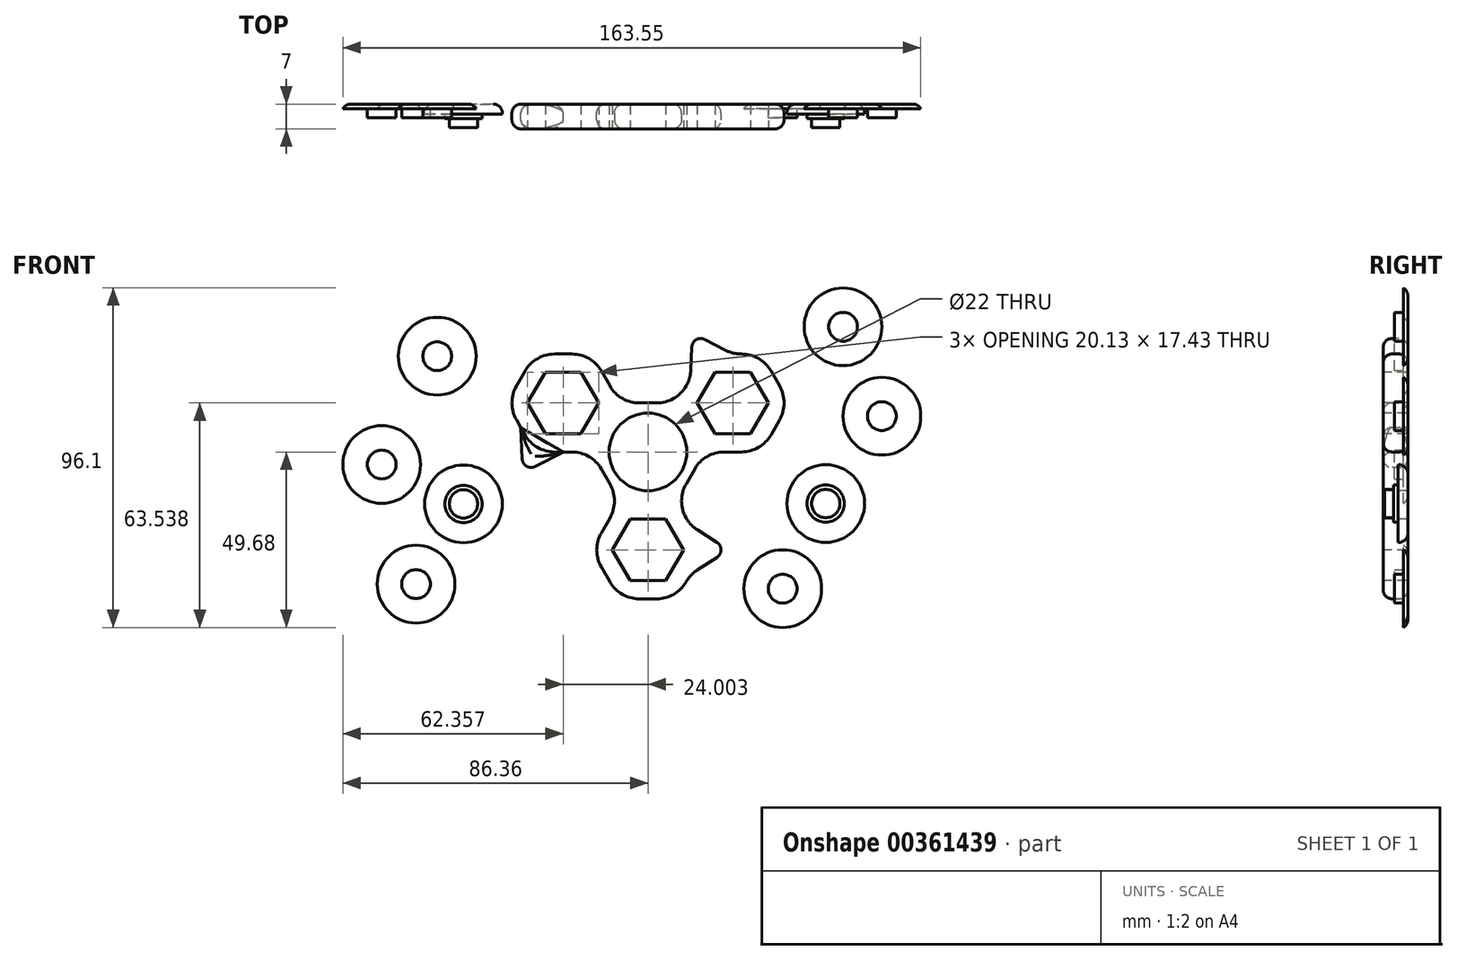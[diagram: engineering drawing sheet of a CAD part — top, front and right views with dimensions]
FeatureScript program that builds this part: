
annotation { "Feature Type Name" : "Feature", "Feature Type Description" : "" }
export const myFeature = defineFeature(function(context is Context, id is Id, definition is map)
    precondition{}
    {
        {
            var Q0;
            Q0=qCreatedBy(makeId("Front.planeOp"),FACE);
            var sketch = newSketch(context, id + "F0", { "sketchPlane" : qUnion([Q0])});
            skCircle(sketch, "E0.cCircle", {"center": v(0, 0) * mm, "radius": 13.86 * mm, "construction": true});
            skLineSegment(sketch, "E0.0", {"start": v(16, 0) * mm, "end": v(8, -13.86) * mm});
            skLineSegment(sketch, "E0.1", {"start": v(8, -13.86) * mm, "end": v(-8, -13.86) * mm});
            skLineSegment(sketch, "E0.2", {"start": v(-8, -13.86) * mm, "end": v(-16, 0) * mm});
            skLineSegment(sketch, "E0.3", {"start": v(-16, 0) * mm, "end": v(-8, 13.86) * mm});
            skLineSegment(sketch, "E0.4", {"start": v(-8, 13.86) * mm, "end": v(8, 13.86) * mm});
            skLineSegment(sketch, "E0.5", {"start": v(8, 13.86) * mm, "end": v(16, 0) * mm});
            skPoint(sketch, "E0.0.midPoint", {"position": v(12, -6.93) * mm});
            skCircle(sketch, "E1.cCircle", {"center": v(24, 13.86) * mm, "radius": 13.86 * mm, "construction": true});
            skLineSegment(sketch, "E1.0", {"start": v(32, 0) * mm, "end": v(16, 0) * mm});
            skLineSegment(sketch, "E1.1", {"start": v(16, 0) * mm, "end": v(8, 13.86) * mm});
            skLineSegment(sketch, "E1.2", {"start": v(8, 13.86) * mm, "end": v(16, 27.72) * mm});
            skLineSegment(sketch, "E1.3", {"start": v(16, 27.72) * mm, "end": v(32, 27.72) * mm});
            skLineSegment(sketch, "E1.4", {"start": v(32, 27.72) * mm, "end": v(40, 13.86) * mm});
            skLineSegment(sketch, "E1.5", {"start": v(40, 13.86) * mm, "end": v(32, 0) * mm});
            skPoint(sketch, "E1.0.midPoint", {"position": v(24, 0) * mm});
            skCircle(sketch, "E2.cCircle", {"center": v(-24, 13.86) * mm, "radius": 13.86 * mm, "construction": true});
            skLineSegment(sketch, "E2.0", {"start": v(-16, 0) * mm, "end": v(-32, 0) * mm});
            skLineSegment(sketch, "E2.1", {"start": v(-32, 0) * mm, "end": v(-40, 13.86) * mm});
            skLineSegment(sketch, "E2.2", {"start": v(-40, 13.86) * mm, "end": v(-32, 27.72) * mm});
            skLineSegment(sketch, "E2.3", {"start": v(-32, 27.72) * mm, "end": v(-16, 27.72) * mm});
            skLineSegment(sketch, "E2.4", {"start": v(-16, 27.72) * mm, "end": v(-8, 13.86) * mm});
            skLineSegment(sketch, "E2.5", {"start": v(-8, 13.86) * mm, "end": v(-16, 0) * mm});
            skCircle(sketch, "E3.cCircle", {"center": v(0, -27.72) * mm, "radius": 13.86 * mm, "construction": true});
            skLineSegment(sketch, "E3.0", {"start": v(8, -41.57) * mm, "end": v(-8, -41.57) * mm});
            skLineSegment(sketch, "E3.1", {"start": v(-8, -41.57) * mm, "end": v(-16, -27.72) * mm});
            skLineSegment(sketch, "E3.2", {"start": v(-16, -27.72) * mm, "end": v(-8, -13.86) * mm});
            skLineSegment(sketch, "E3.3", {"start": v(-8, -13.86) * mm, "end": v(8, -13.86) * mm});
            skLineSegment(sketch, "E3.4", {"start": v(8, -13.86) * mm, "end": v(16, -27.72) * mm});
            skLineSegment(sketch, "E3.5", {"start": v(16, -27.72) * mm, "end": v(8, -41.57) * mm});
            skLineSegment(sketch, "E4", {"start": v(-36, 6.93) * mm, "end": v(-24, 0) * mm});
            skLineSegment(sketch, "E5", {"start": v(-24, 0) * mm, "end": v(-36, 6.93) * mm});
            skLineSegment(sketch, "E6", {"start": v(24, 27.72) * mm, "end": v(12, 20.79) * mm});
            skLineSegment(sketch, "E7", {"start": v(12, -20.79) * mm, "end": v(12, -34.65) * mm});
            skLineSegment(sketch, "E8", {"start": v(-24, 13.86) * mm, "end": v(-35.43, -5.94) * mm});
            skLineSegment(sketch, "E9", {"start": v(24, 13.86) * mm, "end": v(12.57, 33.66) * mm});
            skLineSegment(sketch, "E10", {"start": v(0, -27.72) * mm, "end": v(22.86, -27.72) * mm});
            skPoint(sketch, "E10.endSnap0", {"position": v(12, -27.72) * mm});
            skLineSegment(sketch, "E11", {"start": v(-36, 6.93) * mm, "end": v(-35.43, -5.94) * mm});
            skLineSegment(sketch, "E12", {"start": v(-24, 0) * mm, "end": v(-35.43, -5.94) * mm});
            skLineSegment(sketch, "E13", {"start": v(12, -20.79) * mm, "end": v(22.86, -27.72) * mm});
            skLineSegment(sketch, "E14", {"start": v(12, -34.65) * mm, "end": v(22.86, -27.72) * mm});
            skLineSegment(sketch, "E15", {"start": v(12, 20.79) * mm, "end": v(12.57, 33.66) * mm});
            skLineSegment(sketch, "E16", {"start": v(24, 27.72) * mm, "end": v(12.57, 33.66) * mm});
            skLineSegment(sketch, "E17", {"start": v(12, -6.93) * mm, "end": v(0, -13.86) * mm});
            skLineSegment(sketch, "E18", {"start": v(6, -10.4) * mm, "end": v(8, -13.86) * mm});
            skLineSegment(sketch, "E19", {"start": v(-12, 6.93) * mm, "end": v(-12, -6.93) * mm});
            skLineSegment(sketch, "E20", {"start": v(-16, 0) * mm, "end": v(-12, 0) * mm});
            skLineSegment(sketch, "E21", {"start": v(-12, 0) * mm, "end": v(-14.39, 0) * mm});
            skLineSegment(sketch, "E22", {"start": v(0, 13.86) * mm, "end": v(12, 6.93) * mm});
            skLineSegment(sketch, "E23", {"start": v(8, 13.86) * mm, "end": v(6, 10.4) * mm});
            skPoint(sketch, "E23.endSnap0", {"position": v(6, 10.4) * mm});
            skLineSegment(sketch, "E24", {"start": v(6, 10.4) * mm, "end": v(7.2, 12.46) * mm});
            skLineSegment(sketch, "E25", {"start": v(9.55, 8.35) * mm, "end": v(6, 10.4) * mm});
            skLineSegment(sketch, "E26", {"start": v(6, -10.4) * mm, "end": v(7.2, -12.46) * mm});
            skCircle(sketch, "E27", {"center": v(0, 0) * mm, "radius": 42.34 * mm});
            skSolve(sketch);
        }
        {
            var Q0;
            {var subQ3=sQuery(id+"F0.wireOp",EDGE,"E15");Q0=makeQuery(id+"F0.imprint","IMPRINT",FACE,{"disambiguationData":[TD([[makeQuery(id+"F0.imprint","IMPRINT",EDGE,{"derivedFrom":subQ3}),-1.0]])]});}
            var Q1;
            {var subQ3=sQuery(id+"F0.wireOp",EDGE,"E16");Q1=makeQuery(id+"F0.imprint","IMPRINT",FACE,{"disambiguationData":[TD([[makeQuery(id+"F0.imprint","IMPRINT",EDGE,{"derivedFrom":subQ3}),1.0]])]});}
            var Q2;
            {var subQ3=sQuery(id+"F0.wireOp",EDGE,"E12");Q2=makeQuery(id+"F0.imprint","IMPRINT",FACE,{"disambiguationData":[TD([[makeQuery(id+"F0.imprint","IMPRINT",EDGE,{"derivedFrom":subQ3}),-1.0]])]});}
            var Q3;
            {var subQ3=sQuery(id+"F0.wireOp",EDGE,"E11");Q3=makeQuery(id+"F0.imprint","IMPRINT",FACE,{"disambiguationData":[TD([[makeQuery(id+"F0.imprint","IMPRINT",EDGE,{"derivedFrom":subQ3}),1.0]])]});}
            var Q4;
            {var subQ3=sQuery(id+"F0.wireOp",EDGE,"E13");Q4=makeQuery(id+"F0.imprint","IMPRINT",FACE,{"disambiguationData":[TD([[makeQuery(id+"F0.imprint","IMPRINT",EDGE,{"derivedFrom":subQ3}),-1.0]])]});}
            var Q5;
            {var subQ3=sQuery(id+"F0.wireOp",EDGE,"E14");Q5=makeQuery(id+"F0.imprint","IMPRINT",FACE,{"disambiguationData":[TD([[makeQuery(id+"F0.imprint","IMPRINT",EDGE,{"derivedFrom":subQ3}),1.0]])]});}
            var Q6;
            {var subQ3=sQuery(id+"F0.wireOp",EDGE,"E3.4");var subQ5=sQuery(id+"F0.wireOp",EDGE,"E3.3");var subQ6=makeQuery(id+"F0.imprint","INTERSECT",VERTEX,{"derivedFrom":[subQ5,subQ3]});Q6=makeQuery(id+"F0.imprint","IMPRINT",FACE,{"disambiguationData":[TD([[makeQuery(id+"F0.imprint","IMPRINT",EDGE,{"disambiguationData":[TD([[subQ6,1.0]])],"derivedFrom":subQ5}),-1.0]])]});}
            var Q7;
            {var subQ0=sQuery(id+"F0.wireOp",EDGE,"E20");Q7=makeQuery(id+"F0.imprint","IMPRINT",FACE,{"disambiguationData":[TD([[makeQuery(id+"F0.imprint","IMPRINT",EDGE,{"derivedFrom":subQ0}),-1.0]])]});}
            var Q8;
            {var subQ0=sQuery(id+"F0.wireOp",EDGE,"E23");Q8=makeQuery(id+"F0.imprint","IMPRINT",FACE,{"disambiguationData":[TD([[makeQuery(id+"F0.imprint","IMPRINT",EDGE,{"derivedFrom":subQ0}),-1.0]])]});}
            var Q9;
            {var subQ0=sQuery(id+"F0.wireOp",EDGE,"E9");var subQ3=sQuery(id+"F0.wireOp",EDGE,"E6");var subQ5=makeQuery(id+"F0.imprint","INTERSECT",VERTEX,{"derivedFrom":[subQ3,subQ0]});Q9=makeQuery(id+"F0.imprint","IMPRINT",FACE,{"disambiguationData":[TD([[makeQuery(id+"F0.imprint","IMPRINT",EDGE,{"disambiguationData":[TD([[subQ5,-1.0]])],"derivedFrom":subQ3}),-1.0]])]});}
            var Q10;
            {var subQ0=sQuery(id+"F0.wireOp",EDGE,"E9");var subQ3=sQuery(id+"F0.wireOp",EDGE,"E6");var subQ5=makeQuery(id+"F0.imprint","INTERSECT",VERTEX,{"derivedFrom":[subQ3,subQ0]});Q10=makeQuery(id+"F0.imprint","IMPRINT",FACE,{"disambiguationData":[TD([[makeQuery(id+"F0.imprint","IMPRINT",EDGE,{"disambiguationData":[TD([[subQ5,1.0]])],"derivedFrom":subQ3}),-1.0]])]});}
            var Q11;
            {var subQ0=sQuery(id+"F0.wireOp",EDGE,"E8");var subQ3=sQuery(id+"F0.wireOp",EDGE,"E5");var subQ5=makeQuery(id+"F0.imprint","INTERSECT",VERTEX,{"derivedFrom":[subQ3,subQ0]});Q11=makeQuery(id+"F0.imprint","IMPRINT",FACE,{"disambiguationData":[TD([[makeQuery(id+"F0.imprint","IMPRINT",EDGE,{"disambiguationData":[TD([[subQ5,1.0]])],"derivedFrom":subQ3}),1.0]])]});}
            var Q12;
            {var subQ0=sQuery(id+"F0.wireOp",EDGE,"E8");var subQ3=sQuery(id+"F0.wireOp",EDGE,"E5");var subQ5=makeQuery(id+"F0.imprint","INTERSECT",VERTEX,{"derivedFrom":[subQ3,subQ0]});Q12=makeQuery(id+"F0.imprint","IMPRINT",FACE,{"disambiguationData":[TD([[makeQuery(id+"F0.imprint","IMPRINT",EDGE,{"disambiguationData":[TD([[subQ5,-1.0]])],"derivedFrom":subQ3}),1.0]])]});}
            var Q13;
            {var subQ0=sQuery(id+"F0.wireOp",EDGE,"E10");var subQ3=sQuery(id+"F0.wireOp",EDGE,"E7");var subQ5=makeQuery(id+"F0.imprint","INTERSECT",VERTEX,{"derivedFrom":[subQ3,subQ0]});Q13=makeQuery(id+"F0.imprint","IMPRINT",FACE,{"disambiguationData":[TD([[makeQuery(id+"F0.imprint","IMPRINT",EDGE,{"disambiguationData":[TD([[subQ5,1.0]])],"derivedFrom":subQ3}),1.0]])]});}
            var Q14;
            {var subQ0=sQuery(id+"F0.wireOp",EDGE,"E10");var subQ3=sQuery(id+"F0.wireOp",EDGE,"E7");var subQ5=makeQuery(id+"F0.imprint","INTERSECT",VERTEX,{"derivedFrom":[subQ3,subQ0]});Q14=makeQuery(id+"F0.imprint","IMPRINT",FACE,{"disambiguationData":[TD([[makeQuery(id+"F0.imprint","IMPRINT",EDGE,{"disambiguationData":[TD([[subQ5,-1.0]])],"derivedFrom":subQ3}),1.0]])]});}
            var Q15;
            {var subQ3=sQuery(id+"F0.wireOp",EDGE,"fGXXUOoa-G3to-nFfg-Xp41-Spi5BgRDYh0n");Q15=makeQuery(id+"F0.imprint","IMPRINT",FACE,{"disambiguationData":[TD([[makeQuery(id+"F0.imprint","IMPRINT",EDGE,{"derivedFrom":subQ3}),-1.0]])]});}
            var Q16;
            {var subQ1=sQuery(id+"F0.wireOp",EDGE,"E0.1");Q16=makeQuery(id+"F0.imprint","IMPRINT",FACE,{"disambiguationData":[TD([[makeQuery(id+"F0.imprint","IMPRINT",EDGE,{"derivedFrom":subQ1}),1.0]])]});}
            var Q17;
            {var subQ0=sQuery(id+"F0.wireOp",EDGE,"E0.1");Q17=makeQuery(id+"F0.imprint","IMPRINT",FACE,{"disambiguationData":[TD([[makeQuery(id+"F0.imprint","IMPRINT",EDGE,{"derivedFrom":subQ0}),-1.0]])]});}
            var Q18;
            {var subQ6=sQuery(id+"F0.wireOp",EDGE,"E1.0");Q18=makeQuery(id+"F0.imprint","IMPRINT",FACE,{"disambiguationData":[TD([[makeQuery(id+"F0.imprint","IMPRINT",EDGE,{"derivedFrom":subQ6}),-1.0]])]});}
            var Q19;
            {var subQ0=sQuery(id+"F0.wireOp",EDGE,"E23");Q19=makeQuery(id+"F0.imprint","IMPRINT",FACE,{"disambiguationData":[TD([[makeQuery(id+"F0.imprint","IMPRINT",EDGE,{"derivedFrom":subQ0}),1.0]])]});}
            var Q20;
            {var subQ0=sQuery(id+"F0.wireOp",EDGE,"E2.2");Q20=makeQuery(id+"F0.imprint","IMPRINT",FACE,{"disambiguationData":[TD([[makeQuery(id+"F0.imprint","IMPRINT",EDGE,{"derivedFrom":subQ0}),-1.0]])]});}
            var Q21;
            {var subQ0=sQuery(id+"F0.wireOp",EDGE,"E17");var subQ18=sQuery(id+"F0.wireOp",EDGE,"E0.0");var subQ19=makeQuery(id+"F0.imprint","INTERSECT",VERTEX,{"derivedFrom":[subQ18,subQ0]});Q21=makeQuery(id+"F0.imprint","IMPRINT",FACE,{"disambiguationData":[TD([[makeQuery(id+"F0.imprint","IMPRINT",EDGE,{"disambiguationData":[TD([[subQ19,-1.0]])],"derivedFrom":subQ0}),-1.0]])]});}
            var Q22;
            {var subQ0=sQuery(id+"F0.wireOp",EDGE,"E20");Q22=makeQuery(id+"F0.imprint","IMPRINT",FACE,{"disambiguationData":[TD([[makeQuery(id+"F0.imprint","IMPRINT",EDGE,{"derivedFrom":subQ0}),1.0]])]});}
            var Q23;
            {var subQ5=sQuery(id+"F0.wireOp",EDGE,"maiLpuxs-2Sfq-8eKx-MEtN-jPa1VSy1aRe3");Q23=makeQuery(id+"F0.imprint","IMPRINT",FACE,{"disambiguationData":[TD([[makeQuery(id+"F0.imprint","IMPRINT",EDGE,{"derivedFrom":subQ5}),1.0]])]});}
            var Q24;
            {var subQ0=sQuery(id+"F0.wireOp",EDGE,"E18");Q24=makeQuery(id+"F0.imprint","IMPRINT",FACE,{"disambiguationData":[TD([[makeQuery(id+"F0.imprint","IMPRINT",EDGE,{"derivedFrom":subQ0}),1.0]])]});}
            var Q25;
            {var subQ0=sQuery(id+"F0.wireOp",EDGE,"E18");Q25=makeQuery(id+"F0.imprint","IMPRINT",FACE,{"disambiguationData":[TD([[makeQuery(id+"F0.imprint","IMPRINT",EDGE,{"derivedFrom":subQ0}),-1.0]])]});}
            extrude(context, id + "F1", {"entities" : qUnion([Q0, Q1, Q2, Q3, Q4, Q5, Q6, Q7, Q8, Q9, Q10, Q11, Q12, Q13, Q14, Q15, Q16, Q17, Q18, Q19, Q20, Q21, Q22, Q23, Q24, Q25]), "depth" : 7 * mm, "offsetDistance" : 25.4 * mm});
        }
        {
            var Q0;
            Q0=makeQuery(id+"F1.opExtrude","CAP_FACE",FACE,{"disambiguationData":[OSD([sQuery(id+"F0.wireOp",EDGE,"E0.0"),sQuery(id+"F0.wireOp",EDGE,"E0.2"),sQuery(id+"F0.wireOp",EDGE,"E0.4"),sQuery(id+"F0.wireOp",EDGE,"E1.0"),sQuery(id+"F0.wireOp",EDGE,"E1.2"),sQuery(id+"F0.wireOp",EDGE,"E1.3"),sQuery(id+"F0.wireOp",EDGE,"E1.4"),sQuery(id+"F0.wireOp",EDGE,"E1.5"),sQuery(id+"F0.wireOp",EDGE,"E2.0"),sQuery(id+"F0.wireOp",EDGE,"E2.1"),sQuery(id+"F0.wireOp",EDGE,"E2.2"),sQuery(id+"F0.wireOp",EDGE,"E2.3"),sQuery(id+"F0.wireOp",EDGE,"E2.4"),sQuery(id+"F0.wireOp",EDGE,"E3.0"),sQuery(id+"F0.wireOp",EDGE,"E3.1"),sQuery(id+"F0.wireOp",EDGE,"E3.2"),sQuery(id+"F0.wireOp",EDGE,"E3.4"),sQuery(id+"F0.wireOp",EDGE,"E3.5")])],"isStart":false});
            var sketch = newSketch(context, id + "F2", { "sketchPlane" : qUnion([Q0])});
            skCircle(sketch, "E28", {"center": v(0, 0) * mm, "radius": 11 * mm});
            skCircle(sketch, "E29.cCircle", {"center": v(-24, 13.86) * mm, "radius": 8.72 * mm, "construction": true});
            skLineSegment(sketch, "E29.0", {"start": v(-13.94, 13.86) * mm, "end": v(-18.97, 5.14) * mm});
            skLineSegment(sketch, "E29.1", {"start": v(-18.97, 5.14) * mm, "end": v(-29.03, 5.14) * mm});
            skLineSegment(sketch, "E29.2", {"start": v(-29.03, 5.14) * mm, "end": v(-34.07, 13.86) * mm});
            skLineSegment(sketch, "E29.3", {"start": v(-34.07, 13.86) * mm, "end": v(-29.03, 22.57) * mm});
            skLineSegment(sketch, "E29.4", {"start": v(-29.03, 22.57) * mm, "end": v(-18.97, 22.57) * mm});
            skLineSegment(sketch, "E29.5", {"start": v(-18.97, 22.57) * mm, "end": v(-13.94, 13.86) * mm});
            skPoint(sketch, "E29.0.midPoint", {"position": v(-16.46, 9.5) * mm});
            skCircle(sketch, "E30.cCircle", {"center": v(24, 13.86) * mm, "radius": 8.72 * mm, "construction": true});
            skLineSegment(sketch, "E30.0", {"start": v(13.94, 13.86) * mm, "end": v(18.97, 22.57) * mm});
            skLineSegment(sketch, "E30.1", {"start": v(18.97, 22.57) * mm, "end": v(29.03, 22.57) * mm});
            skLineSegment(sketch, "E30.2", {"start": v(29.03, 22.57) * mm, "end": v(34.07, 13.86) * mm});
            skLineSegment(sketch, "E30.3", {"start": v(34.07, 13.86) * mm, "end": v(29.03, 5.14) * mm});
            skLineSegment(sketch, "E30.4", {"start": v(29.03, 5.14) * mm, "end": v(18.97, 5.14) * mm});
            skLineSegment(sketch, "E30.5", {"start": v(18.97, 5.14) * mm, "end": v(13.94, 13.86) * mm});
            skPoint(sketch, "E30.0.midPoint", {"position": v(16.46, 18.22) * mm});
            skCircle(sketch, "E31.cCircle", {"center": v(0, -27.72) * mm, "radius": 8.72 * mm, "construction": true});
            skLineSegment(sketch, "E31.0", {"start": v(10.06, -27.72) * mm, "end": v(5.03, -36.43) * mm});
            skLineSegment(sketch, "E31.1", {"start": v(5.03, -36.43) * mm, "end": v(-5.03, -36.43) * mm});
            skLineSegment(sketch, "E31.2", {"start": v(-5.03, -36.43) * mm, "end": v(-10.06, -27.72) * mm});
            skLineSegment(sketch, "E31.3", {"start": v(-10.06, -27.72) * mm, "end": v(-5.03, -19) * mm});
            skLineSegment(sketch, "E31.4", {"start": v(-5.03, -19) * mm, "end": v(5.03, -19) * mm});
            skLineSegment(sketch, "E31.5", {"start": v(5.03, -19) * mm, "end": v(10.06, -27.72) * mm});
            skPoint(sketch, "E31.0.midPoint", {"position": v(7.55, -32.07) * mm});
            skSolve(sketch);
        }
        {
            var Q0;
            Q0 = qSketchRegion(id + "F2", true);
            extrude(context, id + "F3", {"entities" : qUnion([Q0]), "operationType" : NewBodyOperationType.REMOVE, "oppositeDirection" : true, "depth" : 25.4 * mm});
        }
        {
            var Q0;
            Q0=qCreatedBy(makeId("Front.planeOp"),FACE);
            var sketch = newSketch(context, id + "F4", { "sketchPlane" : qUnion([Q0])});
            skCircle(sketch, "E32", {"center": v(-52.22, -14.7) * mm, "radius": 11 * mm});
            skCircle(sketch, "E33", {"center": v(-75.36, -3.55) * mm, "radius": 11 * mm});
            skCircle(sketch, "E34", {"center": v(-59.65, 27.1) * mm, "radius": 11 * mm});
            skCircle(sketch, "E35", {"center": v(-65.64, -37.4) * mm, "radius": 11 * mm});
            skCircle(sketch, "E36", {"center": v(50.3, -14.6) * mm, "radius": 11 * mm});
            skCircle(sketch, "E37", {"center": v(55.2, 35.42) * mm, "radius": 11 * mm});
            skCircle(sketch, "E38", {"center": v(66.2, 10.12) * mm, "radius": 11 * mm});
            skCircle(sketch, "E39", {"center": v(38.13, -38.68) * mm, "radius": 11 * mm});
            skSolve(sketch);
        }
        {
            var Q0;
            Q0=makeQuery(id+"F4.imprint","IMPRINT",FACE,{"disambiguationData":[TD([[makeQuery(id+"F4.imprint","IMPRINT",EDGE,{"derivedFrom":sQuery(id+"F4.wireOp",EDGE,"E33")}),1.0]])]});
            var Q1;
            Q1=makeQuery(id+"F4.imprint","IMPRINT",FACE,{"disambiguationData":[TD([[makeQuery(id+"F4.imprint","IMPRINT",EDGE,{"derivedFrom":sQuery(id+"F4.wireOp",EDGE,"E34")}),1.0]])]});
            var Q2;
            Q2=makeQuery(id+"F4.imprint","IMPRINT",FACE,{"disambiguationData":[TD([[makeQuery(id+"F4.imprint","IMPRINT",EDGE,{"derivedFrom":sQuery(id+"F4.wireOp",EDGE,"E35")}),1.0]])]});
            var Q3;
            Q3=makeQuery(id+"F4.imprint","IMPRINT",FACE,{"disambiguationData":[TD([[makeQuery(id+"F4.imprint","IMPRINT",EDGE,{"derivedFrom":sQuery(id+"F4.wireOp",EDGE,"E37")}),1.0]])]});
            var Q4;
            Q4=makeQuery(id+"F4.imprint","IMPRINT",FACE,{"disambiguationData":[TD([[makeQuery(id+"F4.imprint","IMPRINT",EDGE,{"derivedFrom":sQuery(id+"F4.wireOp",EDGE,"E38")}),1.0]])]});
            var Q5;
            Q5=makeQuery(id+"F4.imprint","IMPRINT",FACE,{"disambiguationData":[TD([[makeQuery(id+"F4.imprint","IMPRINT",EDGE,{"derivedFrom":sQuery(id+"F4.wireOp",EDGE,"E39")}),1.0]])]});
            extrude(context, id + "F5", {"entities" : qUnion([Q0, Q1, Q2, Q3, Q4, Q5]), "depth" : 1.27 * mm});
        }
        {
            var Q0;
            Q0=makeQuery(id+"F4.imprint","IMPRINT",FACE,{"disambiguationData":[TD([[makeQuery(id+"F4.imprint","IMPRINT",EDGE,{"derivedFrom":sQuery(id+"F4.wireOp",EDGE,"E32")}),1.0]])]});
            var Q1;
            Q1=makeQuery(id+"F4.imprint","IMPRINT",FACE,{"disambiguationData":[TD([[makeQuery(id+"F4.imprint","IMPRINT",EDGE,{"derivedFrom":sQuery(id+"F4.wireOp",EDGE,"E36")}),1.0]])]});
            extrude(context, id + "F6", {"entities" : qUnion([Q0, Q1]), "operationType" : NewBodyOperationType.ADD, "depth" : 2.8 * mm});
        }
        {
            var Q0;
            Q0=makeQuery(id+"F5.opExtrude","CAP_FACE",FACE,{"disambiguationData":[OSD([sQuery(id+"F4.wireOp",EDGE,"E34")])],"isStart":false});
            var sketch = newSketch(context, id + "F7", { "sketchPlane" : qUnion([Q0])});
            skCircle(sketch, "E40", {"center": v(-59.65, 27.1) * mm, "radius": 4.08 * mm});
            skCircle(sketch, "E41", {"center": v(-75.36, -3.55) * mm, "radius": 4.08 * mm});
            skCircle(sketch, "E42", {"center": v(-65.64, -37.4) * mm, "radius": 4.08 * mm});
            skCircle(sketch, "E43", {"center": v(55.2, 35.42) * mm, "radius": 4.08 * mm});
            skCircle(sketch, "E44", {"center": v(66.2, 10.12) * mm, "radius": 4.08 * mm});
            skCircle(sketch, "E45", {"center": v(38.13, -38.68) * mm, "radius": 4.08 * mm});
            skSolve(sketch);
        }
        {
            var Q0;
            Q0=makeQuery(id+"F7.imprint","IMPRINT",FACE,{"disambiguationData":[TD([[makeQuery(id+"F7.imprint","IMPRINT",EDGE,{"derivedFrom":sQuery(id+"F7.wireOp",EDGE,"E40")}),1.0]])]});
            var Q1;
            Q1=makeQuery(id+"F7.imprint","IMPRINT",FACE,{"disambiguationData":[TD([[makeQuery(id+"F7.imprint","IMPRINT",EDGE,{"derivedFrom":sQuery(id+"F7.wireOp",EDGE,"E41")}),1.0]])]});
            var Q2;
            Q2=makeQuery(id+"F7.imprint","IMPRINT",FACE,{"disambiguationData":[TD([[makeQuery(id+"F7.imprint","IMPRINT",EDGE,{"derivedFrom":sQuery(id+"F7.wireOp",EDGE,"Lme4bchI-afO6-idkw-AQsl-qdStulvY53Mh")}),1.0]])]});
            var Q3;
            Q3=makeQuery(id+"F7.imprint","IMPRINT",FACE,{"disambiguationData":[TD([[makeQuery(id+"F7.imprint","IMPRINT",EDGE,{"derivedFrom":sQuery(id+"F7.wireOp",EDGE,"E42")}),1.0]])]});
            var Q4;
            Q4=makeQuery(id+"F7.imprint","IMPRINT",FACE,{"disambiguationData":[TD([[makeQuery(id+"F7.imprint","IMPRINT",EDGE,{"derivedFrom":sQuery(id+"F7.wireOp",EDGE,"E43")}),1.0]])]});
            var Q5;
            Q5=makeQuery(id+"F7.imprint","IMPRINT",FACE,{"disambiguationData":[TD([[makeQuery(id+"F7.imprint","IMPRINT",EDGE,{"derivedFrom":sQuery(id+"F7.wireOp",EDGE,"E44")}),1.0]])]});
            var Q6;
            Q6=makeQuery(id+"F7.imprint","IMPRINT",FACE,{"disambiguationData":[TD([[makeQuery(id+"F7.imprint","IMPRINT",EDGE,{"derivedFrom":sQuery(id+"F7.wireOp",EDGE,"E45")}),1.0]])]});
            extrude(context, id + "F8", {"entities" : qUnion([Q0, Q1, Q2, Q3, Q4, Q5, Q6]), "operationType" : NewBodyOperationType.ADD, "depth" : 2.54 * mm});
        }
        {
            var Q0;
            Q0=makeQuery(id+"F6.opExtrude","CAP_FACE",FACE,{"disambiguationData":[OSD([sQuery(id+"F4.wireOp",EDGE,"E32")])],"isStart":false});
            var sketch = newSketch(context, id + "F9", { "sketchPlane" : qUnion([Q0])});
            skCircle(sketch, "E46", {"center": v(-52.22, -14.7) * mm, "radius": 4 * mm});
            skCircle(sketch, "E47", {"center": v(50.3, -14.6) * mm, "radius": 4 * mm});
            skCircle(sketch, "E48.0", {"center": v(-52.22, -14.7) * mm, "radius": 5.27 * mm});
            skCircle(sketch, "E49.0", {"center": v(50.3, -14.6) * mm, "radius": 5.27 * mm});
            skSolve(sketch);
        }
        {
            var Q0;
            Q0=makeQuery(id+"F9.imprint","IMPRINT",FACE,{"disambiguationData":[TD([[makeQuery(id+"F9.imprint","IMPRINT",EDGE,{"derivedFrom":sQuery(id+"F9.wireOp",EDGE,"E46")}),1.0]])]});
            var Q1;
            Q1=makeQuery(id+"F9.imprint","IMPRINT",FACE,{"disambiguationData":[TD([[makeQuery(id+"F9.imprint","IMPRINT",EDGE,{"derivedFrom":sQuery(id+"F9.wireOp",EDGE,"E47")}),1.0]])]});
            extrude(context, id + "F10", {"entities" : qUnion([Q0, Q1]), "operationType" : NewBodyOperationType.ADD, "depth" : 3.8 * mm});
        }
        {
            var Q0;
            Q0=makeQuery(id+"F1.opExtrude","SWEPT_EDGE",EDGE,{"disambiguationData":[OSD([sQuery(id+"F0.wireOp",EDGE,"E1.3"),sQuery(id+"F0.wireOp",EDGE,"E1.4")])]});
            var Q1;
            Q1=makeQuery(id+"F1.opExtrude","SWEPT_EDGE",EDGE,{"disambiguationData":[OSD([sQuery(id+"F0.wireOp",EDGE,"E1.4"),sQuery(id+"F0.wireOp",EDGE,"E1.5")])]});
            var Q2;
            Q2=makeQuery(id+"F1.opExtrude","SWEPT_EDGE",EDGE,{"disambiguationData":[OSD([sQuery(id+"F0.wireOp",EDGE,"E1.0"),sQuery(id+"F0.wireOp",EDGE,"E1.5")])]});
            var Q3;
            Q3=makeQuery(id+"F1.opExtrude","SWEPT_EDGE",EDGE,{"disambiguationData":[OSD([sQuery(id+"F0.wireOp",EDGE,"E1.2"),sQuery(id+"F0.wireOp",EDGE,"E1.3")])]});
            var Q4;
            Q4=makeQuery(id+"F1.opExtrude","SWEPT_EDGE",EDGE,{"disambiguationData":[OSD([sQuery(id+"F0.wireOp",EDGE,"E0.0"),sQuery(id+"F0.wireOp",EDGE,"E1.0"),sQuery(id+"F0.wireOp",EDGE,"E1.1")])]});
            var Q5;
            Q5=makeQuery(id+"F1.opExtrude","SWEPT_EDGE",EDGE,{"disambiguationData":[OSD([sQuery(id+"F0.wireOp",EDGE,"E0.4"),sQuery(id+"F0.wireOp",EDGE,"E1.1"),sQuery(id+"F0.wireOp",EDGE,"E1.2")])]});
            var Q6;
            Q6=makeQuery(id+"F1.opExtrude","SWEPT_EDGE",EDGE,{"disambiguationData":[OSD([sQuery(id+"F0.wireOp",EDGE,"E0.4"),sQuery(id+"F0.wireOp",EDGE,"E2.4"),sQuery(id+"F0.wireOp",EDGE,"E2.5")])]});
            var Q7;
            Q7=makeQuery(id+"F1.opExtrude","SWEPT_EDGE",EDGE,{"disambiguationData":[OSD([sQuery(id+"F0.wireOp",EDGE,"E2.3"),sQuery(id+"F0.wireOp",EDGE,"E2.4")])]});
            var Q8;
            Q8=makeQuery(id+"F1.opExtrude","SWEPT_EDGE",EDGE,{"disambiguationData":[OSD([sQuery(id+"F0.wireOp",EDGE,"E2.2"),sQuery(id+"F0.wireOp",EDGE,"E2.3")])]});
            var Q9;
            Q9=makeQuery(id+"F1.opExtrude","SWEPT_EDGE",EDGE,{"disambiguationData":[OSD([sQuery(id+"F0.wireOp",EDGE,"E2.1"),sQuery(id+"F0.wireOp",EDGE,"E2.2")])]});
            var Q10;
            Q10=makeQuery(id+"F1.opExtrude","SWEPT_EDGE",EDGE,{"disambiguationData":[OSD([sQuery(id+"F0.wireOp",EDGE,"E2.0"),sQuery(id+"F0.wireOp",EDGE,"E2.1")])]});
            var Q11;
            Q11=makeQuery(id+"F1.opExtrude","SWEPT_EDGE",EDGE,{"disambiguationData":[OSD([sQuery(id+"F0.wireOp",EDGE,"E0.2"),sQuery(id+"F0.wireOp",EDGE,"E2.0"),sQuery(id+"F0.wireOp",EDGE,"E2.5")])]});
            var Q12;
            Q12=makeQuery(id+"F1.opExtrude","SWEPT_EDGE",EDGE,{"disambiguationData":[OSD([sQuery(id+"F0.wireOp",EDGE,"E0.2"),sQuery(id+"F0.wireOp",EDGE,"E3.2"),sQuery(id+"F0.wireOp",EDGE,"E3.3")])]});
            var Q13;
            Q13=makeQuery(id+"F1.opExtrude","SWEPT_EDGE",EDGE,{"disambiguationData":[OSD([sQuery(id+"F0.wireOp",EDGE,"E3.1"),sQuery(id+"F0.wireOp",EDGE,"E3.2")])]});
            var Q14;
            Q14=makeQuery(id+"F1.opExtrude","SWEPT_EDGE",EDGE,{"disambiguationData":[OSD([sQuery(id+"F0.wireOp",EDGE,"E3.0"),sQuery(id+"F0.wireOp",EDGE,"E3.1")])]});
            var Q15;
            Q15=makeQuery(id+"F1.opExtrude","SWEPT_EDGE",EDGE,{"disambiguationData":[OSD([sQuery(id+"F0.wireOp",EDGE,"E3.0"),sQuery(id+"F0.wireOp",EDGE,"E3.5")])]});
            var Q16;
            Q16=makeQuery(id+"F1.opExtrude","SWEPT_EDGE",EDGE,{"disambiguationData":[OSD([sQuery(id+"F0.wireOp",EDGE,"E3.4"),sQuery(id+"F0.wireOp",EDGE,"E3.5")])]});
            var Q17;
            Q17=makeQuery(id+"F1.opExtrude","SWEPT_EDGE",EDGE,{"disambiguationData":[OSD([sQuery(id+"F0.wireOp",EDGE,"E0.0"),sQuery(id+"F0.wireOp",EDGE,"E3.3"),sQuery(id+"F0.wireOp",EDGE,"E3.4")])]});
            fillet(context, id + "F11", {"entities" : qUnion([Q0, Q1, Q2, Q3, Q4, Q5, Q6, Q7, Q8, Q9, Q10, Q11, Q12, Q13, Q14, Q15, Q16, Q17]), "radius" : 9.65 * mm, "tangentPropagation" : true, "allowEdgeOverflow" : false});
        }
        {
            var Q0;
            Q0=makeQuery(id+"F1.opExtrude","SWEPT_EDGE",EDGE,{"disambiguationData":[OSD([sQuery(id+"F0.wireOp",EDGE,"E8"),sQuery(id+"F0.wireOp",EDGE,"E11"),sQuery(id+"F0.wireOp",EDGE,"E12")])]});
            var Q1;
            Q1=makeQuery(id+"F1.opExtrude","SWEPT_EDGE",EDGE,{"disambiguationData":[OSD([sQuery(id+"F0.wireOp",EDGE,"E10"),sQuery(id+"F0.wireOp",EDGE,"E13"),sQuery(id+"F0.wireOp",EDGE,"E14")])]});
            var Q2;
            Q2=makeQuery(id+"F1.opExtrude","SWEPT_EDGE",EDGE,{"disambiguationData":[OSD([sQuery(id+"F0.wireOp",EDGE,"E9"),sQuery(id+"F0.wireOp",EDGE,"E15"),sQuery(id+"F0.wireOp",EDGE,"E16")])]});
            fillet(context, id + "F12", {"entities" : qUnion([Q0, Q1, Q2]), "radius" : 2.54 * mm, "tangentPropagation" : true, "allowEdgeOverflow" : false});
        }
        {
            var Q0;
            {var subQ0=sQuery(id+"F0.wireOp",EDGE,"E2.2");var subQ1=sQuery(id+"F0.wireOp",EDGE,"E2.1");Q0=makeQuery(id+"F11.opFillet","BLEND_EDGE",EDGE,{"blendedFrom":[makeQuery(id+"F1.opExtrude","SWEPT_EDGE",EDGE,{"disambiguationData":[OSD([subQ1,subQ0])]}),makeQuery(id+"F1.opExtrude","CAP_FACE",FACE,{"disambiguationData":[OSD([sQuery(id+"F0.wireOp",EDGE,"E0.0"),sQuery(id+"F0.wireOp",EDGE,"E0.2"),sQuery(id+"F0.wireOp",EDGE,"E0.4"),sQuery(id+"F0.wireOp",EDGE,"E1.0"),sQuery(id+"F0.wireOp",EDGE,"E1.2"),sQuery(id+"F0.wireOp",EDGE,"E1.3"),sQuery(id+"F0.wireOp",EDGE,"E1.4"),sQuery(id+"F0.wireOp",EDGE,"E1.5"),sQuery(id+"F0.wireOp",EDGE,"E2.0"),subQ1,subQ0,sQuery(id+"F0.wireOp",EDGE,"E2.3"),sQuery(id+"F0.wireOp",EDGE,"E2.4"),sQuery(id+"F0.wireOp",EDGE,"E3.0"),sQuery(id+"F0.wireOp",EDGE,"E3.1"),sQuery(id+"F0.wireOp",EDGE,"E3.2"),sQuery(id+"F0.wireOp",EDGE,"E3.4"),sQuery(id+"F0.wireOp",EDGE,"E3.5"),sQuery(id+"F0.wireOp",EDGE,"E11"),sQuery(id+"F0.wireOp",EDGE,"E12"),sQuery(id+"F0.wireOp",EDGE,"E13"),sQuery(id+"F0.wireOp",EDGE,"E14"),sQuery(id+"F0.wireOp",EDGE,"E15"),sQuery(id+"F0.wireOp",EDGE,"E16"),sQuery(id+"F0.wireOp",EDGE,"E17"),sQuery(id+"F0.wireOp",EDGE,"fGXXUOoa-G3to-nFfg-Xp41-Spi5BgRDYh0n"),sQuery(id+"F0.wireOp",EDGE,"maiLpuxs-2Sfq-8eKx-MEtN-jPa1VSy1aRe3"),sQuery(id+"F0.wireOp",EDGE,"E19"),sQuery(id+"F0.wireOp",EDGE,"TkPDQIJV-pblC-kMUo-zlvk-0mYhqbRm7784"),sQuery(id+"F0.wireOp",EDGE,"A3QQ103k-oBam-uK2f-Ywbn-FOsahd6y3kCF"),sQuery(id+"F0.wireOp",EDGE,"E22"),sQuery(id+"F0.wireOp",EDGE,"O4fUSGsA-sgfy-2hAb-lYRv-adjy5g4jnHMn"),sQuery(id+"F0.wireOp",EDGE,"he4H8z8F-eg87-8e6K-5810-5zuvFcfIEFNb")])],"isStart":false})],"blendedInto":[makeQuery(id+"F1.opExtrude","CAP_FACE",FACE,{"disambiguationData":[OSD([sQuery(id+"F0.wireOp",EDGE,"E0.0"),sQuery(id+"F0.wireOp",EDGE,"E0.2"),sQuery(id+"F0.wireOp",EDGE,"E0.4"),sQuery(id+"F0.wireOp",EDGE,"E1.0"),sQuery(id+"F0.wireOp",EDGE,"E1.2"),sQuery(id+"F0.wireOp",EDGE,"E1.3"),sQuery(id+"F0.wireOp",EDGE,"E1.4"),sQuery(id+"F0.wireOp",EDGE,"E1.5"),sQuery(id+"F0.wireOp",EDGE,"E2.0"),subQ1,subQ0,sQuery(id+"F0.wireOp",EDGE,"E2.3"),sQuery(id+"F0.wireOp",EDGE,"E2.4"),sQuery(id+"F0.wireOp",EDGE,"E3.0"),sQuery(id+"F0.wireOp",EDGE,"E3.1"),sQuery(id+"F0.wireOp",EDGE,"E3.2"),sQuery(id+"F0.wireOp",EDGE,"E3.4"),sQuery(id+"F0.wireOp",EDGE,"E3.5"),sQuery(id+"F0.wireOp",EDGE,"E11"),sQuery(id+"F0.wireOp",EDGE,"E12"),sQuery(id+"F0.wireOp",EDGE,"E13"),sQuery(id+"F0.wireOp",EDGE,"E14"),sQuery(id+"F0.wireOp",EDGE,"E15"),sQuery(id+"F0.wireOp",EDGE,"E16"),sQuery(id+"F0.wireOp",EDGE,"E17"),sQuery(id+"F0.wireOp",EDGE,"fGXXUOoa-G3to-nFfg-Xp41-Spi5BgRDYh0n"),sQuery(id+"F0.wireOp",EDGE,"maiLpuxs-2Sfq-8eKx-MEtN-jPa1VSy1aRe3"),sQuery(id+"F0.wireOp",EDGE,"E19"),sQuery(id+"F0.wireOp",EDGE,"TkPDQIJV-pblC-kMUo-zlvk-0mYhqbRm7784"),sQuery(id+"F0.wireOp",EDGE,"A3QQ103k-oBam-uK2f-Ywbn-FOsahd6y3kCF"),sQuery(id+"F0.wireOp",EDGE,"E22"),sQuery(id+"F0.wireOp",EDGE,"O4fUSGsA-sgfy-2hAb-lYRv-adjy5g4jnHMn"),sQuery(id+"F0.wireOp",EDGE,"he4H8z8F-eg87-8e6K-5810-5zuvFcfIEFNb")])],"isStart":false})]});}
            var Q1;
            Q1=makeQuery(id+"F1.opExtrude","CAP_EDGE",EDGE,{"disambiguationData":[OSD([sQuery(id+"F0.wireOp",EDGE,"E2.2")])],"isStart":false});
            var Q2;
            {var subQ0=sQuery(id+"F0.wireOp",EDGE,"E2.3");var subQ1=sQuery(id+"F0.wireOp",EDGE,"E2.2");Q2=makeQuery(id+"F11.opFillet","BLEND_EDGE",EDGE,{"blendedFrom":[makeQuery(id+"F1.opExtrude","SWEPT_EDGE",EDGE,{"disambiguationData":[OSD([subQ1,subQ0])]}),makeQuery(id+"F1.opExtrude","CAP_FACE",FACE,{"disambiguationData":[OSD([sQuery(id+"F0.wireOp",EDGE,"E0.0"),sQuery(id+"F0.wireOp",EDGE,"E0.2"),sQuery(id+"F0.wireOp",EDGE,"E0.4"),sQuery(id+"F0.wireOp",EDGE,"E1.0"),sQuery(id+"F0.wireOp",EDGE,"E1.2"),sQuery(id+"F0.wireOp",EDGE,"E1.3"),sQuery(id+"F0.wireOp",EDGE,"E1.4"),sQuery(id+"F0.wireOp",EDGE,"E1.5"),sQuery(id+"F0.wireOp",EDGE,"E2.0"),sQuery(id+"F0.wireOp",EDGE,"E2.1"),subQ1,subQ0,sQuery(id+"F0.wireOp",EDGE,"E2.4"),sQuery(id+"F0.wireOp",EDGE,"E3.0"),sQuery(id+"F0.wireOp",EDGE,"E3.1"),sQuery(id+"F0.wireOp",EDGE,"E3.2"),sQuery(id+"F0.wireOp",EDGE,"E3.4"),sQuery(id+"F0.wireOp",EDGE,"E3.5"),sQuery(id+"F0.wireOp",EDGE,"E11"),sQuery(id+"F0.wireOp",EDGE,"E12"),sQuery(id+"F0.wireOp",EDGE,"E13"),sQuery(id+"F0.wireOp",EDGE,"E14"),sQuery(id+"F0.wireOp",EDGE,"E15"),sQuery(id+"F0.wireOp",EDGE,"E16"),sQuery(id+"F0.wireOp",EDGE,"E17"),sQuery(id+"F0.wireOp",EDGE,"fGXXUOoa-G3to-nFfg-Xp41-Spi5BgRDYh0n"),sQuery(id+"F0.wireOp",EDGE,"maiLpuxs-2Sfq-8eKx-MEtN-jPa1VSy1aRe3"),sQuery(id+"F0.wireOp",EDGE,"E19"),sQuery(id+"F0.wireOp",EDGE,"TkPDQIJV-pblC-kMUo-zlvk-0mYhqbRm7784"),sQuery(id+"F0.wireOp",EDGE,"A3QQ103k-oBam-uK2f-Ywbn-FOsahd6y3kCF"),sQuery(id+"F0.wireOp",EDGE,"E22"),sQuery(id+"F0.wireOp",EDGE,"O4fUSGsA-sgfy-2hAb-lYRv-adjy5g4jnHMn"),sQuery(id+"F0.wireOp",EDGE,"he4H8z8F-eg87-8e6K-5810-5zuvFcfIEFNb")])],"isStart":false})],"blendedInto":[makeQuery(id+"F1.opExtrude","CAP_FACE",FACE,{"disambiguationData":[OSD([sQuery(id+"F0.wireOp",EDGE,"E0.0"),sQuery(id+"F0.wireOp",EDGE,"E0.2"),sQuery(id+"F0.wireOp",EDGE,"E0.4"),sQuery(id+"F0.wireOp",EDGE,"E1.0"),sQuery(id+"F0.wireOp",EDGE,"E1.2"),sQuery(id+"F0.wireOp",EDGE,"E1.3"),sQuery(id+"F0.wireOp",EDGE,"E1.4"),sQuery(id+"F0.wireOp",EDGE,"E1.5"),sQuery(id+"F0.wireOp",EDGE,"E2.0"),sQuery(id+"F0.wireOp",EDGE,"E2.1"),subQ1,subQ0,sQuery(id+"F0.wireOp",EDGE,"E2.4"),sQuery(id+"F0.wireOp",EDGE,"E3.0"),sQuery(id+"F0.wireOp",EDGE,"E3.1"),sQuery(id+"F0.wireOp",EDGE,"E3.2"),sQuery(id+"F0.wireOp",EDGE,"E3.4"),sQuery(id+"F0.wireOp",EDGE,"E3.5"),sQuery(id+"F0.wireOp",EDGE,"E11"),sQuery(id+"F0.wireOp",EDGE,"E12"),sQuery(id+"F0.wireOp",EDGE,"E13"),sQuery(id+"F0.wireOp",EDGE,"E14"),sQuery(id+"F0.wireOp",EDGE,"E15"),sQuery(id+"F0.wireOp",EDGE,"E16"),sQuery(id+"F0.wireOp",EDGE,"E17"),sQuery(id+"F0.wireOp",EDGE,"fGXXUOoa-G3to-nFfg-Xp41-Spi5BgRDYh0n"),sQuery(id+"F0.wireOp",EDGE,"maiLpuxs-2Sfq-8eKx-MEtN-jPa1VSy1aRe3"),sQuery(id+"F0.wireOp",EDGE,"E19"),sQuery(id+"F0.wireOp",EDGE,"TkPDQIJV-pblC-kMUo-zlvk-0mYhqbRm7784"),sQuery(id+"F0.wireOp",EDGE,"A3QQ103k-oBam-uK2f-Ywbn-FOsahd6y3kCF"),sQuery(id+"F0.wireOp",EDGE,"E22"),sQuery(id+"F0.wireOp",EDGE,"O4fUSGsA-sgfy-2hAb-lYRv-adjy5g4jnHMn"),sQuery(id+"F0.wireOp",EDGE,"he4H8z8F-eg87-8e6K-5810-5zuvFcfIEFNb")])],"isStart":false})]});}
            var Q3;
            Q3=makeQuery(id+"F1.opExtrude","CAP_EDGE",EDGE,{"disambiguationData":[OSD([sQuery(id+"F0.wireOp",EDGE,"E2.3")])],"isStart":false});
            var Q4;
            {var subQ0=sQuery(id+"F0.wireOp",EDGE,"E2.4");var subQ1=sQuery(id+"F0.wireOp",EDGE,"E2.3");Q4=makeQuery(id+"F11.opFillet","BLEND_EDGE",EDGE,{"blendedFrom":[makeQuery(id+"F1.opExtrude","SWEPT_EDGE",EDGE,{"disambiguationData":[OSD([subQ1,subQ0])]}),makeQuery(id+"F1.opExtrude","CAP_FACE",FACE,{"disambiguationData":[OSD([sQuery(id+"F0.wireOp",EDGE,"E0.0"),sQuery(id+"F0.wireOp",EDGE,"E0.2"),sQuery(id+"F0.wireOp",EDGE,"E0.4"),sQuery(id+"F0.wireOp",EDGE,"E1.0"),sQuery(id+"F0.wireOp",EDGE,"E1.2"),sQuery(id+"F0.wireOp",EDGE,"E1.3"),sQuery(id+"F0.wireOp",EDGE,"E1.4"),sQuery(id+"F0.wireOp",EDGE,"E1.5"),sQuery(id+"F0.wireOp",EDGE,"E2.0"),sQuery(id+"F0.wireOp",EDGE,"E2.1"),sQuery(id+"F0.wireOp",EDGE,"E2.2"),subQ1,subQ0,sQuery(id+"F0.wireOp",EDGE,"E3.0"),sQuery(id+"F0.wireOp",EDGE,"E3.1"),sQuery(id+"F0.wireOp",EDGE,"E3.2"),sQuery(id+"F0.wireOp",EDGE,"E3.4"),sQuery(id+"F0.wireOp",EDGE,"E3.5"),sQuery(id+"F0.wireOp",EDGE,"E11"),sQuery(id+"F0.wireOp",EDGE,"E12"),sQuery(id+"F0.wireOp",EDGE,"E13"),sQuery(id+"F0.wireOp",EDGE,"E14"),sQuery(id+"F0.wireOp",EDGE,"E15"),sQuery(id+"F0.wireOp",EDGE,"E16"),sQuery(id+"F0.wireOp",EDGE,"E17"),sQuery(id+"F0.wireOp",EDGE,"fGXXUOoa-G3to-nFfg-Xp41-Spi5BgRDYh0n"),sQuery(id+"F0.wireOp",EDGE,"maiLpuxs-2Sfq-8eKx-MEtN-jPa1VSy1aRe3"),sQuery(id+"F0.wireOp",EDGE,"E19"),sQuery(id+"F0.wireOp",EDGE,"TkPDQIJV-pblC-kMUo-zlvk-0mYhqbRm7784"),sQuery(id+"F0.wireOp",EDGE,"A3QQ103k-oBam-uK2f-Ywbn-FOsahd6y3kCF"),sQuery(id+"F0.wireOp",EDGE,"E22"),sQuery(id+"F0.wireOp",EDGE,"O4fUSGsA-sgfy-2hAb-lYRv-adjy5g4jnHMn"),sQuery(id+"F0.wireOp",EDGE,"he4H8z8F-eg87-8e6K-5810-5zuvFcfIEFNb")])],"isStart":false})],"blendedInto":[makeQuery(id+"F1.opExtrude","CAP_FACE",FACE,{"disambiguationData":[OSD([sQuery(id+"F0.wireOp",EDGE,"E0.0"),sQuery(id+"F0.wireOp",EDGE,"E0.2"),sQuery(id+"F0.wireOp",EDGE,"E0.4"),sQuery(id+"F0.wireOp",EDGE,"E1.0"),sQuery(id+"F0.wireOp",EDGE,"E1.2"),sQuery(id+"F0.wireOp",EDGE,"E1.3"),sQuery(id+"F0.wireOp",EDGE,"E1.4"),sQuery(id+"F0.wireOp",EDGE,"E1.5"),sQuery(id+"F0.wireOp",EDGE,"E2.0"),sQuery(id+"F0.wireOp",EDGE,"E2.1"),sQuery(id+"F0.wireOp",EDGE,"E2.2"),subQ1,subQ0,sQuery(id+"F0.wireOp",EDGE,"E3.0"),sQuery(id+"F0.wireOp",EDGE,"E3.1"),sQuery(id+"F0.wireOp",EDGE,"E3.2"),sQuery(id+"F0.wireOp",EDGE,"E3.4"),sQuery(id+"F0.wireOp",EDGE,"E3.5"),sQuery(id+"F0.wireOp",EDGE,"E11"),sQuery(id+"F0.wireOp",EDGE,"E12"),sQuery(id+"F0.wireOp",EDGE,"E13"),sQuery(id+"F0.wireOp",EDGE,"E14"),sQuery(id+"F0.wireOp",EDGE,"E15"),sQuery(id+"F0.wireOp",EDGE,"E16"),sQuery(id+"F0.wireOp",EDGE,"E17"),sQuery(id+"F0.wireOp",EDGE,"fGXXUOoa-G3to-nFfg-Xp41-Spi5BgRDYh0n"),sQuery(id+"F0.wireOp",EDGE,"maiLpuxs-2Sfq-8eKx-MEtN-jPa1VSy1aRe3"),sQuery(id+"F0.wireOp",EDGE,"E19"),sQuery(id+"F0.wireOp",EDGE,"TkPDQIJV-pblC-kMUo-zlvk-0mYhqbRm7784"),sQuery(id+"F0.wireOp",EDGE,"A3QQ103k-oBam-uK2f-Ywbn-FOsahd6y3kCF"),sQuery(id+"F0.wireOp",EDGE,"E22"),sQuery(id+"F0.wireOp",EDGE,"O4fUSGsA-sgfy-2hAb-lYRv-adjy5g4jnHMn"),sQuery(id+"F0.wireOp",EDGE,"he4H8z8F-eg87-8e6K-5810-5zuvFcfIEFNb")])],"isStart":false})]});}
            var Q5;
            Q5=makeQuery(id+"F1.opExtrude","CAP_EDGE",EDGE,{"disambiguationData":[OSD([sQuery(id+"F0.wireOp",EDGE,"E2.4")])],"isStart":false});
            var Q6;
            {var subQ0=sQuery(id+"F0.wireOp",EDGE,"E2.4");var subQ1=sQuery(id+"F0.wireOp",EDGE,"E0.4");Q6=makeQuery(id+"F11.opFillet","BLEND_EDGE",EDGE,{"blendedFrom":[makeQuery(id+"F1.opExtrude","SWEPT_EDGE",EDGE,{"disambiguationData":[OSD([subQ1,subQ0,sQuery(id+"F0.wireOp",EDGE,"E2.5")])]}),makeQuery(id+"F1.opExtrude","CAP_FACE",FACE,{"disambiguationData":[OSD([sQuery(id+"F0.wireOp",EDGE,"E0.0"),sQuery(id+"F0.wireOp",EDGE,"E0.2"),subQ1,sQuery(id+"F0.wireOp",EDGE,"E1.0"),sQuery(id+"F0.wireOp",EDGE,"E1.2"),sQuery(id+"F0.wireOp",EDGE,"E1.3"),sQuery(id+"F0.wireOp",EDGE,"E1.4"),sQuery(id+"F0.wireOp",EDGE,"E1.5"),sQuery(id+"F0.wireOp",EDGE,"E2.0"),sQuery(id+"F0.wireOp",EDGE,"E2.1"),sQuery(id+"F0.wireOp",EDGE,"E2.2"),sQuery(id+"F0.wireOp",EDGE,"E2.3"),subQ0,sQuery(id+"F0.wireOp",EDGE,"E3.0"),sQuery(id+"F0.wireOp",EDGE,"E3.1"),sQuery(id+"F0.wireOp",EDGE,"E3.2"),sQuery(id+"F0.wireOp",EDGE,"E3.4"),sQuery(id+"F0.wireOp",EDGE,"E3.5"),sQuery(id+"F0.wireOp",EDGE,"E11"),sQuery(id+"F0.wireOp",EDGE,"E12"),sQuery(id+"F0.wireOp",EDGE,"E13"),sQuery(id+"F0.wireOp",EDGE,"E14"),sQuery(id+"F0.wireOp",EDGE,"E15"),sQuery(id+"F0.wireOp",EDGE,"E16"),sQuery(id+"F0.wireOp",EDGE,"E17"),sQuery(id+"F0.wireOp",EDGE,"fGXXUOoa-G3to-nFfg-Xp41-Spi5BgRDYh0n"),sQuery(id+"F0.wireOp",EDGE,"maiLpuxs-2Sfq-8eKx-MEtN-jPa1VSy1aRe3"),sQuery(id+"F0.wireOp",EDGE,"E19"),sQuery(id+"F0.wireOp",EDGE,"TkPDQIJV-pblC-kMUo-zlvk-0mYhqbRm7784"),sQuery(id+"F0.wireOp",EDGE,"A3QQ103k-oBam-uK2f-Ywbn-FOsahd6y3kCF"),sQuery(id+"F0.wireOp",EDGE,"E22"),sQuery(id+"F0.wireOp",EDGE,"O4fUSGsA-sgfy-2hAb-lYRv-adjy5g4jnHMn"),sQuery(id+"F0.wireOp",EDGE,"he4H8z8F-eg87-8e6K-5810-5zuvFcfIEFNb")])],"isStart":false})],"blendedInto":[makeQuery(id+"F1.opExtrude","CAP_FACE",FACE,{"disambiguationData":[OSD([sQuery(id+"F0.wireOp",EDGE,"E0.0"),sQuery(id+"F0.wireOp",EDGE,"E0.2"),subQ1,sQuery(id+"F0.wireOp",EDGE,"E1.0"),sQuery(id+"F0.wireOp",EDGE,"E1.2"),sQuery(id+"F0.wireOp",EDGE,"E1.3"),sQuery(id+"F0.wireOp",EDGE,"E1.4"),sQuery(id+"F0.wireOp",EDGE,"E1.5"),sQuery(id+"F0.wireOp",EDGE,"E2.0"),sQuery(id+"F0.wireOp",EDGE,"E2.1"),sQuery(id+"F0.wireOp",EDGE,"E2.2"),sQuery(id+"F0.wireOp",EDGE,"E2.3"),subQ0,sQuery(id+"F0.wireOp",EDGE,"E3.0"),sQuery(id+"F0.wireOp",EDGE,"E3.1"),sQuery(id+"F0.wireOp",EDGE,"E3.2"),sQuery(id+"F0.wireOp",EDGE,"E3.4"),sQuery(id+"F0.wireOp",EDGE,"E3.5"),sQuery(id+"F0.wireOp",EDGE,"E11"),sQuery(id+"F0.wireOp",EDGE,"E12"),sQuery(id+"F0.wireOp",EDGE,"E13"),sQuery(id+"F0.wireOp",EDGE,"E14"),sQuery(id+"F0.wireOp",EDGE,"E15"),sQuery(id+"F0.wireOp",EDGE,"E16"),sQuery(id+"F0.wireOp",EDGE,"E17"),sQuery(id+"F0.wireOp",EDGE,"fGXXUOoa-G3to-nFfg-Xp41-Spi5BgRDYh0n"),sQuery(id+"F0.wireOp",EDGE,"maiLpuxs-2Sfq-8eKx-MEtN-jPa1VSy1aRe3"),sQuery(id+"F0.wireOp",EDGE,"E19"),sQuery(id+"F0.wireOp",EDGE,"TkPDQIJV-pblC-kMUo-zlvk-0mYhqbRm7784"),sQuery(id+"F0.wireOp",EDGE,"A3QQ103k-oBam-uK2f-Ywbn-FOsahd6y3kCF"),sQuery(id+"F0.wireOp",EDGE,"E22"),sQuery(id+"F0.wireOp",EDGE,"O4fUSGsA-sgfy-2hAb-lYRv-adjy5g4jnHMn"),sQuery(id+"F0.wireOp",EDGE,"he4H8z8F-eg87-8e6K-5810-5zuvFcfIEFNb")])],"isStart":false})]});}
            var Q7;
            Q7=makeQuery(id+"F1.opExtrude","CAP_EDGE",EDGE,{"disambiguationData":[OSD([sQuery(id+"F0.wireOp",EDGE,"E0.4")])],"isStart":false});
            var Q8;
            {var subQ0=sQuery(id+"F0.wireOp",EDGE,"E1.2");var subQ1=sQuery(id+"F0.wireOp",EDGE,"E0.4");Q8=makeQuery(id+"F11.opFillet","BLEND_EDGE",EDGE,{"blendedFrom":[makeQuery(id+"F1.opExtrude","SWEPT_EDGE",EDGE,{"disambiguationData":[OSD([subQ1,sQuery(id+"F0.wireOp",EDGE,"E1.1"),subQ0,sQuery(id+"F0.wireOp",EDGE,"E23")])]}),makeQuery(id+"F1.opExtrude","CAP_FACE",FACE,{"disambiguationData":[OSD([sQuery(id+"F0.wireOp",EDGE,"E0.0"),sQuery(id+"F0.wireOp",EDGE,"E0.2"),subQ1,sQuery(id+"F0.wireOp",EDGE,"E1.0"),subQ0,sQuery(id+"F0.wireOp",EDGE,"E1.3"),sQuery(id+"F0.wireOp",EDGE,"E1.4"),sQuery(id+"F0.wireOp",EDGE,"E1.5"),sQuery(id+"F0.wireOp",EDGE,"E2.0"),sQuery(id+"F0.wireOp",EDGE,"E2.1"),sQuery(id+"F0.wireOp",EDGE,"E2.2"),sQuery(id+"F0.wireOp",EDGE,"E2.3"),sQuery(id+"F0.wireOp",EDGE,"E2.4"),sQuery(id+"F0.wireOp",EDGE,"E3.0"),sQuery(id+"F0.wireOp",EDGE,"E3.1"),sQuery(id+"F0.wireOp",EDGE,"E3.2"),sQuery(id+"F0.wireOp",EDGE,"E3.4"),sQuery(id+"F0.wireOp",EDGE,"E3.5"),sQuery(id+"F0.wireOp",EDGE,"E11"),sQuery(id+"F0.wireOp",EDGE,"E12"),sQuery(id+"F0.wireOp",EDGE,"E13"),sQuery(id+"F0.wireOp",EDGE,"E14"),sQuery(id+"F0.wireOp",EDGE,"E15"),sQuery(id+"F0.wireOp",EDGE,"E16"),sQuery(id+"F0.wireOp",EDGE,"E17"),sQuery(id+"F0.wireOp",EDGE,"fGXXUOoa-G3to-nFfg-Xp41-Spi5BgRDYh0n"),sQuery(id+"F0.wireOp",EDGE,"maiLpuxs-2Sfq-8eKx-MEtN-jPa1VSy1aRe3"),sQuery(id+"F0.wireOp",EDGE,"E19"),sQuery(id+"F0.wireOp",EDGE,"TkPDQIJV-pblC-kMUo-zlvk-0mYhqbRm7784"),sQuery(id+"F0.wireOp",EDGE,"A3QQ103k-oBam-uK2f-Ywbn-FOsahd6y3kCF"),sQuery(id+"F0.wireOp",EDGE,"E22"),sQuery(id+"F0.wireOp",EDGE,"O4fUSGsA-sgfy-2hAb-lYRv-adjy5g4jnHMn"),sQuery(id+"F0.wireOp",EDGE,"he4H8z8F-eg87-8e6K-5810-5zuvFcfIEFNb")])],"isStart":false})],"blendedInto":[makeQuery(id+"F1.opExtrude","CAP_FACE",FACE,{"disambiguationData":[OSD([sQuery(id+"F0.wireOp",EDGE,"E0.0"),sQuery(id+"F0.wireOp",EDGE,"E0.2"),subQ1,sQuery(id+"F0.wireOp",EDGE,"E1.0"),subQ0,sQuery(id+"F0.wireOp",EDGE,"E1.3"),sQuery(id+"F0.wireOp",EDGE,"E1.4"),sQuery(id+"F0.wireOp",EDGE,"E1.5"),sQuery(id+"F0.wireOp",EDGE,"E2.0"),sQuery(id+"F0.wireOp",EDGE,"E2.1"),sQuery(id+"F0.wireOp",EDGE,"E2.2"),sQuery(id+"F0.wireOp",EDGE,"E2.3"),sQuery(id+"F0.wireOp",EDGE,"E2.4"),sQuery(id+"F0.wireOp",EDGE,"E3.0"),sQuery(id+"F0.wireOp",EDGE,"E3.1"),sQuery(id+"F0.wireOp",EDGE,"E3.2"),sQuery(id+"F0.wireOp",EDGE,"E3.4"),sQuery(id+"F0.wireOp",EDGE,"E3.5"),sQuery(id+"F0.wireOp",EDGE,"E11"),sQuery(id+"F0.wireOp",EDGE,"E12"),sQuery(id+"F0.wireOp",EDGE,"E13"),sQuery(id+"F0.wireOp",EDGE,"E14"),sQuery(id+"F0.wireOp",EDGE,"E15"),sQuery(id+"F0.wireOp",EDGE,"E16"),sQuery(id+"F0.wireOp",EDGE,"E17"),sQuery(id+"F0.wireOp",EDGE,"fGXXUOoa-G3to-nFfg-Xp41-Spi5BgRDYh0n"),sQuery(id+"F0.wireOp",EDGE,"maiLpuxs-2Sfq-8eKx-MEtN-jPa1VSy1aRe3"),sQuery(id+"F0.wireOp",EDGE,"E19"),sQuery(id+"F0.wireOp",EDGE,"TkPDQIJV-pblC-kMUo-zlvk-0mYhqbRm7784"),sQuery(id+"F0.wireOp",EDGE,"A3QQ103k-oBam-uK2f-Ywbn-FOsahd6y3kCF"),sQuery(id+"F0.wireOp",EDGE,"E22"),sQuery(id+"F0.wireOp",EDGE,"O4fUSGsA-sgfy-2hAb-lYRv-adjy5g4jnHMn"),sQuery(id+"F0.wireOp",EDGE,"he4H8z8F-eg87-8e6K-5810-5zuvFcfIEFNb")])],"isStart":false})]});}
            var Q9;
            Q9=makeQuery(id+"F1.opExtrude","CAP_EDGE",EDGE,{"disambiguationData":[OSD([sQuery(id+"F0.wireOp",EDGE,"E1.2")])],"isStart":false});
            var Q10;
            Q10=makeQuery(id+"F1.opExtrude","CAP_EDGE",EDGE,{"disambiguationData":[OSD([sQuery(id+"F0.wireOp",EDGE,"E15")])],"isStart":false});
            var Q11;
            {var subQ0=sQuery(id+"F0.wireOp",EDGE,"E16");var subQ1=sQuery(id+"F0.wireOp",EDGE,"E15");Q11=makeQuery(id+"F12.opFillet","BLEND_EDGE",EDGE,{"blendedFrom":[makeQuery(id+"F1.opExtrude","SWEPT_EDGE",EDGE,{"disambiguationData":[OSD([sQuery(id+"F0.wireOp",EDGE,"E9"),subQ1,subQ0])]}),makeQuery(id+"F1.opExtrude","CAP_FACE",FACE,{"disambiguationData":[OSD([sQuery(id+"F0.wireOp",EDGE,"E0.0"),sQuery(id+"F0.wireOp",EDGE,"E0.2"),sQuery(id+"F0.wireOp",EDGE,"E0.4"),sQuery(id+"F0.wireOp",EDGE,"E1.0"),sQuery(id+"F0.wireOp",EDGE,"E1.2"),sQuery(id+"F0.wireOp",EDGE,"E1.3"),sQuery(id+"F0.wireOp",EDGE,"E1.4"),sQuery(id+"F0.wireOp",EDGE,"E1.5"),sQuery(id+"F0.wireOp",EDGE,"E2.0"),sQuery(id+"F0.wireOp",EDGE,"E2.1"),sQuery(id+"F0.wireOp",EDGE,"E2.2"),sQuery(id+"F0.wireOp",EDGE,"E2.3"),sQuery(id+"F0.wireOp",EDGE,"E2.4"),sQuery(id+"F0.wireOp",EDGE,"E3.0"),sQuery(id+"F0.wireOp",EDGE,"E3.1"),sQuery(id+"F0.wireOp",EDGE,"E3.2"),sQuery(id+"F0.wireOp",EDGE,"E3.4"),sQuery(id+"F0.wireOp",EDGE,"E3.5"),sQuery(id+"F0.wireOp",EDGE,"E11"),sQuery(id+"F0.wireOp",EDGE,"E12"),sQuery(id+"F0.wireOp",EDGE,"E13"),sQuery(id+"F0.wireOp",EDGE,"E14"),subQ1,subQ0,sQuery(id+"F0.wireOp",EDGE,"E17"),sQuery(id+"F0.wireOp",EDGE,"fGXXUOoa-G3to-nFfg-Xp41-Spi5BgRDYh0n"),sQuery(id+"F0.wireOp",EDGE,"maiLpuxs-2Sfq-8eKx-MEtN-jPa1VSy1aRe3"),sQuery(id+"F0.wireOp",EDGE,"E19"),sQuery(id+"F0.wireOp",EDGE,"TkPDQIJV-pblC-kMUo-zlvk-0mYhqbRm7784"),sQuery(id+"F0.wireOp",EDGE,"A3QQ103k-oBam-uK2f-Ywbn-FOsahd6y3kCF"),sQuery(id+"F0.wireOp",EDGE,"E22"),sQuery(id+"F0.wireOp",EDGE,"O4fUSGsA-sgfy-2hAb-lYRv-adjy5g4jnHMn"),sQuery(id+"F0.wireOp",EDGE,"he4H8z8F-eg87-8e6K-5810-5zuvFcfIEFNb")])],"isStart":false})],"blendedInto":[makeQuery(id+"F1.opExtrude","CAP_FACE",FACE,{"disambiguationData":[OSD([sQuery(id+"F0.wireOp",EDGE,"E0.0"),sQuery(id+"F0.wireOp",EDGE,"E0.2"),sQuery(id+"F0.wireOp",EDGE,"E0.4"),sQuery(id+"F0.wireOp",EDGE,"E1.0"),sQuery(id+"F0.wireOp",EDGE,"E1.2"),sQuery(id+"F0.wireOp",EDGE,"E1.3"),sQuery(id+"F0.wireOp",EDGE,"E1.4"),sQuery(id+"F0.wireOp",EDGE,"E1.5"),sQuery(id+"F0.wireOp",EDGE,"E2.0"),sQuery(id+"F0.wireOp",EDGE,"E2.1"),sQuery(id+"F0.wireOp",EDGE,"E2.2"),sQuery(id+"F0.wireOp",EDGE,"E2.3"),sQuery(id+"F0.wireOp",EDGE,"E2.4"),sQuery(id+"F0.wireOp",EDGE,"E3.0"),sQuery(id+"F0.wireOp",EDGE,"E3.1"),sQuery(id+"F0.wireOp",EDGE,"E3.2"),sQuery(id+"F0.wireOp",EDGE,"E3.4"),sQuery(id+"F0.wireOp",EDGE,"E3.5"),sQuery(id+"F0.wireOp",EDGE,"E11"),sQuery(id+"F0.wireOp",EDGE,"E12"),sQuery(id+"F0.wireOp",EDGE,"E13"),sQuery(id+"F0.wireOp",EDGE,"E14"),subQ1,subQ0,sQuery(id+"F0.wireOp",EDGE,"E17"),sQuery(id+"F0.wireOp",EDGE,"fGXXUOoa-G3to-nFfg-Xp41-Spi5BgRDYh0n"),sQuery(id+"F0.wireOp",EDGE,"maiLpuxs-2Sfq-8eKx-MEtN-jPa1VSy1aRe3"),sQuery(id+"F0.wireOp",EDGE,"E19"),sQuery(id+"F0.wireOp",EDGE,"TkPDQIJV-pblC-kMUo-zlvk-0mYhqbRm7784"),sQuery(id+"F0.wireOp",EDGE,"A3QQ103k-oBam-uK2f-Ywbn-FOsahd6y3kCF"),sQuery(id+"F0.wireOp",EDGE,"E22"),sQuery(id+"F0.wireOp",EDGE,"O4fUSGsA-sgfy-2hAb-lYRv-adjy5g4jnHMn"),sQuery(id+"F0.wireOp",EDGE,"he4H8z8F-eg87-8e6K-5810-5zuvFcfIEFNb")])],"isStart":false})]});}
            var Q12;
            Q12=makeQuery(id+"F1.opExtrude","CAP_EDGE",EDGE,{"disambiguationData":[OSD([sQuery(id+"F0.wireOp",EDGE,"E16")])],"isStart":false});
            var Q13;
            {var subQ0=sQuery(id+"F0.wireOp",EDGE,"E1.4");var subQ1=sQuery(id+"F0.wireOp",EDGE,"E1.3");Q13=makeQuery(id+"F11.opFillet","BLEND_EDGE",EDGE,{"blendedFrom":[makeQuery(id+"F1.opExtrude","SWEPT_EDGE",EDGE,{"disambiguationData":[OSD([subQ1,subQ0])]}),makeQuery(id+"F1.opExtrude","CAP_FACE",FACE,{"disambiguationData":[OSD([sQuery(id+"F0.wireOp",EDGE,"E0.0"),sQuery(id+"F0.wireOp",EDGE,"E0.2"),sQuery(id+"F0.wireOp",EDGE,"E0.4"),sQuery(id+"F0.wireOp",EDGE,"E1.0"),sQuery(id+"F0.wireOp",EDGE,"E1.2"),subQ1,subQ0,sQuery(id+"F0.wireOp",EDGE,"E1.5"),sQuery(id+"F0.wireOp",EDGE,"E2.0"),sQuery(id+"F0.wireOp",EDGE,"E2.1"),sQuery(id+"F0.wireOp",EDGE,"E2.2"),sQuery(id+"F0.wireOp",EDGE,"E2.3"),sQuery(id+"F0.wireOp",EDGE,"E2.4"),sQuery(id+"F0.wireOp",EDGE,"E3.0"),sQuery(id+"F0.wireOp",EDGE,"E3.1"),sQuery(id+"F0.wireOp",EDGE,"E3.2"),sQuery(id+"F0.wireOp",EDGE,"E3.4"),sQuery(id+"F0.wireOp",EDGE,"E3.5"),sQuery(id+"F0.wireOp",EDGE,"E11"),sQuery(id+"F0.wireOp",EDGE,"E12"),sQuery(id+"F0.wireOp",EDGE,"E13"),sQuery(id+"F0.wireOp",EDGE,"E14"),sQuery(id+"F0.wireOp",EDGE,"E15"),sQuery(id+"F0.wireOp",EDGE,"E16"),sQuery(id+"F0.wireOp",EDGE,"E17"),sQuery(id+"F0.wireOp",EDGE,"fGXXUOoa-G3to-nFfg-Xp41-Spi5BgRDYh0n"),sQuery(id+"F0.wireOp",EDGE,"maiLpuxs-2Sfq-8eKx-MEtN-jPa1VSy1aRe3"),sQuery(id+"F0.wireOp",EDGE,"E19"),sQuery(id+"F0.wireOp",EDGE,"TkPDQIJV-pblC-kMUo-zlvk-0mYhqbRm7784"),sQuery(id+"F0.wireOp",EDGE,"A3QQ103k-oBam-uK2f-Ywbn-FOsahd6y3kCF"),sQuery(id+"F0.wireOp",EDGE,"E22"),sQuery(id+"F0.wireOp",EDGE,"O4fUSGsA-sgfy-2hAb-lYRv-adjy5g4jnHMn"),sQuery(id+"F0.wireOp",EDGE,"he4H8z8F-eg87-8e6K-5810-5zuvFcfIEFNb")])],"isStart":false})],"blendedInto":[makeQuery(id+"F1.opExtrude","CAP_FACE",FACE,{"disambiguationData":[OSD([sQuery(id+"F0.wireOp",EDGE,"E0.0"),sQuery(id+"F0.wireOp",EDGE,"E0.2"),sQuery(id+"F0.wireOp",EDGE,"E0.4"),sQuery(id+"F0.wireOp",EDGE,"E1.0"),sQuery(id+"F0.wireOp",EDGE,"E1.2"),subQ1,subQ0,sQuery(id+"F0.wireOp",EDGE,"E1.5"),sQuery(id+"F0.wireOp",EDGE,"E2.0"),sQuery(id+"F0.wireOp",EDGE,"E2.1"),sQuery(id+"F0.wireOp",EDGE,"E2.2"),sQuery(id+"F0.wireOp",EDGE,"E2.3"),sQuery(id+"F0.wireOp",EDGE,"E2.4"),sQuery(id+"F0.wireOp",EDGE,"E3.0"),sQuery(id+"F0.wireOp",EDGE,"E3.1"),sQuery(id+"F0.wireOp",EDGE,"E3.2"),sQuery(id+"F0.wireOp",EDGE,"E3.4"),sQuery(id+"F0.wireOp",EDGE,"E3.5"),sQuery(id+"F0.wireOp",EDGE,"E11"),sQuery(id+"F0.wireOp",EDGE,"E12"),sQuery(id+"F0.wireOp",EDGE,"E13"),sQuery(id+"F0.wireOp",EDGE,"E14"),sQuery(id+"F0.wireOp",EDGE,"E15"),sQuery(id+"F0.wireOp",EDGE,"E16"),sQuery(id+"F0.wireOp",EDGE,"E17"),sQuery(id+"F0.wireOp",EDGE,"fGXXUOoa-G3to-nFfg-Xp41-Spi5BgRDYh0n"),sQuery(id+"F0.wireOp",EDGE,"maiLpuxs-2Sfq-8eKx-MEtN-jPa1VSy1aRe3"),sQuery(id+"F0.wireOp",EDGE,"E19"),sQuery(id+"F0.wireOp",EDGE,"TkPDQIJV-pblC-kMUo-zlvk-0mYhqbRm7784"),sQuery(id+"F0.wireOp",EDGE,"A3QQ103k-oBam-uK2f-Ywbn-FOsahd6y3kCF"),sQuery(id+"F0.wireOp",EDGE,"E22"),sQuery(id+"F0.wireOp",EDGE,"O4fUSGsA-sgfy-2hAb-lYRv-adjy5g4jnHMn"),sQuery(id+"F0.wireOp",EDGE,"he4H8z8F-eg87-8e6K-5810-5zuvFcfIEFNb")])],"isStart":false})]});}
            var Q14;
            Q14=makeQuery(id+"F1.opExtrude","CAP_EDGE",EDGE,{"disambiguationData":[OSD([sQuery(id+"F0.wireOp",EDGE,"E1.3")])],"isStart":false});
            var Q15;
            Q15=makeQuery(id+"F1.opExtrude","CAP_EDGE",EDGE,{"disambiguationData":[OSD([sQuery(id+"F0.wireOp",EDGE,"E1.4")])],"isStart":false});
            var Q16;
            {var subQ0=sQuery(id+"F0.wireOp",EDGE,"E1.5");var subQ1=sQuery(id+"F0.wireOp",EDGE,"E1.4");Q16=makeQuery(id+"F11.opFillet","BLEND_EDGE",EDGE,{"blendedFrom":[makeQuery(id+"F1.opExtrude","SWEPT_EDGE",EDGE,{"disambiguationData":[OSD([subQ1,subQ0])]}),makeQuery(id+"F1.opExtrude","CAP_FACE",FACE,{"disambiguationData":[OSD([sQuery(id+"F0.wireOp",EDGE,"E0.0"),sQuery(id+"F0.wireOp",EDGE,"E0.2"),sQuery(id+"F0.wireOp",EDGE,"E0.4"),sQuery(id+"F0.wireOp",EDGE,"E1.0"),sQuery(id+"F0.wireOp",EDGE,"E1.2"),sQuery(id+"F0.wireOp",EDGE,"E1.3"),subQ1,subQ0,sQuery(id+"F0.wireOp",EDGE,"E2.0"),sQuery(id+"F0.wireOp",EDGE,"E2.1"),sQuery(id+"F0.wireOp",EDGE,"E2.2"),sQuery(id+"F0.wireOp",EDGE,"E2.3"),sQuery(id+"F0.wireOp",EDGE,"E2.4"),sQuery(id+"F0.wireOp",EDGE,"E3.0"),sQuery(id+"F0.wireOp",EDGE,"E3.1"),sQuery(id+"F0.wireOp",EDGE,"E3.2"),sQuery(id+"F0.wireOp",EDGE,"E3.4"),sQuery(id+"F0.wireOp",EDGE,"E3.5"),sQuery(id+"F0.wireOp",EDGE,"E11"),sQuery(id+"F0.wireOp",EDGE,"E12"),sQuery(id+"F0.wireOp",EDGE,"E13"),sQuery(id+"F0.wireOp",EDGE,"E14"),sQuery(id+"F0.wireOp",EDGE,"E15"),sQuery(id+"F0.wireOp",EDGE,"E16"),sQuery(id+"F0.wireOp",EDGE,"E17"),sQuery(id+"F0.wireOp",EDGE,"fGXXUOoa-G3to-nFfg-Xp41-Spi5BgRDYh0n"),sQuery(id+"F0.wireOp",EDGE,"maiLpuxs-2Sfq-8eKx-MEtN-jPa1VSy1aRe3"),sQuery(id+"F0.wireOp",EDGE,"E19"),sQuery(id+"F0.wireOp",EDGE,"TkPDQIJV-pblC-kMUo-zlvk-0mYhqbRm7784"),sQuery(id+"F0.wireOp",EDGE,"A3QQ103k-oBam-uK2f-Ywbn-FOsahd6y3kCF"),sQuery(id+"F0.wireOp",EDGE,"E22"),sQuery(id+"F0.wireOp",EDGE,"O4fUSGsA-sgfy-2hAb-lYRv-adjy5g4jnHMn"),sQuery(id+"F0.wireOp",EDGE,"he4H8z8F-eg87-8e6K-5810-5zuvFcfIEFNb")])],"isStart":false})],"blendedInto":[makeQuery(id+"F1.opExtrude","CAP_FACE",FACE,{"disambiguationData":[OSD([sQuery(id+"F0.wireOp",EDGE,"E0.0"),sQuery(id+"F0.wireOp",EDGE,"E0.2"),sQuery(id+"F0.wireOp",EDGE,"E0.4"),sQuery(id+"F0.wireOp",EDGE,"E1.0"),sQuery(id+"F0.wireOp",EDGE,"E1.2"),sQuery(id+"F0.wireOp",EDGE,"E1.3"),subQ1,subQ0,sQuery(id+"F0.wireOp",EDGE,"E2.0"),sQuery(id+"F0.wireOp",EDGE,"E2.1"),sQuery(id+"F0.wireOp",EDGE,"E2.2"),sQuery(id+"F0.wireOp",EDGE,"E2.3"),sQuery(id+"F0.wireOp",EDGE,"E2.4"),sQuery(id+"F0.wireOp",EDGE,"E3.0"),sQuery(id+"F0.wireOp",EDGE,"E3.1"),sQuery(id+"F0.wireOp",EDGE,"E3.2"),sQuery(id+"F0.wireOp",EDGE,"E3.4"),sQuery(id+"F0.wireOp",EDGE,"E3.5"),sQuery(id+"F0.wireOp",EDGE,"E11"),sQuery(id+"F0.wireOp",EDGE,"E12"),sQuery(id+"F0.wireOp",EDGE,"E13"),sQuery(id+"F0.wireOp",EDGE,"E14"),sQuery(id+"F0.wireOp",EDGE,"E15"),sQuery(id+"F0.wireOp",EDGE,"E16"),sQuery(id+"F0.wireOp",EDGE,"E17"),sQuery(id+"F0.wireOp",EDGE,"fGXXUOoa-G3to-nFfg-Xp41-Spi5BgRDYh0n"),sQuery(id+"F0.wireOp",EDGE,"maiLpuxs-2Sfq-8eKx-MEtN-jPa1VSy1aRe3"),sQuery(id+"F0.wireOp",EDGE,"E19"),sQuery(id+"F0.wireOp",EDGE,"TkPDQIJV-pblC-kMUo-zlvk-0mYhqbRm7784"),sQuery(id+"F0.wireOp",EDGE,"A3QQ103k-oBam-uK2f-Ywbn-FOsahd6y3kCF"),sQuery(id+"F0.wireOp",EDGE,"E22"),sQuery(id+"F0.wireOp",EDGE,"O4fUSGsA-sgfy-2hAb-lYRv-adjy5g4jnHMn"),sQuery(id+"F0.wireOp",EDGE,"he4H8z8F-eg87-8e6K-5810-5zuvFcfIEFNb")])],"isStart":false})]});}
            var Q17;
            {var subQ0=sQuery(id+"F0.wireOp",EDGE,"E1.5");var subQ1=sQuery(id+"F0.wireOp",EDGE,"E1.0");Q17=makeQuery(id+"F11.opFillet","BLEND_EDGE",EDGE,{"blendedFrom":[makeQuery(id+"F1.opExtrude","SWEPT_EDGE",EDGE,{"disambiguationData":[OSD([subQ1,subQ0])]}),makeQuery(id+"F1.opExtrude","CAP_FACE",FACE,{"disambiguationData":[OSD([sQuery(id+"F0.wireOp",EDGE,"E0.0"),sQuery(id+"F0.wireOp",EDGE,"E0.2"),sQuery(id+"F0.wireOp",EDGE,"E0.4"),subQ1,sQuery(id+"F0.wireOp",EDGE,"E1.2"),sQuery(id+"F0.wireOp",EDGE,"E1.3"),sQuery(id+"F0.wireOp",EDGE,"E1.4"),subQ0,sQuery(id+"F0.wireOp",EDGE,"E2.0"),sQuery(id+"F0.wireOp",EDGE,"E2.1"),sQuery(id+"F0.wireOp",EDGE,"E2.2"),sQuery(id+"F0.wireOp",EDGE,"E2.3"),sQuery(id+"F0.wireOp",EDGE,"E2.4"),sQuery(id+"F0.wireOp",EDGE,"E3.0"),sQuery(id+"F0.wireOp",EDGE,"E3.1"),sQuery(id+"F0.wireOp",EDGE,"E3.2"),sQuery(id+"F0.wireOp",EDGE,"E3.4"),sQuery(id+"F0.wireOp",EDGE,"E3.5"),sQuery(id+"F0.wireOp",EDGE,"E11"),sQuery(id+"F0.wireOp",EDGE,"E12"),sQuery(id+"F0.wireOp",EDGE,"E13"),sQuery(id+"F0.wireOp",EDGE,"E14"),sQuery(id+"F0.wireOp",EDGE,"E15"),sQuery(id+"F0.wireOp",EDGE,"E16"),sQuery(id+"F0.wireOp",EDGE,"E17"),sQuery(id+"F0.wireOp",EDGE,"fGXXUOoa-G3to-nFfg-Xp41-Spi5BgRDYh0n"),sQuery(id+"F0.wireOp",EDGE,"maiLpuxs-2Sfq-8eKx-MEtN-jPa1VSy1aRe3"),sQuery(id+"F0.wireOp",EDGE,"E19"),sQuery(id+"F0.wireOp",EDGE,"TkPDQIJV-pblC-kMUo-zlvk-0mYhqbRm7784"),sQuery(id+"F0.wireOp",EDGE,"A3QQ103k-oBam-uK2f-Ywbn-FOsahd6y3kCF"),sQuery(id+"F0.wireOp",EDGE,"E22"),sQuery(id+"F0.wireOp",EDGE,"O4fUSGsA-sgfy-2hAb-lYRv-adjy5g4jnHMn"),sQuery(id+"F0.wireOp",EDGE,"he4H8z8F-eg87-8e6K-5810-5zuvFcfIEFNb")])],"isStart":false})],"blendedInto":[makeQuery(id+"F1.opExtrude","CAP_FACE",FACE,{"disambiguationData":[OSD([sQuery(id+"F0.wireOp",EDGE,"E0.0"),sQuery(id+"F0.wireOp",EDGE,"E0.2"),sQuery(id+"F0.wireOp",EDGE,"E0.4"),subQ1,sQuery(id+"F0.wireOp",EDGE,"E1.2"),sQuery(id+"F0.wireOp",EDGE,"E1.3"),sQuery(id+"F0.wireOp",EDGE,"E1.4"),subQ0,sQuery(id+"F0.wireOp",EDGE,"E2.0"),sQuery(id+"F0.wireOp",EDGE,"E2.1"),sQuery(id+"F0.wireOp",EDGE,"E2.2"),sQuery(id+"F0.wireOp",EDGE,"E2.3"),sQuery(id+"F0.wireOp",EDGE,"E2.4"),sQuery(id+"F0.wireOp",EDGE,"E3.0"),sQuery(id+"F0.wireOp",EDGE,"E3.1"),sQuery(id+"F0.wireOp",EDGE,"E3.2"),sQuery(id+"F0.wireOp",EDGE,"E3.4"),sQuery(id+"F0.wireOp",EDGE,"E3.5"),sQuery(id+"F0.wireOp",EDGE,"E11"),sQuery(id+"F0.wireOp",EDGE,"E12"),sQuery(id+"F0.wireOp",EDGE,"E13"),sQuery(id+"F0.wireOp",EDGE,"E14"),sQuery(id+"F0.wireOp",EDGE,"E15"),sQuery(id+"F0.wireOp",EDGE,"E16"),sQuery(id+"F0.wireOp",EDGE,"E17"),sQuery(id+"F0.wireOp",EDGE,"fGXXUOoa-G3to-nFfg-Xp41-Spi5BgRDYh0n"),sQuery(id+"F0.wireOp",EDGE,"maiLpuxs-2Sfq-8eKx-MEtN-jPa1VSy1aRe3"),sQuery(id+"F0.wireOp",EDGE,"E19"),sQuery(id+"F0.wireOp",EDGE,"TkPDQIJV-pblC-kMUo-zlvk-0mYhqbRm7784"),sQuery(id+"F0.wireOp",EDGE,"A3QQ103k-oBam-uK2f-Ywbn-FOsahd6y3kCF"),sQuery(id+"F0.wireOp",EDGE,"E22"),sQuery(id+"F0.wireOp",EDGE,"O4fUSGsA-sgfy-2hAb-lYRv-adjy5g4jnHMn"),sQuery(id+"F0.wireOp",EDGE,"he4H8z8F-eg87-8e6K-5810-5zuvFcfIEFNb")])],"isStart":false})]});}
            var Q18;
            Q18=makeQuery(id+"F1.opExtrude","CAP_EDGE",EDGE,{"disambiguationData":[OSD([sQuery(id+"F0.wireOp",EDGE,"E1.5")])],"isStart":false});
            var Q19;
            Q19=makeQuery(id+"F1.opExtrude","CAP_EDGE",EDGE,{"disambiguationData":[OSD([sQuery(id+"F0.wireOp",EDGE,"E1.0")])],"isStart":false});
            var Q20;
            {var subQ0=sQuery(id+"F0.wireOp",EDGE,"E1.0");var subQ1=sQuery(id+"F0.wireOp",EDGE,"E0.0");Q20=makeQuery(id+"F11.opFillet","BLEND_EDGE",EDGE,{"blendedFrom":[makeQuery(id+"F1.opExtrude","SWEPT_EDGE",EDGE,{"disambiguationData":[OSD([subQ1,subQ0,sQuery(id+"F0.wireOp",EDGE,"E1.1")])]}),makeQuery(id+"F1.opExtrude","CAP_FACE",FACE,{"disambiguationData":[OSD([subQ1,sQuery(id+"F0.wireOp",EDGE,"E0.2"),sQuery(id+"F0.wireOp",EDGE,"E0.4"),subQ0,sQuery(id+"F0.wireOp",EDGE,"E1.2"),sQuery(id+"F0.wireOp",EDGE,"E1.3"),sQuery(id+"F0.wireOp",EDGE,"E1.4"),sQuery(id+"F0.wireOp",EDGE,"E1.5"),sQuery(id+"F0.wireOp",EDGE,"E2.0"),sQuery(id+"F0.wireOp",EDGE,"E2.1"),sQuery(id+"F0.wireOp",EDGE,"E2.2"),sQuery(id+"F0.wireOp",EDGE,"E2.3"),sQuery(id+"F0.wireOp",EDGE,"E2.4"),sQuery(id+"F0.wireOp",EDGE,"E3.0"),sQuery(id+"F0.wireOp",EDGE,"E3.1"),sQuery(id+"F0.wireOp",EDGE,"E3.2"),sQuery(id+"F0.wireOp",EDGE,"E3.4"),sQuery(id+"F0.wireOp",EDGE,"E3.5"),sQuery(id+"F0.wireOp",EDGE,"E11"),sQuery(id+"F0.wireOp",EDGE,"E12"),sQuery(id+"F0.wireOp",EDGE,"E13"),sQuery(id+"F0.wireOp",EDGE,"E14"),sQuery(id+"F0.wireOp",EDGE,"E15"),sQuery(id+"F0.wireOp",EDGE,"E16"),sQuery(id+"F0.wireOp",EDGE,"E17"),sQuery(id+"F0.wireOp",EDGE,"fGXXUOoa-G3to-nFfg-Xp41-Spi5BgRDYh0n"),sQuery(id+"F0.wireOp",EDGE,"maiLpuxs-2Sfq-8eKx-MEtN-jPa1VSy1aRe3"),sQuery(id+"F0.wireOp",EDGE,"E19"),sQuery(id+"F0.wireOp",EDGE,"TkPDQIJV-pblC-kMUo-zlvk-0mYhqbRm7784"),sQuery(id+"F0.wireOp",EDGE,"A3QQ103k-oBam-uK2f-Ywbn-FOsahd6y3kCF"),sQuery(id+"F0.wireOp",EDGE,"E22"),sQuery(id+"F0.wireOp",EDGE,"O4fUSGsA-sgfy-2hAb-lYRv-adjy5g4jnHMn"),sQuery(id+"F0.wireOp",EDGE,"he4H8z8F-eg87-8e6K-5810-5zuvFcfIEFNb")])],"isStart":false})],"blendedInto":[makeQuery(id+"F1.opExtrude","CAP_FACE",FACE,{"disambiguationData":[OSD([subQ1,sQuery(id+"F0.wireOp",EDGE,"E0.2"),sQuery(id+"F0.wireOp",EDGE,"E0.4"),subQ0,sQuery(id+"F0.wireOp",EDGE,"E1.2"),sQuery(id+"F0.wireOp",EDGE,"E1.3"),sQuery(id+"F0.wireOp",EDGE,"E1.4"),sQuery(id+"F0.wireOp",EDGE,"E1.5"),sQuery(id+"F0.wireOp",EDGE,"E2.0"),sQuery(id+"F0.wireOp",EDGE,"E2.1"),sQuery(id+"F0.wireOp",EDGE,"E2.2"),sQuery(id+"F0.wireOp",EDGE,"E2.3"),sQuery(id+"F0.wireOp",EDGE,"E2.4"),sQuery(id+"F0.wireOp",EDGE,"E3.0"),sQuery(id+"F0.wireOp",EDGE,"E3.1"),sQuery(id+"F0.wireOp",EDGE,"E3.2"),sQuery(id+"F0.wireOp",EDGE,"E3.4"),sQuery(id+"F0.wireOp",EDGE,"E3.5"),sQuery(id+"F0.wireOp",EDGE,"E11"),sQuery(id+"F0.wireOp",EDGE,"E12"),sQuery(id+"F0.wireOp",EDGE,"E13"),sQuery(id+"F0.wireOp",EDGE,"E14"),sQuery(id+"F0.wireOp",EDGE,"E15"),sQuery(id+"F0.wireOp",EDGE,"E16"),sQuery(id+"F0.wireOp",EDGE,"E17"),sQuery(id+"F0.wireOp",EDGE,"fGXXUOoa-G3to-nFfg-Xp41-Spi5BgRDYh0n"),sQuery(id+"F0.wireOp",EDGE,"maiLpuxs-2Sfq-8eKx-MEtN-jPa1VSy1aRe3"),sQuery(id+"F0.wireOp",EDGE,"E19"),sQuery(id+"F0.wireOp",EDGE,"TkPDQIJV-pblC-kMUo-zlvk-0mYhqbRm7784"),sQuery(id+"F0.wireOp",EDGE,"A3QQ103k-oBam-uK2f-Ywbn-FOsahd6y3kCF"),sQuery(id+"F0.wireOp",EDGE,"E22"),sQuery(id+"F0.wireOp",EDGE,"O4fUSGsA-sgfy-2hAb-lYRv-adjy5g4jnHMn"),sQuery(id+"F0.wireOp",EDGE,"he4H8z8F-eg87-8e6K-5810-5zuvFcfIEFNb")])],"isStart":false})]});}
            var Q21;
            Q21=makeQuery(id+"F1.opExtrude","CAP_EDGE",EDGE,{"disambiguationData":[OSD([sQuery(id+"F0.wireOp",EDGE,"E0.0")])],"isStart":false});
            var Q22;
            {var subQ0=sQuery(id+"F0.wireOp",EDGE,"E3.4");var subQ1=sQuery(id+"F0.wireOp",EDGE,"E0.0");Q22=makeQuery(id+"F11.opFillet","BLEND_EDGE",EDGE,{"blendedFrom":[makeQuery(id+"F1.opExtrude","SWEPT_EDGE",EDGE,{"disambiguationData":[OSD([subQ1,subQ0])]}),makeQuery(id+"F1.opExtrude","CAP_FACE",FACE,{"disambiguationData":[OSD([subQ1,sQuery(id+"F0.wireOp",EDGE,"E0.2"),sQuery(id+"F0.wireOp",EDGE,"E0.4"),sQuery(id+"F0.wireOp",EDGE,"E1.0"),sQuery(id+"F0.wireOp",EDGE,"E1.2"),sQuery(id+"F0.wireOp",EDGE,"E1.3"),sQuery(id+"F0.wireOp",EDGE,"E1.4"),sQuery(id+"F0.wireOp",EDGE,"E1.5"),sQuery(id+"F0.wireOp",EDGE,"E2.0"),sQuery(id+"F0.wireOp",EDGE,"E2.1"),sQuery(id+"F0.wireOp",EDGE,"E2.2"),sQuery(id+"F0.wireOp",EDGE,"E2.3"),sQuery(id+"F0.wireOp",EDGE,"E2.4"),sQuery(id+"F0.wireOp",EDGE,"E3.0"),sQuery(id+"F0.wireOp",EDGE,"E3.1"),sQuery(id+"F0.wireOp",EDGE,"E3.2"),subQ0,sQuery(id+"F0.wireOp",EDGE,"E3.5"),sQuery(id+"F0.wireOp",EDGE,"E11"),sQuery(id+"F0.wireOp",EDGE,"E12"),sQuery(id+"F0.wireOp",EDGE,"E13"),sQuery(id+"F0.wireOp",EDGE,"E14"),sQuery(id+"F0.wireOp",EDGE,"E15"),sQuery(id+"F0.wireOp",EDGE,"E16"),sQuery(id+"F0.wireOp",EDGE,"E17"),sQuery(id+"F0.wireOp",EDGE,"fGXXUOoa-G3to-nFfg-Xp41-Spi5BgRDYh0n"),sQuery(id+"F0.wireOp",EDGE,"maiLpuxs-2Sfq-8eKx-MEtN-jPa1VSy1aRe3"),sQuery(id+"F0.wireOp",EDGE,"E19"),sQuery(id+"F0.wireOp",EDGE,"TkPDQIJV-pblC-kMUo-zlvk-0mYhqbRm7784"),sQuery(id+"F0.wireOp",EDGE,"A3QQ103k-oBam-uK2f-Ywbn-FOsahd6y3kCF"),sQuery(id+"F0.wireOp",EDGE,"E22"),sQuery(id+"F0.wireOp",EDGE,"O4fUSGsA-sgfy-2hAb-lYRv-adjy5g4jnHMn"),sQuery(id+"F0.wireOp",EDGE,"he4H8z8F-eg87-8e6K-5810-5zuvFcfIEFNb")])],"isStart":false})],"blendedInto":[makeQuery(id+"F1.opExtrude","CAP_FACE",FACE,{"disambiguationData":[OSD([subQ1,sQuery(id+"F0.wireOp",EDGE,"E0.2"),sQuery(id+"F0.wireOp",EDGE,"E0.4"),sQuery(id+"F0.wireOp",EDGE,"E1.0"),sQuery(id+"F0.wireOp",EDGE,"E1.2"),sQuery(id+"F0.wireOp",EDGE,"E1.3"),sQuery(id+"F0.wireOp",EDGE,"E1.4"),sQuery(id+"F0.wireOp",EDGE,"E1.5"),sQuery(id+"F0.wireOp",EDGE,"E2.0"),sQuery(id+"F0.wireOp",EDGE,"E2.1"),sQuery(id+"F0.wireOp",EDGE,"E2.2"),sQuery(id+"F0.wireOp",EDGE,"E2.3"),sQuery(id+"F0.wireOp",EDGE,"E2.4"),sQuery(id+"F0.wireOp",EDGE,"E3.0"),sQuery(id+"F0.wireOp",EDGE,"E3.1"),sQuery(id+"F0.wireOp",EDGE,"E3.2"),subQ0,sQuery(id+"F0.wireOp",EDGE,"E3.5"),sQuery(id+"F0.wireOp",EDGE,"E11"),sQuery(id+"F0.wireOp",EDGE,"E12"),sQuery(id+"F0.wireOp",EDGE,"E13"),sQuery(id+"F0.wireOp",EDGE,"E14"),sQuery(id+"F0.wireOp",EDGE,"E15"),sQuery(id+"F0.wireOp",EDGE,"E16"),sQuery(id+"F0.wireOp",EDGE,"E17"),sQuery(id+"F0.wireOp",EDGE,"fGXXUOoa-G3to-nFfg-Xp41-Spi5BgRDYh0n"),sQuery(id+"F0.wireOp",EDGE,"maiLpuxs-2Sfq-8eKx-MEtN-jPa1VSy1aRe3"),sQuery(id+"F0.wireOp",EDGE,"E19"),sQuery(id+"F0.wireOp",EDGE,"TkPDQIJV-pblC-kMUo-zlvk-0mYhqbRm7784"),sQuery(id+"F0.wireOp",EDGE,"A3QQ103k-oBam-uK2f-Ywbn-FOsahd6y3kCF"),sQuery(id+"F0.wireOp",EDGE,"E22"),sQuery(id+"F0.wireOp",EDGE,"O4fUSGsA-sgfy-2hAb-lYRv-adjy5g4jnHMn"),sQuery(id+"F0.wireOp",EDGE,"he4H8z8F-eg87-8e6K-5810-5zuvFcfIEFNb")])],"isStart":false})]});}
            var Q23;
            Q23=makeQuery(id+"F1.opExtrude","CAP_EDGE",EDGE,{"disambiguationData":[OSD([sQuery(id+"F0.wireOp",EDGE,"E3.4")])],"isStart":false});
            var Q24;
            Q24=makeQuery(id+"F1.opExtrude","CAP_EDGE",EDGE,{"disambiguationData":[OSD([sQuery(id+"F0.wireOp",EDGE,"E13")])],"isStart":false});
            var Q25;
            {var subQ0=sQuery(id+"F0.wireOp",EDGE,"E14");var subQ1=sQuery(id+"F0.wireOp",EDGE,"E13");Q25=makeQuery(id+"F12.opFillet","BLEND_EDGE",EDGE,{"blendedFrom":[makeQuery(id+"F1.opExtrude","SWEPT_EDGE",EDGE,{"disambiguationData":[OSD([sQuery(id+"F0.wireOp",EDGE,"E10"),subQ1,subQ0])]}),makeQuery(id+"F1.opExtrude","CAP_FACE",FACE,{"disambiguationData":[OSD([sQuery(id+"F0.wireOp",EDGE,"E0.0"),sQuery(id+"F0.wireOp",EDGE,"E0.2"),sQuery(id+"F0.wireOp",EDGE,"E0.4"),sQuery(id+"F0.wireOp",EDGE,"E1.0"),sQuery(id+"F0.wireOp",EDGE,"E1.2"),sQuery(id+"F0.wireOp",EDGE,"E1.3"),sQuery(id+"F0.wireOp",EDGE,"E1.4"),sQuery(id+"F0.wireOp",EDGE,"E1.5"),sQuery(id+"F0.wireOp",EDGE,"E2.0"),sQuery(id+"F0.wireOp",EDGE,"E2.1"),sQuery(id+"F0.wireOp",EDGE,"E2.2"),sQuery(id+"F0.wireOp",EDGE,"E2.3"),sQuery(id+"F0.wireOp",EDGE,"E2.4"),sQuery(id+"F0.wireOp",EDGE,"E3.0"),sQuery(id+"F0.wireOp",EDGE,"E3.1"),sQuery(id+"F0.wireOp",EDGE,"E3.2"),sQuery(id+"F0.wireOp",EDGE,"E3.4"),sQuery(id+"F0.wireOp",EDGE,"E3.5"),sQuery(id+"F0.wireOp",EDGE,"E11"),sQuery(id+"F0.wireOp",EDGE,"E12"),subQ1,subQ0,sQuery(id+"F0.wireOp",EDGE,"E15"),sQuery(id+"F0.wireOp",EDGE,"E16"),sQuery(id+"F0.wireOp",EDGE,"E17"),sQuery(id+"F0.wireOp",EDGE,"fGXXUOoa-G3to-nFfg-Xp41-Spi5BgRDYh0n"),sQuery(id+"F0.wireOp",EDGE,"maiLpuxs-2Sfq-8eKx-MEtN-jPa1VSy1aRe3"),sQuery(id+"F0.wireOp",EDGE,"E19"),sQuery(id+"F0.wireOp",EDGE,"TkPDQIJV-pblC-kMUo-zlvk-0mYhqbRm7784"),sQuery(id+"F0.wireOp",EDGE,"A3QQ103k-oBam-uK2f-Ywbn-FOsahd6y3kCF"),sQuery(id+"F0.wireOp",EDGE,"E22"),sQuery(id+"F0.wireOp",EDGE,"O4fUSGsA-sgfy-2hAb-lYRv-adjy5g4jnHMn"),sQuery(id+"F0.wireOp",EDGE,"he4H8z8F-eg87-8e6K-5810-5zuvFcfIEFNb")])],"isStart":false})],"blendedInto":[makeQuery(id+"F1.opExtrude","CAP_FACE",FACE,{"disambiguationData":[OSD([sQuery(id+"F0.wireOp",EDGE,"E0.0"),sQuery(id+"F0.wireOp",EDGE,"E0.2"),sQuery(id+"F0.wireOp",EDGE,"E0.4"),sQuery(id+"F0.wireOp",EDGE,"E1.0"),sQuery(id+"F0.wireOp",EDGE,"E1.2"),sQuery(id+"F0.wireOp",EDGE,"E1.3"),sQuery(id+"F0.wireOp",EDGE,"E1.4"),sQuery(id+"F0.wireOp",EDGE,"E1.5"),sQuery(id+"F0.wireOp",EDGE,"E2.0"),sQuery(id+"F0.wireOp",EDGE,"E2.1"),sQuery(id+"F0.wireOp",EDGE,"E2.2"),sQuery(id+"F0.wireOp",EDGE,"E2.3"),sQuery(id+"F0.wireOp",EDGE,"E2.4"),sQuery(id+"F0.wireOp",EDGE,"E3.0"),sQuery(id+"F0.wireOp",EDGE,"E3.1"),sQuery(id+"F0.wireOp",EDGE,"E3.2"),sQuery(id+"F0.wireOp",EDGE,"E3.4"),sQuery(id+"F0.wireOp",EDGE,"E3.5"),sQuery(id+"F0.wireOp",EDGE,"E11"),sQuery(id+"F0.wireOp",EDGE,"E12"),subQ1,subQ0,sQuery(id+"F0.wireOp",EDGE,"E15"),sQuery(id+"F0.wireOp",EDGE,"E16"),sQuery(id+"F0.wireOp",EDGE,"E17"),sQuery(id+"F0.wireOp",EDGE,"fGXXUOoa-G3to-nFfg-Xp41-Spi5BgRDYh0n"),sQuery(id+"F0.wireOp",EDGE,"maiLpuxs-2Sfq-8eKx-MEtN-jPa1VSy1aRe3"),sQuery(id+"F0.wireOp",EDGE,"E19"),sQuery(id+"F0.wireOp",EDGE,"TkPDQIJV-pblC-kMUo-zlvk-0mYhqbRm7784"),sQuery(id+"F0.wireOp",EDGE,"A3QQ103k-oBam-uK2f-Ywbn-FOsahd6y3kCF"),sQuery(id+"F0.wireOp",EDGE,"E22"),sQuery(id+"F0.wireOp",EDGE,"O4fUSGsA-sgfy-2hAb-lYRv-adjy5g4jnHMn"),sQuery(id+"F0.wireOp",EDGE,"he4H8z8F-eg87-8e6K-5810-5zuvFcfIEFNb")])],"isStart":false})]});}
            var Q26;
            Q26=makeQuery(id+"F1.opExtrude","CAP_EDGE",EDGE,{"disambiguationData":[OSD([sQuery(id+"F0.wireOp",EDGE,"E14")])],"isStart":false});
            var Q27;
            {var subQ0=sQuery(id+"F0.wireOp",EDGE,"E3.5");var subQ1=sQuery(id+"F0.wireOp",EDGE,"E3.0");Q27=makeQuery(id+"F11.opFillet","BLEND_EDGE",EDGE,{"blendedFrom":[makeQuery(id+"F1.opExtrude","SWEPT_EDGE",EDGE,{"disambiguationData":[OSD([subQ1,subQ0])]}),makeQuery(id+"F1.opExtrude","CAP_FACE",FACE,{"disambiguationData":[OSD([sQuery(id+"F0.wireOp",EDGE,"E0.0"),sQuery(id+"F0.wireOp",EDGE,"E0.2"),sQuery(id+"F0.wireOp",EDGE,"E0.4"),sQuery(id+"F0.wireOp",EDGE,"E1.0"),sQuery(id+"F0.wireOp",EDGE,"E1.2"),sQuery(id+"F0.wireOp",EDGE,"E1.3"),sQuery(id+"F0.wireOp",EDGE,"E1.4"),sQuery(id+"F0.wireOp",EDGE,"E1.5"),sQuery(id+"F0.wireOp",EDGE,"E2.0"),sQuery(id+"F0.wireOp",EDGE,"E2.1"),sQuery(id+"F0.wireOp",EDGE,"E2.2"),sQuery(id+"F0.wireOp",EDGE,"E2.3"),sQuery(id+"F0.wireOp",EDGE,"E2.4"),subQ1,sQuery(id+"F0.wireOp",EDGE,"E3.1"),sQuery(id+"F0.wireOp",EDGE,"E3.2"),sQuery(id+"F0.wireOp",EDGE,"E3.4"),subQ0,sQuery(id+"F0.wireOp",EDGE,"E11"),sQuery(id+"F0.wireOp",EDGE,"E12"),sQuery(id+"F0.wireOp",EDGE,"E13"),sQuery(id+"F0.wireOp",EDGE,"E14"),sQuery(id+"F0.wireOp",EDGE,"E15"),sQuery(id+"F0.wireOp",EDGE,"E16"),sQuery(id+"F0.wireOp",EDGE,"E17"),sQuery(id+"F0.wireOp",EDGE,"fGXXUOoa-G3to-nFfg-Xp41-Spi5BgRDYh0n"),sQuery(id+"F0.wireOp",EDGE,"maiLpuxs-2Sfq-8eKx-MEtN-jPa1VSy1aRe3"),sQuery(id+"F0.wireOp",EDGE,"E19"),sQuery(id+"F0.wireOp",EDGE,"TkPDQIJV-pblC-kMUo-zlvk-0mYhqbRm7784"),sQuery(id+"F0.wireOp",EDGE,"A3QQ103k-oBam-uK2f-Ywbn-FOsahd6y3kCF"),sQuery(id+"F0.wireOp",EDGE,"E22"),sQuery(id+"F0.wireOp",EDGE,"O4fUSGsA-sgfy-2hAb-lYRv-adjy5g4jnHMn"),sQuery(id+"F0.wireOp",EDGE,"he4H8z8F-eg87-8e6K-5810-5zuvFcfIEFNb")])],"isStart":false})],"blendedInto":[makeQuery(id+"F1.opExtrude","CAP_FACE",FACE,{"disambiguationData":[OSD([sQuery(id+"F0.wireOp",EDGE,"E0.0"),sQuery(id+"F0.wireOp",EDGE,"E0.2"),sQuery(id+"F0.wireOp",EDGE,"E0.4"),sQuery(id+"F0.wireOp",EDGE,"E1.0"),sQuery(id+"F0.wireOp",EDGE,"E1.2"),sQuery(id+"F0.wireOp",EDGE,"E1.3"),sQuery(id+"F0.wireOp",EDGE,"E1.4"),sQuery(id+"F0.wireOp",EDGE,"E1.5"),sQuery(id+"F0.wireOp",EDGE,"E2.0"),sQuery(id+"F0.wireOp",EDGE,"E2.1"),sQuery(id+"F0.wireOp",EDGE,"E2.2"),sQuery(id+"F0.wireOp",EDGE,"E2.3"),sQuery(id+"F0.wireOp",EDGE,"E2.4"),subQ1,sQuery(id+"F0.wireOp",EDGE,"E3.1"),sQuery(id+"F0.wireOp",EDGE,"E3.2"),sQuery(id+"F0.wireOp",EDGE,"E3.4"),subQ0,sQuery(id+"F0.wireOp",EDGE,"E11"),sQuery(id+"F0.wireOp",EDGE,"E12"),sQuery(id+"F0.wireOp",EDGE,"E13"),sQuery(id+"F0.wireOp",EDGE,"E14"),sQuery(id+"F0.wireOp",EDGE,"E15"),sQuery(id+"F0.wireOp",EDGE,"E16"),sQuery(id+"F0.wireOp",EDGE,"E17"),sQuery(id+"F0.wireOp",EDGE,"fGXXUOoa-G3to-nFfg-Xp41-Spi5BgRDYh0n"),sQuery(id+"F0.wireOp",EDGE,"maiLpuxs-2Sfq-8eKx-MEtN-jPa1VSy1aRe3"),sQuery(id+"F0.wireOp",EDGE,"E19"),sQuery(id+"F0.wireOp",EDGE,"TkPDQIJV-pblC-kMUo-zlvk-0mYhqbRm7784"),sQuery(id+"F0.wireOp",EDGE,"A3QQ103k-oBam-uK2f-Ywbn-FOsahd6y3kCF"),sQuery(id+"F0.wireOp",EDGE,"E22"),sQuery(id+"F0.wireOp",EDGE,"O4fUSGsA-sgfy-2hAb-lYRv-adjy5g4jnHMn"),sQuery(id+"F0.wireOp",EDGE,"he4H8z8F-eg87-8e6K-5810-5zuvFcfIEFNb")])],"isStart":false})]});}
            var Q28;
            Q28=makeQuery(id+"F1.opExtrude","CAP_EDGE",EDGE,{"disambiguationData":[OSD([sQuery(id+"F0.wireOp",EDGE,"E3.5")])],"isStart":false});
            var Q29;
            {var subQ0=sQuery(id+"F0.wireOp",EDGE,"E3.1");var subQ1=sQuery(id+"F0.wireOp",EDGE,"E3.0");Q29=makeQuery(id+"F11.opFillet","BLEND_EDGE",EDGE,{"blendedFrom":[makeQuery(id+"F1.opExtrude","SWEPT_EDGE",EDGE,{"disambiguationData":[OSD([subQ1,subQ0])]}),makeQuery(id+"F1.opExtrude","CAP_FACE",FACE,{"disambiguationData":[OSD([sQuery(id+"F0.wireOp",EDGE,"E0.0"),sQuery(id+"F0.wireOp",EDGE,"E0.2"),sQuery(id+"F0.wireOp",EDGE,"E0.4"),sQuery(id+"F0.wireOp",EDGE,"E1.0"),sQuery(id+"F0.wireOp",EDGE,"E1.2"),sQuery(id+"F0.wireOp",EDGE,"E1.3"),sQuery(id+"F0.wireOp",EDGE,"E1.4"),sQuery(id+"F0.wireOp",EDGE,"E1.5"),sQuery(id+"F0.wireOp",EDGE,"E2.0"),sQuery(id+"F0.wireOp",EDGE,"E2.1"),sQuery(id+"F0.wireOp",EDGE,"E2.2"),sQuery(id+"F0.wireOp",EDGE,"E2.3"),sQuery(id+"F0.wireOp",EDGE,"E2.4"),subQ1,subQ0,sQuery(id+"F0.wireOp",EDGE,"E3.2"),sQuery(id+"F0.wireOp",EDGE,"E3.4"),sQuery(id+"F0.wireOp",EDGE,"E3.5"),sQuery(id+"F0.wireOp",EDGE,"E11"),sQuery(id+"F0.wireOp",EDGE,"E12"),sQuery(id+"F0.wireOp",EDGE,"E13"),sQuery(id+"F0.wireOp",EDGE,"E14"),sQuery(id+"F0.wireOp",EDGE,"E15"),sQuery(id+"F0.wireOp",EDGE,"E16"),sQuery(id+"F0.wireOp",EDGE,"E17"),sQuery(id+"F0.wireOp",EDGE,"fGXXUOoa-G3to-nFfg-Xp41-Spi5BgRDYh0n"),sQuery(id+"F0.wireOp",EDGE,"maiLpuxs-2Sfq-8eKx-MEtN-jPa1VSy1aRe3"),sQuery(id+"F0.wireOp",EDGE,"E19"),sQuery(id+"F0.wireOp",EDGE,"TkPDQIJV-pblC-kMUo-zlvk-0mYhqbRm7784"),sQuery(id+"F0.wireOp",EDGE,"A3QQ103k-oBam-uK2f-Ywbn-FOsahd6y3kCF"),sQuery(id+"F0.wireOp",EDGE,"E22"),sQuery(id+"F0.wireOp",EDGE,"O4fUSGsA-sgfy-2hAb-lYRv-adjy5g4jnHMn"),sQuery(id+"F0.wireOp",EDGE,"he4H8z8F-eg87-8e6K-5810-5zuvFcfIEFNb")])],"isStart":false})],"blendedInto":[makeQuery(id+"F1.opExtrude","CAP_FACE",FACE,{"disambiguationData":[OSD([sQuery(id+"F0.wireOp",EDGE,"E0.0"),sQuery(id+"F0.wireOp",EDGE,"E0.2"),sQuery(id+"F0.wireOp",EDGE,"E0.4"),sQuery(id+"F0.wireOp",EDGE,"E1.0"),sQuery(id+"F0.wireOp",EDGE,"E1.2"),sQuery(id+"F0.wireOp",EDGE,"E1.3"),sQuery(id+"F0.wireOp",EDGE,"E1.4"),sQuery(id+"F0.wireOp",EDGE,"E1.5"),sQuery(id+"F0.wireOp",EDGE,"E2.0"),sQuery(id+"F0.wireOp",EDGE,"E2.1"),sQuery(id+"F0.wireOp",EDGE,"E2.2"),sQuery(id+"F0.wireOp",EDGE,"E2.3"),sQuery(id+"F0.wireOp",EDGE,"E2.4"),subQ1,subQ0,sQuery(id+"F0.wireOp",EDGE,"E3.2"),sQuery(id+"F0.wireOp",EDGE,"E3.4"),sQuery(id+"F0.wireOp",EDGE,"E3.5"),sQuery(id+"F0.wireOp",EDGE,"E11"),sQuery(id+"F0.wireOp",EDGE,"E12"),sQuery(id+"F0.wireOp",EDGE,"E13"),sQuery(id+"F0.wireOp",EDGE,"E14"),sQuery(id+"F0.wireOp",EDGE,"E15"),sQuery(id+"F0.wireOp",EDGE,"E16"),sQuery(id+"F0.wireOp",EDGE,"E17"),sQuery(id+"F0.wireOp",EDGE,"fGXXUOoa-G3to-nFfg-Xp41-Spi5BgRDYh0n"),sQuery(id+"F0.wireOp",EDGE,"maiLpuxs-2Sfq-8eKx-MEtN-jPa1VSy1aRe3"),sQuery(id+"F0.wireOp",EDGE,"E19"),sQuery(id+"F0.wireOp",EDGE,"TkPDQIJV-pblC-kMUo-zlvk-0mYhqbRm7784"),sQuery(id+"F0.wireOp",EDGE,"A3QQ103k-oBam-uK2f-Ywbn-FOsahd6y3kCF"),sQuery(id+"F0.wireOp",EDGE,"E22"),sQuery(id+"F0.wireOp",EDGE,"O4fUSGsA-sgfy-2hAb-lYRv-adjy5g4jnHMn"),sQuery(id+"F0.wireOp",EDGE,"he4H8z8F-eg87-8e6K-5810-5zuvFcfIEFNb")])],"isStart":false})]});}
            var Q30;
            Q30=makeQuery(id+"F1.opExtrude","CAP_EDGE",EDGE,{"disambiguationData":[OSD([sQuery(id+"F0.wireOp",EDGE,"E3.0")])],"isStart":false});
            var Q31;
            Q31=makeQuery(id+"F1.opExtrude","CAP_EDGE",EDGE,{"disambiguationData":[OSD([sQuery(id+"F0.wireOp",EDGE,"E3.1")])],"isStart":false});
            var Q32;
            {var subQ0=sQuery(id+"F0.wireOp",EDGE,"E3.2");var subQ1=sQuery(id+"F0.wireOp",EDGE,"E3.1");Q32=makeQuery(id+"F11.opFillet","BLEND_EDGE",EDGE,{"blendedFrom":[makeQuery(id+"F1.opExtrude","SWEPT_EDGE",EDGE,{"disambiguationData":[OSD([subQ1,subQ0])]}),makeQuery(id+"F1.opExtrude","CAP_FACE",FACE,{"disambiguationData":[OSD([sQuery(id+"F0.wireOp",EDGE,"E0.0"),sQuery(id+"F0.wireOp",EDGE,"E0.2"),sQuery(id+"F0.wireOp",EDGE,"E0.4"),sQuery(id+"F0.wireOp",EDGE,"E1.0"),sQuery(id+"F0.wireOp",EDGE,"E1.2"),sQuery(id+"F0.wireOp",EDGE,"E1.3"),sQuery(id+"F0.wireOp",EDGE,"E1.4"),sQuery(id+"F0.wireOp",EDGE,"E1.5"),sQuery(id+"F0.wireOp",EDGE,"E2.0"),sQuery(id+"F0.wireOp",EDGE,"E2.1"),sQuery(id+"F0.wireOp",EDGE,"E2.2"),sQuery(id+"F0.wireOp",EDGE,"E2.3"),sQuery(id+"F0.wireOp",EDGE,"E2.4"),sQuery(id+"F0.wireOp",EDGE,"E3.0"),subQ1,subQ0,sQuery(id+"F0.wireOp",EDGE,"E3.4"),sQuery(id+"F0.wireOp",EDGE,"E3.5"),sQuery(id+"F0.wireOp",EDGE,"E11"),sQuery(id+"F0.wireOp",EDGE,"E12"),sQuery(id+"F0.wireOp",EDGE,"E13"),sQuery(id+"F0.wireOp",EDGE,"E14"),sQuery(id+"F0.wireOp",EDGE,"E15"),sQuery(id+"F0.wireOp",EDGE,"E16"),sQuery(id+"F0.wireOp",EDGE,"E17"),sQuery(id+"F0.wireOp",EDGE,"fGXXUOoa-G3to-nFfg-Xp41-Spi5BgRDYh0n"),sQuery(id+"F0.wireOp",EDGE,"maiLpuxs-2Sfq-8eKx-MEtN-jPa1VSy1aRe3"),sQuery(id+"F0.wireOp",EDGE,"E19"),sQuery(id+"F0.wireOp",EDGE,"TkPDQIJV-pblC-kMUo-zlvk-0mYhqbRm7784"),sQuery(id+"F0.wireOp",EDGE,"A3QQ103k-oBam-uK2f-Ywbn-FOsahd6y3kCF"),sQuery(id+"F0.wireOp",EDGE,"E22"),sQuery(id+"F0.wireOp",EDGE,"O4fUSGsA-sgfy-2hAb-lYRv-adjy5g4jnHMn"),sQuery(id+"F0.wireOp",EDGE,"he4H8z8F-eg87-8e6K-5810-5zuvFcfIEFNb")])],"isStart":false})],"blendedInto":[makeQuery(id+"F1.opExtrude","CAP_FACE",FACE,{"disambiguationData":[OSD([sQuery(id+"F0.wireOp",EDGE,"E0.0"),sQuery(id+"F0.wireOp",EDGE,"E0.2"),sQuery(id+"F0.wireOp",EDGE,"E0.4"),sQuery(id+"F0.wireOp",EDGE,"E1.0"),sQuery(id+"F0.wireOp",EDGE,"E1.2"),sQuery(id+"F0.wireOp",EDGE,"E1.3"),sQuery(id+"F0.wireOp",EDGE,"E1.4"),sQuery(id+"F0.wireOp",EDGE,"E1.5"),sQuery(id+"F0.wireOp",EDGE,"E2.0"),sQuery(id+"F0.wireOp",EDGE,"E2.1"),sQuery(id+"F0.wireOp",EDGE,"E2.2"),sQuery(id+"F0.wireOp",EDGE,"E2.3"),sQuery(id+"F0.wireOp",EDGE,"E2.4"),sQuery(id+"F0.wireOp",EDGE,"E3.0"),subQ1,subQ0,sQuery(id+"F0.wireOp",EDGE,"E3.4"),sQuery(id+"F0.wireOp",EDGE,"E3.5"),sQuery(id+"F0.wireOp",EDGE,"E11"),sQuery(id+"F0.wireOp",EDGE,"E12"),sQuery(id+"F0.wireOp",EDGE,"E13"),sQuery(id+"F0.wireOp",EDGE,"E14"),sQuery(id+"F0.wireOp",EDGE,"E15"),sQuery(id+"F0.wireOp",EDGE,"E16"),sQuery(id+"F0.wireOp",EDGE,"E17"),sQuery(id+"F0.wireOp",EDGE,"fGXXUOoa-G3to-nFfg-Xp41-Spi5BgRDYh0n"),sQuery(id+"F0.wireOp",EDGE,"maiLpuxs-2Sfq-8eKx-MEtN-jPa1VSy1aRe3"),sQuery(id+"F0.wireOp",EDGE,"E19"),sQuery(id+"F0.wireOp",EDGE,"TkPDQIJV-pblC-kMUo-zlvk-0mYhqbRm7784"),sQuery(id+"F0.wireOp",EDGE,"A3QQ103k-oBam-uK2f-Ywbn-FOsahd6y3kCF"),sQuery(id+"F0.wireOp",EDGE,"E22"),sQuery(id+"F0.wireOp",EDGE,"O4fUSGsA-sgfy-2hAb-lYRv-adjy5g4jnHMn"),sQuery(id+"F0.wireOp",EDGE,"he4H8z8F-eg87-8e6K-5810-5zuvFcfIEFNb")])],"isStart":false})]});}
            var Q33;
            {var subQ0=sQuery(id+"F0.wireOp",EDGE,"E2.0");var subQ1=sQuery(id+"F0.wireOp",EDGE,"E0.2");Q33=makeQuery(id+"F11.opFillet","BLEND_EDGE",EDGE,{"blendedFrom":[makeQuery(id+"F1.opExtrude","SWEPT_EDGE",EDGE,{"disambiguationData":[OSD([subQ1,subQ0,sQuery(id+"F0.wireOp",EDGE,"E2.5"),sQuery(id+"F0.wireOp",EDGE,"E20")])]}),makeQuery(id+"F1.opExtrude","CAP_FACE",FACE,{"disambiguationData":[OSD([sQuery(id+"F0.wireOp",EDGE,"E0.0"),subQ1,sQuery(id+"F0.wireOp",EDGE,"E0.4"),sQuery(id+"F0.wireOp",EDGE,"E1.0"),sQuery(id+"F0.wireOp",EDGE,"E1.2"),sQuery(id+"F0.wireOp",EDGE,"E1.3"),sQuery(id+"F0.wireOp",EDGE,"E1.4"),sQuery(id+"F0.wireOp",EDGE,"E1.5"),subQ0,sQuery(id+"F0.wireOp",EDGE,"E2.1"),sQuery(id+"F0.wireOp",EDGE,"E2.2"),sQuery(id+"F0.wireOp",EDGE,"E2.3"),sQuery(id+"F0.wireOp",EDGE,"E2.4"),sQuery(id+"F0.wireOp",EDGE,"E3.0"),sQuery(id+"F0.wireOp",EDGE,"E3.1"),sQuery(id+"F0.wireOp",EDGE,"E3.2"),sQuery(id+"F0.wireOp",EDGE,"E3.4"),sQuery(id+"F0.wireOp",EDGE,"E3.5"),sQuery(id+"F0.wireOp",EDGE,"E11"),sQuery(id+"F0.wireOp",EDGE,"E12"),sQuery(id+"F0.wireOp",EDGE,"E13"),sQuery(id+"F0.wireOp",EDGE,"E14"),sQuery(id+"F0.wireOp",EDGE,"E15"),sQuery(id+"F0.wireOp",EDGE,"E16"),sQuery(id+"F0.wireOp",EDGE,"E17"),sQuery(id+"F0.wireOp",EDGE,"fGXXUOoa-G3to-nFfg-Xp41-Spi5BgRDYh0n"),sQuery(id+"F0.wireOp",EDGE,"maiLpuxs-2Sfq-8eKx-MEtN-jPa1VSy1aRe3"),sQuery(id+"F0.wireOp",EDGE,"E19"),sQuery(id+"F0.wireOp",EDGE,"TkPDQIJV-pblC-kMUo-zlvk-0mYhqbRm7784"),sQuery(id+"F0.wireOp",EDGE,"A3QQ103k-oBam-uK2f-Ywbn-FOsahd6y3kCF"),sQuery(id+"F0.wireOp",EDGE,"E22"),sQuery(id+"F0.wireOp",EDGE,"O4fUSGsA-sgfy-2hAb-lYRv-adjy5g4jnHMn"),sQuery(id+"F0.wireOp",EDGE,"he4H8z8F-eg87-8e6K-5810-5zuvFcfIEFNb")])],"isStart":false})],"blendedInto":[makeQuery(id+"F1.opExtrude","CAP_FACE",FACE,{"disambiguationData":[OSD([sQuery(id+"F0.wireOp",EDGE,"E0.0"),subQ1,sQuery(id+"F0.wireOp",EDGE,"E0.4"),sQuery(id+"F0.wireOp",EDGE,"E1.0"),sQuery(id+"F0.wireOp",EDGE,"E1.2"),sQuery(id+"F0.wireOp",EDGE,"E1.3"),sQuery(id+"F0.wireOp",EDGE,"E1.4"),sQuery(id+"F0.wireOp",EDGE,"E1.5"),subQ0,sQuery(id+"F0.wireOp",EDGE,"E2.1"),sQuery(id+"F0.wireOp",EDGE,"E2.2"),sQuery(id+"F0.wireOp",EDGE,"E2.3"),sQuery(id+"F0.wireOp",EDGE,"E2.4"),sQuery(id+"F0.wireOp",EDGE,"E3.0"),sQuery(id+"F0.wireOp",EDGE,"E3.1"),sQuery(id+"F0.wireOp",EDGE,"E3.2"),sQuery(id+"F0.wireOp",EDGE,"E3.4"),sQuery(id+"F0.wireOp",EDGE,"E3.5"),sQuery(id+"F0.wireOp",EDGE,"E11"),sQuery(id+"F0.wireOp",EDGE,"E12"),sQuery(id+"F0.wireOp",EDGE,"E13"),sQuery(id+"F0.wireOp",EDGE,"E14"),sQuery(id+"F0.wireOp",EDGE,"E15"),sQuery(id+"F0.wireOp",EDGE,"E16"),sQuery(id+"F0.wireOp",EDGE,"E17"),sQuery(id+"F0.wireOp",EDGE,"fGXXUOoa-G3to-nFfg-Xp41-Spi5BgRDYh0n"),sQuery(id+"F0.wireOp",EDGE,"maiLpuxs-2Sfq-8eKx-MEtN-jPa1VSy1aRe3"),sQuery(id+"F0.wireOp",EDGE,"E19"),sQuery(id+"F0.wireOp",EDGE,"TkPDQIJV-pblC-kMUo-zlvk-0mYhqbRm7784"),sQuery(id+"F0.wireOp",EDGE,"A3QQ103k-oBam-uK2f-Ywbn-FOsahd6y3kCF"),sQuery(id+"F0.wireOp",EDGE,"E22"),sQuery(id+"F0.wireOp",EDGE,"O4fUSGsA-sgfy-2hAb-lYRv-adjy5g4jnHMn"),sQuery(id+"F0.wireOp",EDGE,"he4H8z8F-eg87-8e6K-5810-5zuvFcfIEFNb")])],"isStart":false})]});}
            var Q34;
            Q34=makeQuery(id+"F1.opExtrude","CAP_EDGE",EDGE,{"disambiguationData":[OSD([sQuery(id+"F0.wireOp",EDGE,"E0.2")])],"isStart":false});
            var Q35;
            {var subQ0=sQuery(id+"F0.wireOp",EDGE,"E3.2");var subQ1=sQuery(id+"F0.wireOp",EDGE,"E0.2");Q35=makeQuery(id+"F11.opFillet","BLEND_EDGE",EDGE,{"blendedFrom":[makeQuery(id+"F1.opExtrude","SWEPT_EDGE",EDGE,{"disambiguationData":[OSD([sQuery(id+"F0.wireOp",EDGE,"E0.1"),subQ1,subQ0,sQuery(id+"F0.wireOp",EDGE,"E3.3")])]}),makeQuery(id+"F1.opExtrude","CAP_FACE",FACE,{"disambiguationData":[OSD([sQuery(id+"F0.wireOp",EDGE,"E0.0"),subQ1,sQuery(id+"F0.wireOp",EDGE,"E0.4"),sQuery(id+"F0.wireOp",EDGE,"E1.0"),sQuery(id+"F0.wireOp",EDGE,"E1.2"),sQuery(id+"F0.wireOp",EDGE,"E1.3"),sQuery(id+"F0.wireOp",EDGE,"E1.4"),sQuery(id+"F0.wireOp",EDGE,"E1.5"),sQuery(id+"F0.wireOp",EDGE,"E2.0"),sQuery(id+"F0.wireOp",EDGE,"E2.1"),sQuery(id+"F0.wireOp",EDGE,"E2.2"),sQuery(id+"F0.wireOp",EDGE,"E2.3"),sQuery(id+"F0.wireOp",EDGE,"E2.4"),sQuery(id+"F0.wireOp",EDGE,"E3.0"),sQuery(id+"F0.wireOp",EDGE,"E3.1"),subQ0,sQuery(id+"F0.wireOp",EDGE,"E3.4"),sQuery(id+"F0.wireOp",EDGE,"E3.5"),sQuery(id+"F0.wireOp",EDGE,"E11"),sQuery(id+"F0.wireOp",EDGE,"E12"),sQuery(id+"F0.wireOp",EDGE,"E13"),sQuery(id+"F0.wireOp",EDGE,"E14"),sQuery(id+"F0.wireOp",EDGE,"E15"),sQuery(id+"F0.wireOp",EDGE,"E16"),sQuery(id+"F0.wireOp",EDGE,"E17"),sQuery(id+"F0.wireOp",EDGE,"fGXXUOoa-G3to-nFfg-Xp41-Spi5BgRDYh0n"),sQuery(id+"F0.wireOp",EDGE,"maiLpuxs-2Sfq-8eKx-MEtN-jPa1VSy1aRe3"),sQuery(id+"F0.wireOp",EDGE,"E19"),sQuery(id+"F0.wireOp",EDGE,"TkPDQIJV-pblC-kMUo-zlvk-0mYhqbRm7784"),sQuery(id+"F0.wireOp",EDGE,"A3QQ103k-oBam-uK2f-Ywbn-FOsahd6y3kCF"),sQuery(id+"F0.wireOp",EDGE,"E22"),sQuery(id+"F0.wireOp",EDGE,"O4fUSGsA-sgfy-2hAb-lYRv-adjy5g4jnHMn"),sQuery(id+"F0.wireOp",EDGE,"he4H8z8F-eg87-8e6K-5810-5zuvFcfIEFNb")])],"isStart":false})],"blendedInto":[makeQuery(id+"F1.opExtrude","CAP_FACE",FACE,{"disambiguationData":[OSD([sQuery(id+"F0.wireOp",EDGE,"E0.0"),subQ1,sQuery(id+"F0.wireOp",EDGE,"E0.4"),sQuery(id+"F0.wireOp",EDGE,"E1.0"),sQuery(id+"F0.wireOp",EDGE,"E1.2"),sQuery(id+"F0.wireOp",EDGE,"E1.3"),sQuery(id+"F0.wireOp",EDGE,"E1.4"),sQuery(id+"F0.wireOp",EDGE,"E1.5"),sQuery(id+"F0.wireOp",EDGE,"E2.0"),sQuery(id+"F0.wireOp",EDGE,"E2.1"),sQuery(id+"F0.wireOp",EDGE,"E2.2"),sQuery(id+"F0.wireOp",EDGE,"E2.3"),sQuery(id+"F0.wireOp",EDGE,"E2.4"),sQuery(id+"F0.wireOp",EDGE,"E3.0"),sQuery(id+"F0.wireOp",EDGE,"E3.1"),subQ0,sQuery(id+"F0.wireOp",EDGE,"E3.4"),sQuery(id+"F0.wireOp",EDGE,"E3.5"),sQuery(id+"F0.wireOp",EDGE,"E11"),sQuery(id+"F0.wireOp",EDGE,"E12"),sQuery(id+"F0.wireOp",EDGE,"E13"),sQuery(id+"F0.wireOp",EDGE,"E14"),sQuery(id+"F0.wireOp",EDGE,"E15"),sQuery(id+"F0.wireOp",EDGE,"E16"),sQuery(id+"F0.wireOp",EDGE,"E17"),sQuery(id+"F0.wireOp",EDGE,"fGXXUOoa-G3to-nFfg-Xp41-Spi5BgRDYh0n"),sQuery(id+"F0.wireOp",EDGE,"maiLpuxs-2Sfq-8eKx-MEtN-jPa1VSy1aRe3"),sQuery(id+"F0.wireOp",EDGE,"E19"),sQuery(id+"F0.wireOp",EDGE,"TkPDQIJV-pblC-kMUo-zlvk-0mYhqbRm7784"),sQuery(id+"F0.wireOp",EDGE,"A3QQ103k-oBam-uK2f-Ywbn-FOsahd6y3kCF"),sQuery(id+"F0.wireOp",EDGE,"E22"),sQuery(id+"F0.wireOp",EDGE,"O4fUSGsA-sgfy-2hAb-lYRv-adjy5g4jnHMn"),sQuery(id+"F0.wireOp",EDGE,"he4H8z8F-eg87-8e6K-5810-5zuvFcfIEFNb")])],"isStart":false})]});}
            var Q36;
            Q36=makeQuery(id+"F1.opExtrude","CAP_EDGE",EDGE,{"disambiguationData":[OSD([sQuery(id+"F0.wireOp",EDGE,"E3.2")])],"isStart":false});
            var Q37;
            Q37=makeQuery(id+"F1.opExtrude","CAP_EDGE",EDGE,{"disambiguationData":[OSD([sQuery(id+"F0.wireOp",EDGE,"E12")])],"isStart":false});
            var Q38;
            Q38=makeQuery(id+"F1.opExtrude","CAP_EDGE",EDGE,{"disambiguationData":[OSD([sQuery(id+"F0.wireOp",EDGE,"E2.0")])],"isStart":false});
            var Q39;
            Q39=makeQuery(id+"F1.opExtrude","CAP_EDGE",EDGE,{"disambiguationData":[OSD([sQuery(id+"F0.wireOp",EDGE,"E11")])],"isStart":false});
            var Q40;
            Q40=makeQuery(id+"F1.opExtrude","CAP_EDGE",EDGE,{"disambiguationData":[OSD([sQuery(id+"F0.wireOp",EDGE,"E2.1")])],"isStart":false});
            var Q41;
            {var subQ0=sQuery(id+"F0.wireOp",EDGE,"E12");var subQ1=sQuery(id+"F0.wireOp",EDGE,"E11");Q41=makeQuery(id+"F12.opFillet","BLEND_EDGE",EDGE,{"blendedFrom":[makeQuery(id+"F1.opExtrude","SWEPT_EDGE",EDGE,{"disambiguationData":[OSD([sQuery(id+"F0.wireOp",EDGE,"E8"),subQ1,subQ0])]}),makeQuery(id+"F1.opExtrude","CAP_FACE",FACE,{"disambiguationData":[OSD([sQuery(id+"F0.wireOp",EDGE,"E0.0"),sQuery(id+"F0.wireOp",EDGE,"E0.2"),sQuery(id+"F0.wireOp",EDGE,"E0.4"),sQuery(id+"F0.wireOp",EDGE,"E1.0"),sQuery(id+"F0.wireOp",EDGE,"E1.2"),sQuery(id+"F0.wireOp",EDGE,"E1.3"),sQuery(id+"F0.wireOp",EDGE,"E1.4"),sQuery(id+"F0.wireOp",EDGE,"E1.5"),sQuery(id+"F0.wireOp",EDGE,"E2.0"),sQuery(id+"F0.wireOp",EDGE,"E2.1"),sQuery(id+"F0.wireOp",EDGE,"E2.2"),sQuery(id+"F0.wireOp",EDGE,"E2.3"),sQuery(id+"F0.wireOp",EDGE,"E2.4"),sQuery(id+"F0.wireOp",EDGE,"E3.0"),sQuery(id+"F0.wireOp",EDGE,"E3.1"),sQuery(id+"F0.wireOp",EDGE,"E3.2"),sQuery(id+"F0.wireOp",EDGE,"E3.4"),sQuery(id+"F0.wireOp",EDGE,"E3.5"),subQ1,subQ0,sQuery(id+"F0.wireOp",EDGE,"E13"),sQuery(id+"F0.wireOp",EDGE,"E14"),sQuery(id+"F0.wireOp",EDGE,"E15"),sQuery(id+"F0.wireOp",EDGE,"E16"),sQuery(id+"F0.wireOp",EDGE,"E17"),sQuery(id+"F0.wireOp",EDGE,"fGXXUOoa-G3to-nFfg-Xp41-Spi5BgRDYh0n"),sQuery(id+"F0.wireOp",EDGE,"maiLpuxs-2Sfq-8eKx-MEtN-jPa1VSy1aRe3"),sQuery(id+"F0.wireOp",EDGE,"E19"),sQuery(id+"F0.wireOp",EDGE,"TkPDQIJV-pblC-kMUo-zlvk-0mYhqbRm7784"),sQuery(id+"F0.wireOp",EDGE,"A3QQ103k-oBam-uK2f-Ywbn-FOsahd6y3kCF"),sQuery(id+"F0.wireOp",EDGE,"E22"),sQuery(id+"F0.wireOp",EDGE,"O4fUSGsA-sgfy-2hAb-lYRv-adjy5g4jnHMn"),sQuery(id+"F0.wireOp",EDGE,"he4H8z8F-eg87-8e6K-5810-5zuvFcfIEFNb")])],"isStart":false})],"blendedInto":[makeQuery(id+"F1.opExtrude","CAP_FACE",FACE,{"disambiguationData":[OSD([sQuery(id+"F0.wireOp",EDGE,"E0.0"),sQuery(id+"F0.wireOp",EDGE,"E0.2"),sQuery(id+"F0.wireOp",EDGE,"E0.4"),sQuery(id+"F0.wireOp",EDGE,"E1.0"),sQuery(id+"F0.wireOp",EDGE,"E1.2"),sQuery(id+"F0.wireOp",EDGE,"E1.3"),sQuery(id+"F0.wireOp",EDGE,"E1.4"),sQuery(id+"F0.wireOp",EDGE,"E1.5"),sQuery(id+"F0.wireOp",EDGE,"E2.0"),sQuery(id+"F0.wireOp",EDGE,"E2.1"),sQuery(id+"F0.wireOp",EDGE,"E2.2"),sQuery(id+"F0.wireOp",EDGE,"E2.3"),sQuery(id+"F0.wireOp",EDGE,"E2.4"),sQuery(id+"F0.wireOp",EDGE,"E3.0"),sQuery(id+"F0.wireOp",EDGE,"E3.1"),sQuery(id+"F0.wireOp",EDGE,"E3.2"),sQuery(id+"F0.wireOp",EDGE,"E3.4"),sQuery(id+"F0.wireOp",EDGE,"E3.5"),subQ1,subQ0,sQuery(id+"F0.wireOp",EDGE,"E13"),sQuery(id+"F0.wireOp",EDGE,"E14"),sQuery(id+"F0.wireOp",EDGE,"E15"),sQuery(id+"F0.wireOp",EDGE,"E16"),sQuery(id+"F0.wireOp",EDGE,"E17"),sQuery(id+"F0.wireOp",EDGE,"fGXXUOoa-G3to-nFfg-Xp41-Spi5BgRDYh0n"),sQuery(id+"F0.wireOp",EDGE,"maiLpuxs-2Sfq-8eKx-MEtN-jPa1VSy1aRe3"),sQuery(id+"F0.wireOp",EDGE,"E19"),sQuery(id+"F0.wireOp",EDGE,"TkPDQIJV-pblC-kMUo-zlvk-0mYhqbRm7784"),sQuery(id+"F0.wireOp",EDGE,"A3QQ103k-oBam-uK2f-Ywbn-FOsahd6y3kCF"),sQuery(id+"F0.wireOp",EDGE,"E22"),sQuery(id+"F0.wireOp",EDGE,"O4fUSGsA-sgfy-2hAb-lYRv-adjy5g4jnHMn"),sQuery(id+"F0.wireOp",EDGE,"he4H8z8F-eg87-8e6K-5810-5zuvFcfIEFNb")])],"isStart":false})]});}
            var Q42;
            {var subQ0=sQuery(id+"F0.wireOp",EDGE,"E1.4");var subQ1=sQuery(id+"F0.wireOp",EDGE,"E1.3");Q42=makeQuery(id+"F11.opFillet","BLEND_EDGE",EDGE,{"blendedFrom":[makeQuery(id+"F1.opExtrude","SWEPT_EDGE",EDGE,{"disambiguationData":[OSD([subQ1,subQ0])]}),makeQuery(id+"F1.opExtrude","CAP_FACE",FACE,{"disambiguationData":[OSD([sQuery(id+"F0.wireOp",EDGE,"E0.0"),sQuery(id+"F0.wireOp",EDGE,"E0.2"),sQuery(id+"F0.wireOp",EDGE,"E0.4"),sQuery(id+"F0.wireOp",EDGE,"E1.0"),sQuery(id+"F0.wireOp",EDGE,"E1.2"),subQ1,subQ0,sQuery(id+"F0.wireOp",EDGE,"E1.5"),sQuery(id+"F0.wireOp",EDGE,"E2.0"),sQuery(id+"F0.wireOp",EDGE,"E2.1"),sQuery(id+"F0.wireOp",EDGE,"E2.2"),sQuery(id+"F0.wireOp",EDGE,"E2.3"),sQuery(id+"F0.wireOp",EDGE,"E2.4"),sQuery(id+"F0.wireOp",EDGE,"E3.0"),sQuery(id+"F0.wireOp",EDGE,"E3.1"),sQuery(id+"F0.wireOp",EDGE,"E3.2"),sQuery(id+"F0.wireOp",EDGE,"E3.4"),sQuery(id+"F0.wireOp",EDGE,"E3.5"),sQuery(id+"F0.wireOp",EDGE,"E11"),sQuery(id+"F0.wireOp",EDGE,"E12"),sQuery(id+"F0.wireOp",EDGE,"E13"),sQuery(id+"F0.wireOp",EDGE,"E14"),sQuery(id+"F0.wireOp",EDGE,"E15"),sQuery(id+"F0.wireOp",EDGE,"E16"),sQuery(id+"F0.wireOp",EDGE,"E17"),sQuery(id+"F0.wireOp",EDGE,"fGXXUOoa-G3to-nFfg-Xp41-Spi5BgRDYh0n"),sQuery(id+"F0.wireOp",EDGE,"maiLpuxs-2Sfq-8eKx-MEtN-jPa1VSy1aRe3"),sQuery(id+"F0.wireOp",EDGE,"E19"),sQuery(id+"F0.wireOp",EDGE,"TkPDQIJV-pblC-kMUo-zlvk-0mYhqbRm7784"),sQuery(id+"F0.wireOp",EDGE,"A3QQ103k-oBam-uK2f-Ywbn-FOsahd6y3kCF"),sQuery(id+"F0.wireOp",EDGE,"E22"),sQuery(id+"F0.wireOp",EDGE,"O4fUSGsA-sgfy-2hAb-lYRv-adjy5g4jnHMn"),sQuery(id+"F0.wireOp",EDGE,"he4H8z8F-eg87-8e6K-5810-5zuvFcfIEFNb")])],"isStart":true})],"blendedInto":[makeQuery(id+"F1.opExtrude","CAP_FACE",FACE,{"disambiguationData":[OSD([sQuery(id+"F0.wireOp",EDGE,"E0.0"),sQuery(id+"F0.wireOp",EDGE,"E0.2"),sQuery(id+"F0.wireOp",EDGE,"E0.4"),sQuery(id+"F0.wireOp",EDGE,"E1.0"),sQuery(id+"F0.wireOp",EDGE,"E1.2"),subQ1,subQ0,sQuery(id+"F0.wireOp",EDGE,"E1.5"),sQuery(id+"F0.wireOp",EDGE,"E2.0"),sQuery(id+"F0.wireOp",EDGE,"E2.1"),sQuery(id+"F0.wireOp",EDGE,"E2.2"),sQuery(id+"F0.wireOp",EDGE,"E2.3"),sQuery(id+"F0.wireOp",EDGE,"E2.4"),sQuery(id+"F0.wireOp",EDGE,"E3.0"),sQuery(id+"F0.wireOp",EDGE,"E3.1"),sQuery(id+"F0.wireOp",EDGE,"E3.2"),sQuery(id+"F0.wireOp",EDGE,"E3.4"),sQuery(id+"F0.wireOp",EDGE,"E3.5"),sQuery(id+"F0.wireOp",EDGE,"E11"),sQuery(id+"F0.wireOp",EDGE,"E12"),sQuery(id+"F0.wireOp",EDGE,"E13"),sQuery(id+"F0.wireOp",EDGE,"E14"),sQuery(id+"F0.wireOp",EDGE,"E15"),sQuery(id+"F0.wireOp",EDGE,"E16"),sQuery(id+"F0.wireOp",EDGE,"E17"),sQuery(id+"F0.wireOp",EDGE,"fGXXUOoa-G3to-nFfg-Xp41-Spi5BgRDYh0n"),sQuery(id+"F0.wireOp",EDGE,"maiLpuxs-2Sfq-8eKx-MEtN-jPa1VSy1aRe3"),sQuery(id+"F0.wireOp",EDGE,"E19"),sQuery(id+"F0.wireOp",EDGE,"TkPDQIJV-pblC-kMUo-zlvk-0mYhqbRm7784"),sQuery(id+"F0.wireOp",EDGE,"A3QQ103k-oBam-uK2f-Ywbn-FOsahd6y3kCF"),sQuery(id+"F0.wireOp",EDGE,"E22"),sQuery(id+"F0.wireOp",EDGE,"O4fUSGsA-sgfy-2hAb-lYRv-adjy5g4jnHMn"),sQuery(id+"F0.wireOp",EDGE,"he4H8z8F-eg87-8e6K-5810-5zuvFcfIEFNb")])],"isStart":true})]});}
            var Q43;
            Q43=makeQuery(id+"F1.opExtrude","CAP_EDGE",EDGE,{"disambiguationData":[OSD([sQuery(id+"F0.wireOp",EDGE,"E1.3")])],"isStart":true});
            var Q44;
            Q44=makeQuery(id+"F1.opExtrude","CAP_EDGE",EDGE,{"disambiguationData":[OSD([sQuery(id+"F0.wireOp",EDGE,"E16")])],"isStart":true});
            var Q45;
            {var subQ0=sQuery(id+"F0.wireOp",EDGE,"E16");var subQ1=sQuery(id+"F0.wireOp",EDGE,"E15");Q45=makeQuery(id+"F12.opFillet","BLEND_EDGE",EDGE,{"blendedFrom":[makeQuery(id+"F1.opExtrude","SWEPT_EDGE",EDGE,{"disambiguationData":[OSD([sQuery(id+"F0.wireOp",EDGE,"E9"),subQ1,subQ0])]}),makeQuery(id+"F1.opExtrude","CAP_FACE",FACE,{"disambiguationData":[OSD([sQuery(id+"F0.wireOp",EDGE,"E0.0"),sQuery(id+"F0.wireOp",EDGE,"E0.2"),sQuery(id+"F0.wireOp",EDGE,"E0.4"),sQuery(id+"F0.wireOp",EDGE,"E1.0"),sQuery(id+"F0.wireOp",EDGE,"E1.2"),sQuery(id+"F0.wireOp",EDGE,"E1.3"),sQuery(id+"F0.wireOp",EDGE,"E1.4"),sQuery(id+"F0.wireOp",EDGE,"E1.5"),sQuery(id+"F0.wireOp",EDGE,"E2.0"),sQuery(id+"F0.wireOp",EDGE,"E2.1"),sQuery(id+"F0.wireOp",EDGE,"E2.2"),sQuery(id+"F0.wireOp",EDGE,"E2.3"),sQuery(id+"F0.wireOp",EDGE,"E2.4"),sQuery(id+"F0.wireOp",EDGE,"E3.0"),sQuery(id+"F0.wireOp",EDGE,"E3.1"),sQuery(id+"F0.wireOp",EDGE,"E3.2"),sQuery(id+"F0.wireOp",EDGE,"E3.4"),sQuery(id+"F0.wireOp",EDGE,"E3.5"),sQuery(id+"F0.wireOp",EDGE,"E11"),sQuery(id+"F0.wireOp",EDGE,"E12"),sQuery(id+"F0.wireOp",EDGE,"E13"),sQuery(id+"F0.wireOp",EDGE,"E14"),subQ1,subQ0,sQuery(id+"F0.wireOp",EDGE,"E17"),sQuery(id+"F0.wireOp",EDGE,"fGXXUOoa-G3to-nFfg-Xp41-Spi5BgRDYh0n"),sQuery(id+"F0.wireOp",EDGE,"maiLpuxs-2Sfq-8eKx-MEtN-jPa1VSy1aRe3"),sQuery(id+"F0.wireOp",EDGE,"E19"),sQuery(id+"F0.wireOp",EDGE,"TkPDQIJV-pblC-kMUo-zlvk-0mYhqbRm7784"),sQuery(id+"F0.wireOp",EDGE,"A3QQ103k-oBam-uK2f-Ywbn-FOsahd6y3kCF"),sQuery(id+"F0.wireOp",EDGE,"E22"),sQuery(id+"F0.wireOp",EDGE,"O4fUSGsA-sgfy-2hAb-lYRv-adjy5g4jnHMn"),sQuery(id+"F0.wireOp",EDGE,"he4H8z8F-eg87-8e6K-5810-5zuvFcfIEFNb")])],"isStart":true})],"blendedInto":[makeQuery(id+"F1.opExtrude","CAP_FACE",FACE,{"disambiguationData":[OSD([sQuery(id+"F0.wireOp",EDGE,"E0.0"),sQuery(id+"F0.wireOp",EDGE,"E0.2"),sQuery(id+"F0.wireOp",EDGE,"E0.4"),sQuery(id+"F0.wireOp",EDGE,"E1.0"),sQuery(id+"F0.wireOp",EDGE,"E1.2"),sQuery(id+"F0.wireOp",EDGE,"E1.3"),sQuery(id+"F0.wireOp",EDGE,"E1.4"),sQuery(id+"F0.wireOp",EDGE,"E1.5"),sQuery(id+"F0.wireOp",EDGE,"E2.0"),sQuery(id+"F0.wireOp",EDGE,"E2.1"),sQuery(id+"F0.wireOp",EDGE,"E2.2"),sQuery(id+"F0.wireOp",EDGE,"E2.3"),sQuery(id+"F0.wireOp",EDGE,"E2.4"),sQuery(id+"F0.wireOp",EDGE,"E3.0"),sQuery(id+"F0.wireOp",EDGE,"E3.1"),sQuery(id+"F0.wireOp",EDGE,"E3.2"),sQuery(id+"F0.wireOp",EDGE,"E3.4"),sQuery(id+"F0.wireOp",EDGE,"E3.5"),sQuery(id+"F0.wireOp",EDGE,"E11"),sQuery(id+"F0.wireOp",EDGE,"E12"),sQuery(id+"F0.wireOp",EDGE,"E13"),sQuery(id+"F0.wireOp",EDGE,"E14"),subQ1,subQ0,sQuery(id+"F0.wireOp",EDGE,"E17"),sQuery(id+"F0.wireOp",EDGE,"fGXXUOoa-G3to-nFfg-Xp41-Spi5BgRDYh0n"),sQuery(id+"F0.wireOp",EDGE,"maiLpuxs-2Sfq-8eKx-MEtN-jPa1VSy1aRe3"),sQuery(id+"F0.wireOp",EDGE,"E19"),sQuery(id+"F0.wireOp",EDGE,"TkPDQIJV-pblC-kMUo-zlvk-0mYhqbRm7784"),sQuery(id+"F0.wireOp",EDGE,"A3QQ103k-oBam-uK2f-Ywbn-FOsahd6y3kCF"),sQuery(id+"F0.wireOp",EDGE,"E22"),sQuery(id+"F0.wireOp",EDGE,"O4fUSGsA-sgfy-2hAb-lYRv-adjy5g4jnHMn"),sQuery(id+"F0.wireOp",EDGE,"he4H8z8F-eg87-8e6K-5810-5zuvFcfIEFNb")])],"isStart":true})]});}
            var Q46;
            Q46=makeQuery(id+"F1.opExtrude","CAP_EDGE",EDGE,{"disambiguationData":[OSD([sQuery(id+"F0.wireOp",EDGE,"E15")])],"isStart":true});
            var Q47;
            {var subQ0=sQuery(id+"F0.wireOp",EDGE,"E1.2");var subQ1=sQuery(id+"F0.wireOp",EDGE,"E0.4");Q47=makeQuery(id+"F11.opFillet","BLEND_EDGE",EDGE,{"blendedFrom":[makeQuery(id+"F1.opExtrude","SWEPT_EDGE",EDGE,{"disambiguationData":[OSD([subQ1,sQuery(id+"F0.wireOp",EDGE,"E1.1"),subQ0,sQuery(id+"F0.wireOp",EDGE,"E23")])]}),makeQuery(id+"F1.opExtrude","CAP_FACE",FACE,{"disambiguationData":[OSD([sQuery(id+"F0.wireOp",EDGE,"E0.0"),sQuery(id+"F0.wireOp",EDGE,"E0.2"),subQ1,sQuery(id+"F0.wireOp",EDGE,"E1.0"),subQ0,sQuery(id+"F0.wireOp",EDGE,"E1.3"),sQuery(id+"F0.wireOp",EDGE,"E1.4"),sQuery(id+"F0.wireOp",EDGE,"E1.5"),sQuery(id+"F0.wireOp",EDGE,"E2.0"),sQuery(id+"F0.wireOp",EDGE,"E2.1"),sQuery(id+"F0.wireOp",EDGE,"E2.2"),sQuery(id+"F0.wireOp",EDGE,"E2.3"),sQuery(id+"F0.wireOp",EDGE,"E2.4"),sQuery(id+"F0.wireOp",EDGE,"E3.0"),sQuery(id+"F0.wireOp",EDGE,"E3.1"),sQuery(id+"F0.wireOp",EDGE,"E3.2"),sQuery(id+"F0.wireOp",EDGE,"E3.4"),sQuery(id+"F0.wireOp",EDGE,"E3.5"),sQuery(id+"F0.wireOp",EDGE,"E11"),sQuery(id+"F0.wireOp",EDGE,"E12"),sQuery(id+"F0.wireOp",EDGE,"E13"),sQuery(id+"F0.wireOp",EDGE,"E14"),sQuery(id+"F0.wireOp",EDGE,"E15"),sQuery(id+"F0.wireOp",EDGE,"E16"),sQuery(id+"F0.wireOp",EDGE,"E17"),sQuery(id+"F0.wireOp",EDGE,"fGXXUOoa-G3to-nFfg-Xp41-Spi5BgRDYh0n"),sQuery(id+"F0.wireOp",EDGE,"maiLpuxs-2Sfq-8eKx-MEtN-jPa1VSy1aRe3"),sQuery(id+"F0.wireOp",EDGE,"E19"),sQuery(id+"F0.wireOp",EDGE,"TkPDQIJV-pblC-kMUo-zlvk-0mYhqbRm7784"),sQuery(id+"F0.wireOp",EDGE,"A3QQ103k-oBam-uK2f-Ywbn-FOsahd6y3kCF"),sQuery(id+"F0.wireOp",EDGE,"E22"),sQuery(id+"F0.wireOp",EDGE,"O4fUSGsA-sgfy-2hAb-lYRv-adjy5g4jnHMn"),sQuery(id+"F0.wireOp",EDGE,"he4H8z8F-eg87-8e6K-5810-5zuvFcfIEFNb")])],"isStart":true})],"blendedInto":[makeQuery(id+"F1.opExtrude","CAP_FACE",FACE,{"disambiguationData":[OSD([sQuery(id+"F0.wireOp",EDGE,"E0.0"),sQuery(id+"F0.wireOp",EDGE,"E0.2"),subQ1,sQuery(id+"F0.wireOp",EDGE,"E1.0"),subQ0,sQuery(id+"F0.wireOp",EDGE,"E1.3"),sQuery(id+"F0.wireOp",EDGE,"E1.4"),sQuery(id+"F0.wireOp",EDGE,"E1.5"),sQuery(id+"F0.wireOp",EDGE,"E2.0"),sQuery(id+"F0.wireOp",EDGE,"E2.1"),sQuery(id+"F0.wireOp",EDGE,"E2.2"),sQuery(id+"F0.wireOp",EDGE,"E2.3"),sQuery(id+"F0.wireOp",EDGE,"E2.4"),sQuery(id+"F0.wireOp",EDGE,"E3.0"),sQuery(id+"F0.wireOp",EDGE,"E3.1"),sQuery(id+"F0.wireOp",EDGE,"E3.2"),sQuery(id+"F0.wireOp",EDGE,"E3.4"),sQuery(id+"F0.wireOp",EDGE,"E3.5"),sQuery(id+"F0.wireOp",EDGE,"E11"),sQuery(id+"F0.wireOp",EDGE,"E12"),sQuery(id+"F0.wireOp",EDGE,"E13"),sQuery(id+"F0.wireOp",EDGE,"E14"),sQuery(id+"F0.wireOp",EDGE,"E15"),sQuery(id+"F0.wireOp",EDGE,"E16"),sQuery(id+"F0.wireOp",EDGE,"E17"),sQuery(id+"F0.wireOp",EDGE,"fGXXUOoa-G3to-nFfg-Xp41-Spi5BgRDYh0n"),sQuery(id+"F0.wireOp",EDGE,"maiLpuxs-2Sfq-8eKx-MEtN-jPa1VSy1aRe3"),sQuery(id+"F0.wireOp",EDGE,"E19"),sQuery(id+"F0.wireOp",EDGE,"TkPDQIJV-pblC-kMUo-zlvk-0mYhqbRm7784"),sQuery(id+"F0.wireOp",EDGE,"A3QQ103k-oBam-uK2f-Ywbn-FOsahd6y3kCF"),sQuery(id+"F0.wireOp",EDGE,"E22"),sQuery(id+"F0.wireOp",EDGE,"O4fUSGsA-sgfy-2hAb-lYRv-adjy5g4jnHMn"),sQuery(id+"F0.wireOp",EDGE,"he4H8z8F-eg87-8e6K-5810-5zuvFcfIEFNb")])],"isStart":true})]});}
            var Q48;
            Q48=makeQuery(id+"F1.opExtrude","CAP_EDGE",EDGE,{"disambiguationData":[OSD([sQuery(id+"F0.wireOp",EDGE,"E1.2")])],"isStart":true});
            var Q49;
            Q49=makeQuery(id+"F1.opExtrude","CAP_EDGE",EDGE,{"disambiguationData":[OSD([sQuery(id+"F0.wireOp",EDGE,"E0.4")])],"isStart":true});
            var Q50;
            {var subQ0=sQuery(id+"F0.wireOp",EDGE,"E2.4");var subQ1=sQuery(id+"F0.wireOp",EDGE,"E0.4");Q50=makeQuery(id+"F11.opFillet","BLEND_EDGE",EDGE,{"blendedFrom":[makeQuery(id+"F1.opExtrude","SWEPT_EDGE",EDGE,{"disambiguationData":[OSD([subQ1,subQ0,sQuery(id+"F0.wireOp",EDGE,"E2.5")])]}),makeQuery(id+"F1.opExtrude","CAP_FACE",FACE,{"disambiguationData":[OSD([sQuery(id+"F0.wireOp",EDGE,"E0.0"),sQuery(id+"F0.wireOp",EDGE,"E0.2"),subQ1,sQuery(id+"F0.wireOp",EDGE,"E1.0"),sQuery(id+"F0.wireOp",EDGE,"E1.2"),sQuery(id+"F0.wireOp",EDGE,"E1.3"),sQuery(id+"F0.wireOp",EDGE,"E1.4"),sQuery(id+"F0.wireOp",EDGE,"E1.5"),sQuery(id+"F0.wireOp",EDGE,"E2.0"),sQuery(id+"F0.wireOp",EDGE,"E2.1"),sQuery(id+"F0.wireOp",EDGE,"E2.2"),sQuery(id+"F0.wireOp",EDGE,"E2.3"),subQ0,sQuery(id+"F0.wireOp",EDGE,"E3.0"),sQuery(id+"F0.wireOp",EDGE,"E3.1"),sQuery(id+"F0.wireOp",EDGE,"E3.2"),sQuery(id+"F0.wireOp",EDGE,"E3.4"),sQuery(id+"F0.wireOp",EDGE,"E3.5"),sQuery(id+"F0.wireOp",EDGE,"E11"),sQuery(id+"F0.wireOp",EDGE,"E12"),sQuery(id+"F0.wireOp",EDGE,"E13"),sQuery(id+"F0.wireOp",EDGE,"E14"),sQuery(id+"F0.wireOp",EDGE,"E15"),sQuery(id+"F0.wireOp",EDGE,"E16"),sQuery(id+"F0.wireOp",EDGE,"E17"),sQuery(id+"F0.wireOp",EDGE,"fGXXUOoa-G3to-nFfg-Xp41-Spi5BgRDYh0n"),sQuery(id+"F0.wireOp",EDGE,"maiLpuxs-2Sfq-8eKx-MEtN-jPa1VSy1aRe3"),sQuery(id+"F0.wireOp",EDGE,"E19"),sQuery(id+"F0.wireOp",EDGE,"TkPDQIJV-pblC-kMUo-zlvk-0mYhqbRm7784"),sQuery(id+"F0.wireOp",EDGE,"A3QQ103k-oBam-uK2f-Ywbn-FOsahd6y3kCF"),sQuery(id+"F0.wireOp",EDGE,"E22"),sQuery(id+"F0.wireOp",EDGE,"O4fUSGsA-sgfy-2hAb-lYRv-adjy5g4jnHMn"),sQuery(id+"F0.wireOp",EDGE,"he4H8z8F-eg87-8e6K-5810-5zuvFcfIEFNb")])],"isStart":true})],"blendedInto":[makeQuery(id+"F1.opExtrude","CAP_FACE",FACE,{"disambiguationData":[OSD([sQuery(id+"F0.wireOp",EDGE,"E0.0"),sQuery(id+"F0.wireOp",EDGE,"E0.2"),subQ1,sQuery(id+"F0.wireOp",EDGE,"E1.0"),sQuery(id+"F0.wireOp",EDGE,"E1.2"),sQuery(id+"F0.wireOp",EDGE,"E1.3"),sQuery(id+"F0.wireOp",EDGE,"E1.4"),sQuery(id+"F0.wireOp",EDGE,"E1.5"),sQuery(id+"F0.wireOp",EDGE,"E2.0"),sQuery(id+"F0.wireOp",EDGE,"E2.1"),sQuery(id+"F0.wireOp",EDGE,"E2.2"),sQuery(id+"F0.wireOp",EDGE,"E2.3"),subQ0,sQuery(id+"F0.wireOp",EDGE,"E3.0"),sQuery(id+"F0.wireOp",EDGE,"E3.1"),sQuery(id+"F0.wireOp",EDGE,"E3.2"),sQuery(id+"F0.wireOp",EDGE,"E3.4"),sQuery(id+"F0.wireOp",EDGE,"E3.5"),sQuery(id+"F0.wireOp",EDGE,"E11"),sQuery(id+"F0.wireOp",EDGE,"E12"),sQuery(id+"F0.wireOp",EDGE,"E13"),sQuery(id+"F0.wireOp",EDGE,"E14"),sQuery(id+"F0.wireOp",EDGE,"E15"),sQuery(id+"F0.wireOp",EDGE,"E16"),sQuery(id+"F0.wireOp",EDGE,"E17"),sQuery(id+"F0.wireOp",EDGE,"fGXXUOoa-G3to-nFfg-Xp41-Spi5BgRDYh0n"),sQuery(id+"F0.wireOp",EDGE,"maiLpuxs-2Sfq-8eKx-MEtN-jPa1VSy1aRe3"),sQuery(id+"F0.wireOp",EDGE,"E19"),sQuery(id+"F0.wireOp",EDGE,"TkPDQIJV-pblC-kMUo-zlvk-0mYhqbRm7784"),sQuery(id+"F0.wireOp",EDGE,"A3QQ103k-oBam-uK2f-Ywbn-FOsahd6y3kCF"),sQuery(id+"F0.wireOp",EDGE,"E22"),sQuery(id+"F0.wireOp",EDGE,"O4fUSGsA-sgfy-2hAb-lYRv-adjy5g4jnHMn"),sQuery(id+"F0.wireOp",EDGE,"he4H8z8F-eg87-8e6K-5810-5zuvFcfIEFNb")])],"isStart":true})]});}
            var Q51;
            Q51=makeQuery(id+"F1.opExtrude","CAP_EDGE",EDGE,{"disambiguationData":[OSD([sQuery(id+"F0.wireOp",EDGE,"E2.4")])],"isStart":true});
            var Q52;
            {var subQ0=sQuery(id+"F0.wireOp",EDGE,"E2.4");var subQ1=sQuery(id+"F0.wireOp",EDGE,"E2.3");Q52=makeQuery(id+"F11.opFillet","BLEND_EDGE",EDGE,{"blendedFrom":[makeQuery(id+"F1.opExtrude","SWEPT_EDGE",EDGE,{"disambiguationData":[OSD([subQ1,subQ0])]}),makeQuery(id+"F1.opExtrude","CAP_FACE",FACE,{"disambiguationData":[OSD([sQuery(id+"F0.wireOp",EDGE,"E0.0"),sQuery(id+"F0.wireOp",EDGE,"E0.2"),sQuery(id+"F0.wireOp",EDGE,"E0.4"),sQuery(id+"F0.wireOp",EDGE,"E1.0"),sQuery(id+"F0.wireOp",EDGE,"E1.2"),sQuery(id+"F0.wireOp",EDGE,"E1.3"),sQuery(id+"F0.wireOp",EDGE,"E1.4"),sQuery(id+"F0.wireOp",EDGE,"E1.5"),sQuery(id+"F0.wireOp",EDGE,"E2.0"),sQuery(id+"F0.wireOp",EDGE,"E2.1"),sQuery(id+"F0.wireOp",EDGE,"E2.2"),subQ1,subQ0,sQuery(id+"F0.wireOp",EDGE,"E3.0"),sQuery(id+"F0.wireOp",EDGE,"E3.1"),sQuery(id+"F0.wireOp",EDGE,"E3.2"),sQuery(id+"F0.wireOp",EDGE,"E3.4"),sQuery(id+"F0.wireOp",EDGE,"E3.5"),sQuery(id+"F0.wireOp",EDGE,"E11"),sQuery(id+"F0.wireOp",EDGE,"E12"),sQuery(id+"F0.wireOp",EDGE,"E13"),sQuery(id+"F0.wireOp",EDGE,"E14"),sQuery(id+"F0.wireOp",EDGE,"E15"),sQuery(id+"F0.wireOp",EDGE,"E16"),sQuery(id+"F0.wireOp",EDGE,"E17"),sQuery(id+"F0.wireOp",EDGE,"fGXXUOoa-G3to-nFfg-Xp41-Spi5BgRDYh0n"),sQuery(id+"F0.wireOp",EDGE,"maiLpuxs-2Sfq-8eKx-MEtN-jPa1VSy1aRe3"),sQuery(id+"F0.wireOp",EDGE,"E19"),sQuery(id+"F0.wireOp",EDGE,"TkPDQIJV-pblC-kMUo-zlvk-0mYhqbRm7784"),sQuery(id+"F0.wireOp",EDGE,"A3QQ103k-oBam-uK2f-Ywbn-FOsahd6y3kCF"),sQuery(id+"F0.wireOp",EDGE,"E22"),sQuery(id+"F0.wireOp",EDGE,"O4fUSGsA-sgfy-2hAb-lYRv-adjy5g4jnHMn"),sQuery(id+"F0.wireOp",EDGE,"he4H8z8F-eg87-8e6K-5810-5zuvFcfIEFNb")])],"isStart":true})],"blendedInto":[makeQuery(id+"F1.opExtrude","CAP_FACE",FACE,{"disambiguationData":[OSD([sQuery(id+"F0.wireOp",EDGE,"E0.0"),sQuery(id+"F0.wireOp",EDGE,"E0.2"),sQuery(id+"F0.wireOp",EDGE,"E0.4"),sQuery(id+"F0.wireOp",EDGE,"E1.0"),sQuery(id+"F0.wireOp",EDGE,"E1.2"),sQuery(id+"F0.wireOp",EDGE,"E1.3"),sQuery(id+"F0.wireOp",EDGE,"E1.4"),sQuery(id+"F0.wireOp",EDGE,"E1.5"),sQuery(id+"F0.wireOp",EDGE,"E2.0"),sQuery(id+"F0.wireOp",EDGE,"E2.1"),sQuery(id+"F0.wireOp",EDGE,"E2.2"),subQ1,subQ0,sQuery(id+"F0.wireOp",EDGE,"E3.0"),sQuery(id+"F0.wireOp",EDGE,"E3.1"),sQuery(id+"F0.wireOp",EDGE,"E3.2"),sQuery(id+"F0.wireOp",EDGE,"E3.4"),sQuery(id+"F0.wireOp",EDGE,"E3.5"),sQuery(id+"F0.wireOp",EDGE,"E11"),sQuery(id+"F0.wireOp",EDGE,"E12"),sQuery(id+"F0.wireOp",EDGE,"E13"),sQuery(id+"F0.wireOp",EDGE,"E14"),sQuery(id+"F0.wireOp",EDGE,"E15"),sQuery(id+"F0.wireOp",EDGE,"E16"),sQuery(id+"F0.wireOp",EDGE,"E17"),sQuery(id+"F0.wireOp",EDGE,"fGXXUOoa-G3to-nFfg-Xp41-Spi5BgRDYh0n"),sQuery(id+"F0.wireOp",EDGE,"maiLpuxs-2Sfq-8eKx-MEtN-jPa1VSy1aRe3"),sQuery(id+"F0.wireOp",EDGE,"E19"),sQuery(id+"F0.wireOp",EDGE,"TkPDQIJV-pblC-kMUo-zlvk-0mYhqbRm7784"),sQuery(id+"F0.wireOp",EDGE,"A3QQ103k-oBam-uK2f-Ywbn-FOsahd6y3kCF"),sQuery(id+"F0.wireOp",EDGE,"E22"),sQuery(id+"F0.wireOp",EDGE,"O4fUSGsA-sgfy-2hAb-lYRv-adjy5g4jnHMn"),sQuery(id+"F0.wireOp",EDGE,"he4H8z8F-eg87-8e6K-5810-5zuvFcfIEFNb")])],"isStart":true})]});}
            var Q53;
            {var subQ0=sQuery(id+"F0.wireOp",EDGE,"E2.3");var subQ1=sQuery(id+"F0.wireOp",EDGE,"E2.2");Q53=makeQuery(id+"F11.opFillet","BLEND_EDGE",EDGE,{"blendedFrom":[makeQuery(id+"F1.opExtrude","SWEPT_EDGE",EDGE,{"disambiguationData":[OSD([subQ1,subQ0])]}),makeQuery(id+"F1.opExtrude","CAP_FACE",FACE,{"disambiguationData":[OSD([sQuery(id+"F0.wireOp",EDGE,"E0.0"),sQuery(id+"F0.wireOp",EDGE,"E0.2"),sQuery(id+"F0.wireOp",EDGE,"E0.4"),sQuery(id+"F0.wireOp",EDGE,"E1.0"),sQuery(id+"F0.wireOp",EDGE,"E1.2"),sQuery(id+"F0.wireOp",EDGE,"E1.3"),sQuery(id+"F0.wireOp",EDGE,"E1.4"),sQuery(id+"F0.wireOp",EDGE,"E1.5"),sQuery(id+"F0.wireOp",EDGE,"E2.0"),sQuery(id+"F0.wireOp",EDGE,"E2.1"),subQ1,subQ0,sQuery(id+"F0.wireOp",EDGE,"E2.4"),sQuery(id+"F0.wireOp",EDGE,"E3.0"),sQuery(id+"F0.wireOp",EDGE,"E3.1"),sQuery(id+"F0.wireOp",EDGE,"E3.2"),sQuery(id+"F0.wireOp",EDGE,"E3.4"),sQuery(id+"F0.wireOp",EDGE,"E3.5"),sQuery(id+"F0.wireOp",EDGE,"E11"),sQuery(id+"F0.wireOp",EDGE,"E12"),sQuery(id+"F0.wireOp",EDGE,"E13"),sQuery(id+"F0.wireOp",EDGE,"E14"),sQuery(id+"F0.wireOp",EDGE,"E15"),sQuery(id+"F0.wireOp",EDGE,"E16"),sQuery(id+"F0.wireOp",EDGE,"E17"),sQuery(id+"F0.wireOp",EDGE,"fGXXUOoa-G3to-nFfg-Xp41-Spi5BgRDYh0n"),sQuery(id+"F0.wireOp",EDGE,"maiLpuxs-2Sfq-8eKx-MEtN-jPa1VSy1aRe3"),sQuery(id+"F0.wireOp",EDGE,"E19"),sQuery(id+"F0.wireOp",EDGE,"TkPDQIJV-pblC-kMUo-zlvk-0mYhqbRm7784"),sQuery(id+"F0.wireOp",EDGE,"A3QQ103k-oBam-uK2f-Ywbn-FOsahd6y3kCF"),sQuery(id+"F0.wireOp",EDGE,"E22"),sQuery(id+"F0.wireOp",EDGE,"O4fUSGsA-sgfy-2hAb-lYRv-adjy5g4jnHMn"),sQuery(id+"F0.wireOp",EDGE,"he4H8z8F-eg87-8e6K-5810-5zuvFcfIEFNb")])],"isStart":true})],"blendedInto":[makeQuery(id+"F1.opExtrude","CAP_FACE",FACE,{"disambiguationData":[OSD([sQuery(id+"F0.wireOp",EDGE,"E0.0"),sQuery(id+"F0.wireOp",EDGE,"E0.2"),sQuery(id+"F0.wireOp",EDGE,"E0.4"),sQuery(id+"F0.wireOp",EDGE,"E1.0"),sQuery(id+"F0.wireOp",EDGE,"E1.2"),sQuery(id+"F0.wireOp",EDGE,"E1.3"),sQuery(id+"F0.wireOp",EDGE,"E1.4"),sQuery(id+"F0.wireOp",EDGE,"E1.5"),sQuery(id+"F0.wireOp",EDGE,"E2.0"),sQuery(id+"F0.wireOp",EDGE,"E2.1"),subQ1,subQ0,sQuery(id+"F0.wireOp",EDGE,"E2.4"),sQuery(id+"F0.wireOp",EDGE,"E3.0"),sQuery(id+"F0.wireOp",EDGE,"E3.1"),sQuery(id+"F0.wireOp",EDGE,"E3.2"),sQuery(id+"F0.wireOp",EDGE,"E3.4"),sQuery(id+"F0.wireOp",EDGE,"E3.5"),sQuery(id+"F0.wireOp",EDGE,"E11"),sQuery(id+"F0.wireOp",EDGE,"E12"),sQuery(id+"F0.wireOp",EDGE,"E13"),sQuery(id+"F0.wireOp",EDGE,"E14"),sQuery(id+"F0.wireOp",EDGE,"E15"),sQuery(id+"F0.wireOp",EDGE,"E16"),sQuery(id+"F0.wireOp",EDGE,"E17"),sQuery(id+"F0.wireOp",EDGE,"fGXXUOoa-G3to-nFfg-Xp41-Spi5BgRDYh0n"),sQuery(id+"F0.wireOp",EDGE,"maiLpuxs-2Sfq-8eKx-MEtN-jPa1VSy1aRe3"),sQuery(id+"F0.wireOp",EDGE,"E19"),sQuery(id+"F0.wireOp",EDGE,"TkPDQIJV-pblC-kMUo-zlvk-0mYhqbRm7784"),sQuery(id+"F0.wireOp",EDGE,"A3QQ103k-oBam-uK2f-Ywbn-FOsahd6y3kCF"),sQuery(id+"F0.wireOp",EDGE,"E22"),sQuery(id+"F0.wireOp",EDGE,"O4fUSGsA-sgfy-2hAb-lYRv-adjy5g4jnHMn"),sQuery(id+"F0.wireOp",EDGE,"he4H8z8F-eg87-8e6K-5810-5zuvFcfIEFNb")])],"isStart":true})]});}
            var Q54;
            Q54=makeQuery(id+"F1.opExtrude","CAP_EDGE",EDGE,{"disambiguationData":[OSD([sQuery(id+"F0.wireOp",EDGE,"E2.2")])],"isStart":true});
            var Q55;
            {var subQ0=sQuery(id+"F0.wireOp",EDGE,"E2.2");var subQ1=sQuery(id+"F0.wireOp",EDGE,"E2.1");Q55=makeQuery(id+"F11.opFillet","BLEND_EDGE",EDGE,{"blendedFrom":[makeQuery(id+"F1.opExtrude","SWEPT_EDGE",EDGE,{"disambiguationData":[OSD([subQ1,subQ0])]}),makeQuery(id+"F1.opExtrude","CAP_FACE",FACE,{"disambiguationData":[OSD([sQuery(id+"F0.wireOp",EDGE,"E0.0"),sQuery(id+"F0.wireOp",EDGE,"E0.2"),sQuery(id+"F0.wireOp",EDGE,"E0.4"),sQuery(id+"F0.wireOp",EDGE,"E1.0"),sQuery(id+"F0.wireOp",EDGE,"E1.2"),sQuery(id+"F0.wireOp",EDGE,"E1.3"),sQuery(id+"F0.wireOp",EDGE,"E1.4"),sQuery(id+"F0.wireOp",EDGE,"E1.5"),sQuery(id+"F0.wireOp",EDGE,"E2.0"),subQ1,subQ0,sQuery(id+"F0.wireOp",EDGE,"E2.3"),sQuery(id+"F0.wireOp",EDGE,"E2.4"),sQuery(id+"F0.wireOp",EDGE,"E3.0"),sQuery(id+"F0.wireOp",EDGE,"E3.1"),sQuery(id+"F0.wireOp",EDGE,"E3.2"),sQuery(id+"F0.wireOp",EDGE,"E3.4"),sQuery(id+"F0.wireOp",EDGE,"E3.5"),sQuery(id+"F0.wireOp",EDGE,"E11"),sQuery(id+"F0.wireOp",EDGE,"E12"),sQuery(id+"F0.wireOp",EDGE,"E13"),sQuery(id+"F0.wireOp",EDGE,"E14"),sQuery(id+"F0.wireOp",EDGE,"E15"),sQuery(id+"F0.wireOp",EDGE,"E16"),sQuery(id+"F0.wireOp",EDGE,"E17"),sQuery(id+"F0.wireOp",EDGE,"fGXXUOoa-G3to-nFfg-Xp41-Spi5BgRDYh0n"),sQuery(id+"F0.wireOp",EDGE,"maiLpuxs-2Sfq-8eKx-MEtN-jPa1VSy1aRe3"),sQuery(id+"F0.wireOp",EDGE,"E19"),sQuery(id+"F0.wireOp",EDGE,"TkPDQIJV-pblC-kMUo-zlvk-0mYhqbRm7784"),sQuery(id+"F0.wireOp",EDGE,"A3QQ103k-oBam-uK2f-Ywbn-FOsahd6y3kCF"),sQuery(id+"F0.wireOp",EDGE,"E22"),sQuery(id+"F0.wireOp",EDGE,"O4fUSGsA-sgfy-2hAb-lYRv-adjy5g4jnHMn"),sQuery(id+"F0.wireOp",EDGE,"he4H8z8F-eg87-8e6K-5810-5zuvFcfIEFNb")])],"isStart":true})],"blendedInto":[makeQuery(id+"F1.opExtrude","CAP_FACE",FACE,{"disambiguationData":[OSD([sQuery(id+"F0.wireOp",EDGE,"E0.0"),sQuery(id+"F0.wireOp",EDGE,"E0.2"),sQuery(id+"F0.wireOp",EDGE,"E0.4"),sQuery(id+"F0.wireOp",EDGE,"E1.0"),sQuery(id+"F0.wireOp",EDGE,"E1.2"),sQuery(id+"F0.wireOp",EDGE,"E1.3"),sQuery(id+"F0.wireOp",EDGE,"E1.4"),sQuery(id+"F0.wireOp",EDGE,"E1.5"),sQuery(id+"F0.wireOp",EDGE,"E2.0"),subQ1,subQ0,sQuery(id+"F0.wireOp",EDGE,"E2.3"),sQuery(id+"F0.wireOp",EDGE,"E2.4"),sQuery(id+"F0.wireOp",EDGE,"E3.0"),sQuery(id+"F0.wireOp",EDGE,"E3.1"),sQuery(id+"F0.wireOp",EDGE,"E3.2"),sQuery(id+"F0.wireOp",EDGE,"E3.4"),sQuery(id+"F0.wireOp",EDGE,"E3.5"),sQuery(id+"F0.wireOp",EDGE,"E11"),sQuery(id+"F0.wireOp",EDGE,"E12"),sQuery(id+"F0.wireOp",EDGE,"E13"),sQuery(id+"F0.wireOp",EDGE,"E14"),sQuery(id+"F0.wireOp",EDGE,"E15"),sQuery(id+"F0.wireOp",EDGE,"E16"),sQuery(id+"F0.wireOp",EDGE,"E17"),sQuery(id+"F0.wireOp",EDGE,"fGXXUOoa-G3to-nFfg-Xp41-Spi5BgRDYh0n"),sQuery(id+"F0.wireOp",EDGE,"maiLpuxs-2Sfq-8eKx-MEtN-jPa1VSy1aRe3"),sQuery(id+"F0.wireOp",EDGE,"E19"),sQuery(id+"F0.wireOp",EDGE,"TkPDQIJV-pblC-kMUo-zlvk-0mYhqbRm7784"),sQuery(id+"F0.wireOp",EDGE,"A3QQ103k-oBam-uK2f-Ywbn-FOsahd6y3kCF"),sQuery(id+"F0.wireOp",EDGE,"E22"),sQuery(id+"F0.wireOp",EDGE,"O4fUSGsA-sgfy-2hAb-lYRv-adjy5g4jnHMn"),sQuery(id+"F0.wireOp",EDGE,"he4H8z8F-eg87-8e6K-5810-5zuvFcfIEFNb")])],"isStart":true})]});}
            var Q56;
            Q56=makeQuery(id+"F1.opExtrude","CAP_EDGE",EDGE,{"disambiguationData":[OSD([sQuery(id+"F0.wireOp",EDGE,"E2.1")])],"isStart":true});
            var Q57;
            Q57=makeQuery(id+"F1.opExtrude","CAP_EDGE",EDGE,{"disambiguationData":[OSD([sQuery(id+"F0.wireOp",EDGE,"E11")])],"isStart":true});
            var Q58;
            {var subQ0=sQuery(id+"F0.wireOp",EDGE,"E12");var subQ1=sQuery(id+"F0.wireOp",EDGE,"E11");Q58=makeQuery(id+"F12.opFillet","BLEND_EDGE",EDGE,{"blendedFrom":[makeQuery(id+"F1.opExtrude","SWEPT_EDGE",EDGE,{"disambiguationData":[OSD([sQuery(id+"F0.wireOp",EDGE,"E8"),subQ1,subQ0])]}),makeQuery(id+"F1.opExtrude","CAP_FACE",FACE,{"disambiguationData":[OSD([sQuery(id+"F0.wireOp",EDGE,"E0.0"),sQuery(id+"F0.wireOp",EDGE,"E0.2"),sQuery(id+"F0.wireOp",EDGE,"E0.4"),sQuery(id+"F0.wireOp",EDGE,"E1.0"),sQuery(id+"F0.wireOp",EDGE,"E1.2"),sQuery(id+"F0.wireOp",EDGE,"E1.3"),sQuery(id+"F0.wireOp",EDGE,"E1.4"),sQuery(id+"F0.wireOp",EDGE,"E1.5"),sQuery(id+"F0.wireOp",EDGE,"E2.0"),sQuery(id+"F0.wireOp",EDGE,"E2.1"),sQuery(id+"F0.wireOp",EDGE,"E2.2"),sQuery(id+"F0.wireOp",EDGE,"E2.3"),sQuery(id+"F0.wireOp",EDGE,"E2.4"),sQuery(id+"F0.wireOp",EDGE,"E3.0"),sQuery(id+"F0.wireOp",EDGE,"E3.1"),sQuery(id+"F0.wireOp",EDGE,"E3.2"),sQuery(id+"F0.wireOp",EDGE,"E3.4"),sQuery(id+"F0.wireOp",EDGE,"E3.5"),subQ1,subQ0,sQuery(id+"F0.wireOp",EDGE,"E13"),sQuery(id+"F0.wireOp",EDGE,"E14"),sQuery(id+"F0.wireOp",EDGE,"E15"),sQuery(id+"F0.wireOp",EDGE,"E16"),sQuery(id+"F0.wireOp",EDGE,"E17"),sQuery(id+"F0.wireOp",EDGE,"fGXXUOoa-G3to-nFfg-Xp41-Spi5BgRDYh0n"),sQuery(id+"F0.wireOp",EDGE,"maiLpuxs-2Sfq-8eKx-MEtN-jPa1VSy1aRe3"),sQuery(id+"F0.wireOp",EDGE,"E19"),sQuery(id+"F0.wireOp",EDGE,"TkPDQIJV-pblC-kMUo-zlvk-0mYhqbRm7784"),sQuery(id+"F0.wireOp",EDGE,"A3QQ103k-oBam-uK2f-Ywbn-FOsahd6y3kCF"),sQuery(id+"F0.wireOp",EDGE,"E22"),sQuery(id+"F0.wireOp",EDGE,"O4fUSGsA-sgfy-2hAb-lYRv-adjy5g4jnHMn"),sQuery(id+"F0.wireOp",EDGE,"he4H8z8F-eg87-8e6K-5810-5zuvFcfIEFNb")])],"isStart":true})],"blendedInto":[makeQuery(id+"F1.opExtrude","CAP_FACE",FACE,{"disambiguationData":[OSD([sQuery(id+"F0.wireOp",EDGE,"E0.0"),sQuery(id+"F0.wireOp",EDGE,"E0.2"),sQuery(id+"F0.wireOp",EDGE,"E0.4"),sQuery(id+"F0.wireOp",EDGE,"E1.0"),sQuery(id+"F0.wireOp",EDGE,"E1.2"),sQuery(id+"F0.wireOp",EDGE,"E1.3"),sQuery(id+"F0.wireOp",EDGE,"E1.4"),sQuery(id+"F0.wireOp",EDGE,"E1.5"),sQuery(id+"F0.wireOp",EDGE,"E2.0"),sQuery(id+"F0.wireOp",EDGE,"E2.1"),sQuery(id+"F0.wireOp",EDGE,"E2.2"),sQuery(id+"F0.wireOp",EDGE,"E2.3"),sQuery(id+"F0.wireOp",EDGE,"E2.4"),sQuery(id+"F0.wireOp",EDGE,"E3.0"),sQuery(id+"F0.wireOp",EDGE,"E3.1"),sQuery(id+"F0.wireOp",EDGE,"E3.2"),sQuery(id+"F0.wireOp",EDGE,"E3.4"),sQuery(id+"F0.wireOp",EDGE,"E3.5"),subQ1,subQ0,sQuery(id+"F0.wireOp",EDGE,"E13"),sQuery(id+"F0.wireOp",EDGE,"E14"),sQuery(id+"F0.wireOp",EDGE,"E15"),sQuery(id+"F0.wireOp",EDGE,"E16"),sQuery(id+"F0.wireOp",EDGE,"E17"),sQuery(id+"F0.wireOp",EDGE,"fGXXUOoa-G3to-nFfg-Xp41-Spi5BgRDYh0n"),sQuery(id+"F0.wireOp",EDGE,"maiLpuxs-2Sfq-8eKx-MEtN-jPa1VSy1aRe3"),sQuery(id+"F0.wireOp",EDGE,"E19"),sQuery(id+"F0.wireOp",EDGE,"TkPDQIJV-pblC-kMUo-zlvk-0mYhqbRm7784"),sQuery(id+"F0.wireOp",EDGE,"A3QQ103k-oBam-uK2f-Ywbn-FOsahd6y3kCF"),sQuery(id+"F0.wireOp",EDGE,"E22"),sQuery(id+"F0.wireOp",EDGE,"O4fUSGsA-sgfy-2hAb-lYRv-adjy5g4jnHMn"),sQuery(id+"F0.wireOp",EDGE,"he4H8z8F-eg87-8e6K-5810-5zuvFcfIEFNb")])],"isStart":true})]});}
            var Q59;
            Q59=makeQuery(id+"F1.opExtrude","CAP_EDGE",EDGE,{"disambiguationData":[OSD([sQuery(id+"F0.wireOp",EDGE,"E12")])],"isStart":true});
            var Q60;
            {var subQ0=sQuery(id+"F0.wireOp",EDGE,"E2.0");var subQ1=sQuery(id+"F0.wireOp",EDGE,"E0.2");Q60=makeQuery(id+"F11.opFillet","BLEND_EDGE",EDGE,{"blendedFrom":[makeQuery(id+"F1.opExtrude","SWEPT_EDGE",EDGE,{"disambiguationData":[OSD([subQ1,subQ0,sQuery(id+"F0.wireOp",EDGE,"E2.5"),sQuery(id+"F0.wireOp",EDGE,"E20")])]}),makeQuery(id+"F1.opExtrude","CAP_FACE",FACE,{"disambiguationData":[OSD([sQuery(id+"F0.wireOp",EDGE,"E0.0"),subQ1,sQuery(id+"F0.wireOp",EDGE,"E0.4"),sQuery(id+"F0.wireOp",EDGE,"E1.0"),sQuery(id+"F0.wireOp",EDGE,"E1.2"),sQuery(id+"F0.wireOp",EDGE,"E1.3"),sQuery(id+"F0.wireOp",EDGE,"E1.4"),sQuery(id+"F0.wireOp",EDGE,"E1.5"),subQ0,sQuery(id+"F0.wireOp",EDGE,"E2.1"),sQuery(id+"F0.wireOp",EDGE,"E2.2"),sQuery(id+"F0.wireOp",EDGE,"E2.3"),sQuery(id+"F0.wireOp",EDGE,"E2.4"),sQuery(id+"F0.wireOp",EDGE,"E3.0"),sQuery(id+"F0.wireOp",EDGE,"E3.1"),sQuery(id+"F0.wireOp",EDGE,"E3.2"),sQuery(id+"F0.wireOp",EDGE,"E3.4"),sQuery(id+"F0.wireOp",EDGE,"E3.5"),sQuery(id+"F0.wireOp",EDGE,"E11"),sQuery(id+"F0.wireOp",EDGE,"E12"),sQuery(id+"F0.wireOp",EDGE,"E13"),sQuery(id+"F0.wireOp",EDGE,"E14"),sQuery(id+"F0.wireOp",EDGE,"E15"),sQuery(id+"F0.wireOp",EDGE,"E16"),sQuery(id+"F0.wireOp",EDGE,"E17"),sQuery(id+"F0.wireOp",EDGE,"fGXXUOoa-G3to-nFfg-Xp41-Spi5BgRDYh0n"),sQuery(id+"F0.wireOp",EDGE,"maiLpuxs-2Sfq-8eKx-MEtN-jPa1VSy1aRe3"),sQuery(id+"F0.wireOp",EDGE,"E19"),sQuery(id+"F0.wireOp",EDGE,"TkPDQIJV-pblC-kMUo-zlvk-0mYhqbRm7784"),sQuery(id+"F0.wireOp",EDGE,"A3QQ103k-oBam-uK2f-Ywbn-FOsahd6y3kCF"),sQuery(id+"F0.wireOp",EDGE,"E22"),sQuery(id+"F0.wireOp",EDGE,"O4fUSGsA-sgfy-2hAb-lYRv-adjy5g4jnHMn"),sQuery(id+"F0.wireOp",EDGE,"he4H8z8F-eg87-8e6K-5810-5zuvFcfIEFNb")])],"isStart":true})],"blendedInto":[makeQuery(id+"F1.opExtrude","CAP_FACE",FACE,{"disambiguationData":[OSD([sQuery(id+"F0.wireOp",EDGE,"E0.0"),subQ1,sQuery(id+"F0.wireOp",EDGE,"E0.4"),sQuery(id+"F0.wireOp",EDGE,"E1.0"),sQuery(id+"F0.wireOp",EDGE,"E1.2"),sQuery(id+"F0.wireOp",EDGE,"E1.3"),sQuery(id+"F0.wireOp",EDGE,"E1.4"),sQuery(id+"F0.wireOp",EDGE,"E1.5"),subQ0,sQuery(id+"F0.wireOp",EDGE,"E2.1"),sQuery(id+"F0.wireOp",EDGE,"E2.2"),sQuery(id+"F0.wireOp",EDGE,"E2.3"),sQuery(id+"F0.wireOp",EDGE,"E2.4"),sQuery(id+"F0.wireOp",EDGE,"E3.0"),sQuery(id+"F0.wireOp",EDGE,"E3.1"),sQuery(id+"F0.wireOp",EDGE,"E3.2"),sQuery(id+"F0.wireOp",EDGE,"E3.4"),sQuery(id+"F0.wireOp",EDGE,"E3.5"),sQuery(id+"F0.wireOp",EDGE,"E11"),sQuery(id+"F0.wireOp",EDGE,"E12"),sQuery(id+"F0.wireOp",EDGE,"E13"),sQuery(id+"F0.wireOp",EDGE,"E14"),sQuery(id+"F0.wireOp",EDGE,"E15"),sQuery(id+"F0.wireOp",EDGE,"E16"),sQuery(id+"F0.wireOp",EDGE,"E17"),sQuery(id+"F0.wireOp",EDGE,"fGXXUOoa-G3to-nFfg-Xp41-Spi5BgRDYh0n"),sQuery(id+"F0.wireOp",EDGE,"maiLpuxs-2Sfq-8eKx-MEtN-jPa1VSy1aRe3"),sQuery(id+"F0.wireOp",EDGE,"E19"),sQuery(id+"F0.wireOp",EDGE,"TkPDQIJV-pblC-kMUo-zlvk-0mYhqbRm7784"),sQuery(id+"F0.wireOp",EDGE,"A3QQ103k-oBam-uK2f-Ywbn-FOsahd6y3kCF"),sQuery(id+"F0.wireOp",EDGE,"E22"),sQuery(id+"F0.wireOp",EDGE,"O4fUSGsA-sgfy-2hAb-lYRv-adjy5g4jnHMn"),sQuery(id+"F0.wireOp",EDGE,"he4H8z8F-eg87-8e6K-5810-5zuvFcfIEFNb")])],"isStart":true})]});}
            var Q61;
            Q61=makeQuery(id+"F1.opExtrude","CAP_EDGE",EDGE,{"disambiguationData":[OSD([sQuery(id+"F0.wireOp",EDGE,"E2.0")])],"isStart":true});
            var Q62;
            Q62=makeQuery(id+"F1.opExtrude","CAP_EDGE",EDGE,{"disambiguationData":[OSD([sQuery(id+"F0.wireOp",EDGE,"E0.2")])],"isStart":true});
            var Q63;
            {var subQ0=sQuery(id+"F0.wireOp",EDGE,"E3.2");var subQ1=sQuery(id+"F0.wireOp",EDGE,"E0.2");Q63=makeQuery(id+"F11.opFillet","BLEND_EDGE",EDGE,{"blendedFrom":[makeQuery(id+"F1.opExtrude","SWEPT_EDGE",EDGE,{"disambiguationData":[OSD([sQuery(id+"F0.wireOp",EDGE,"E0.1"),subQ1,subQ0,sQuery(id+"F0.wireOp",EDGE,"E3.3")])]}),makeQuery(id+"F1.opExtrude","CAP_FACE",FACE,{"disambiguationData":[OSD([sQuery(id+"F0.wireOp",EDGE,"E0.0"),subQ1,sQuery(id+"F0.wireOp",EDGE,"E0.4"),sQuery(id+"F0.wireOp",EDGE,"E1.0"),sQuery(id+"F0.wireOp",EDGE,"E1.2"),sQuery(id+"F0.wireOp",EDGE,"E1.3"),sQuery(id+"F0.wireOp",EDGE,"E1.4"),sQuery(id+"F0.wireOp",EDGE,"E1.5"),sQuery(id+"F0.wireOp",EDGE,"E2.0"),sQuery(id+"F0.wireOp",EDGE,"E2.1"),sQuery(id+"F0.wireOp",EDGE,"E2.2"),sQuery(id+"F0.wireOp",EDGE,"E2.3"),sQuery(id+"F0.wireOp",EDGE,"E2.4"),sQuery(id+"F0.wireOp",EDGE,"E3.0"),sQuery(id+"F0.wireOp",EDGE,"E3.1"),subQ0,sQuery(id+"F0.wireOp",EDGE,"E3.4"),sQuery(id+"F0.wireOp",EDGE,"E3.5"),sQuery(id+"F0.wireOp",EDGE,"E11"),sQuery(id+"F0.wireOp",EDGE,"E12"),sQuery(id+"F0.wireOp",EDGE,"E13"),sQuery(id+"F0.wireOp",EDGE,"E14"),sQuery(id+"F0.wireOp",EDGE,"E15"),sQuery(id+"F0.wireOp",EDGE,"E16"),sQuery(id+"F0.wireOp",EDGE,"E17"),sQuery(id+"F0.wireOp",EDGE,"fGXXUOoa-G3to-nFfg-Xp41-Spi5BgRDYh0n"),sQuery(id+"F0.wireOp",EDGE,"maiLpuxs-2Sfq-8eKx-MEtN-jPa1VSy1aRe3"),sQuery(id+"F0.wireOp",EDGE,"E19"),sQuery(id+"F0.wireOp",EDGE,"TkPDQIJV-pblC-kMUo-zlvk-0mYhqbRm7784"),sQuery(id+"F0.wireOp",EDGE,"A3QQ103k-oBam-uK2f-Ywbn-FOsahd6y3kCF"),sQuery(id+"F0.wireOp",EDGE,"E22"),sQuery(id+"F0.wireOp",EDGE,"O4fUSGsA-sgfy-2hAb-lYRv-adjy5g4jnHMn"),sQuery(id+"F0.wireOp",EDGE,"he4H8z8F-eg87-8e6K-5810-5zuvFcfIEFNb")])],"isStart":true})],"blendedInto":[makeQuery(id+"F1.opExtrude","CAP_FACE",FACE,{"disambiguationData":[OSD([sQuery(id+"F0.wireOp",EDGE,"E0.0"),subQ1,sQuery(id+"F0.wireOp",EDGE,"E0.4"),sQuery(id+"F0.wireOp",EDGE,"E1.0"),sQuery(id+"F0.wireOp",EDGE,"E1.2"),sQuery(id+"F0.wireOp",EDGE,"E1.3"),sQuery(id+"F0.wireOp",EDGE,"E1.4"),sQuery(id+"F0.wireOp",EDGE,"E1.5"),sQuery(id+"F0.wireOp",EDGE,"E2.0"),sQuery(id+"F0.wireOp",EDGE,"E2.1"),sQuery(id+"F0.wireOp",EDGE,"E2.2"),sQuery(id+"F0.wireOp",EDGE,"E2.3"),sQuery(id+"F0.wireOp",EDGE,"E2.4"),sQuery(id+"F0.wireOp",EDGE,"E3.0"),sQuery(id+"F0.wireOp",EDGE,"E3.1"),subQ0,sQuery(id+"F0.wireOp",EDGE,"E3.4"),sQuery(id+"F0.wireOp",EDGE,"E3.5"),sQuery(id+"F0.wireOp",EDGE,"E11"),sQuery(id+"F0.wireOp",EDGE,"E12"),sQuery(id+"F0.wireOp",EDGE,"E13"),sQuery(id+"F0.wireOp",EDGE,"E14"),sQuery(id+"F0.wireOp",EDGE,"E15"),sQuery(id+"F0.wireOp",EDGE,"E16"),sQuery(id+"F0.wireOp",EDGE,"E17"),sQuery(id+"F0.wireOp",EDGE,"fGXXUOoa-G3to-nFfg-Xp41-Spi5BgRDYh0n"),sQuery(id+"F0.wireOp",EDGE,"maiLpuxs-2Sfq-8eKx-MEtN-jPa1VSy1aRe3"),sQuery(id+"F0.wireOp",EDGE,"E19"),sQuery(id+"F0.wireOp",EDGE,"TkPDQIJV-pblC-kMUo-zlvk-0mYhqbRm7784"),sQuery(id+"F0.wireOp",EDGE,"A3QQ103k-oBam-uK2f-Ywbn-FOsahd6y3kCF"),sQuery(id+"F0.wireOp",EDGE,"E22"),sQuery(id+"F0.wireOp",EDGE,"O4fUSGsA-sgfy-2hAb-lYRv-adjy5g4jnHMn"),sQuery(id+"F0.wireOp",EDGE,"he4H8z8F-eg87-8e6K-5810-5zuvFcfIEFNb")])],"isStart":true})]});}
            var Q64;
            Q64=makeQuery(id+"F1.opExtrude","CAP_EDGE",EDGE,{"disambiguationData":[OSD([sQuery(id+"F0.wireOp",EDGE,"E3.2")])],"isStart":true});
            var Q65;
            {var subQ0=sQuery(id+"F0.wireOp",EDGE,"E3.2");var subQ1=sQuery(id+"F0.wireOp",EDGE,"E3.1");Q65=makeQuery(id+"F11.opFillet","BLEND_EDGE",EDGE,{"blendedFrom":[makeQuery(id+"F1.opExtrude","SWEPT_EDGE",EDGE,{"disambiguationData":[OSD([subQ1,subQ0])]}),makeQuery(id+"F1.opExtrude","CAP_FACE",FACE,{"disambiguationData":[OSD([sQuery(id+"F0.wireOp",EDGE,"E0.0"),sQuery(id+"F0.wireOp",EDGE,"E0.2"),sQuery(id+"F0.wireOp",EDGE,"E0.4"),sQuery(id+"F0.wireOp",EDGE,"E1.0"),sQuery(id+"F0.wireOp",EDGE,"E1.2"),sQuery(id+"F0.wireOp",EDGE,"E1.3"),sQuery(id+"F0.wireOp",EDGE,"E1.4"),sQuery(id+"F0.wireOp",EDGE,"E1.5"),sQuery(id+"F0.wireOp",EDGE,"E2.0"),sQuery(id+"F0.wireOp",EDGE,"E2.1"),sQuery(id+"F0.wireOp",EDGE,"E2.2"),sQuery(id+"F0.wireOp",EDGE,"E2.3"),sQuery(id+"F0.wireOp",EDGE,"E2.4"),sQuery(id+"F0.wireOp",EDGE,"E3.0"),subQ1,subQ0,sQuery(id+"F0.wireOp",EDGE,"E3.4"),sQuery(id+"F0.wireOp",EDGE,"E3.5"),sQuery(id+"F0.wireOp",EDGE,"E11"),sQuery(id+"F0.wireOp",EDGE,"E12"),sQuery(id+"F0.wireOp",EDGE,"E13"),sQuery(id+"F0.wireOp",EDGE,"E14"),sQuery(id+"F0.wireOp",EDGE,"E15"),sQuery(id+"F0.wireOp",EDGE,"E16"),sQuery(id+"F0.wireOp",EDGE,"E17"),sQuery(id+"F0.wireOp",EDGE,"fGXXUOoa-G3to-nFfg-Xp41-Spi5BgRDYh0n"),sQuery(id+"F0.wireOp",EDGE,"maiLpuxs-2Sfq-8eKx-MEtN-jPa1VSy1aRe3"),sQuery(id+"F0.wireOp",EDGE,"E19"),sQuery(id+"F0.wireOp",EDGE,"TkPDQIJV-pblC-kMUo-zlvk-0mYhqbRm7784"),sQuery(id+"F0.wireOp",EDGE,"A3QQ103k-oBam-uK2f-Ywbn-FOsahd6y3kCF"),sQuery(id+"F0.wireOp",EDGE,"E22"),sQuery(id+"F0.wireOp",EDGE,"O4fUSGsA-sgfy-2hAb-lYRv-adjy5g4jnHMn"),sQuery(id+"F0.wireOp",EDGE,"he4H8z8F-eg87-8e6K-5810-5zuvFcfIEFNb")])],"isStart":true})],"blendedInto":[makeQuery(id+"F1.opExtrude","CAP_FACE",FACE,{"disambiguationData":[OSD([sQuery(id+"F0.wireOp",EDGE,"E0.0"),sQuery(id+"F0.wireOp",EDGE,"E0.2"),sQuery(id+"F0.wireOp",EDGE,"E0.4"),sQuery(id+"F0.wireOp",EDGE,"E1.0"),sQuery(id+"F0.wireOp",EDGE,"E1.2"),sQuery(id+"F0.wireOp",EDGE,"E1.3"),sQuery(id+"F0.wireOp",EDGE,"E1.4"),sQuery(id+"F0.wireOp",EDGE,"E1.5"),sQuery(id+"F0.wireOp",EDGE,"E2.0"),sQuery(id+"F0.wireOp",EDGE,"E2.1"),sQuery(id+"F0.wireOp",EDGE,"E2.2"),sQuery(id+"F0.wireOp",EDGE,"E2.3"),sQuery(id+"F0.wireOp",EDGE,"E2.4"),sQuery(id+"F0.wireOp",EDGE,"E3.0"),subQ1,subQ0,sQuery(id+"F0.wireOp",EDGE,"E3.4"),sQuery(id+"F0.wireOp",EDGE,"E3.5"),sQuery(id+"F0.wireOp",EDGE,"E11"),sQuery(id+"F0.wireOp",EDGE,"E12"),sQuery(id+"F0.wireOp",EDGE,"E13"),sQuery(id+"F0.wireOp",EDGE,"E14"),sQuery(id+"F0.wireOp",EDGE,"E15"),sQuery(id+"F0.wireOp",EDGE,"E16"),sQuery(id+"F0.wireOp",EDGE,"E17"),sQuery(id+"F0.wireOp",EDGE,"fGXXUOoa-G3to-nFfg-Xp41-Spi5BgRDYh0n"),sQuery(id+"F0.wireOp",EDGE,"maiLpuxs-2Sfq-8eKx-MEtN-jPa1VSy1aRe3"),sQuery(id+"F0.wireOp",EDGE,"E19"),sQuery(id+"F0.wireOp",EDGE,"TkPDQIJV-pblC-kMUo-zlvk-0mYhqbRm7784"),sQuery(id+"F0.wireOp",EDGE,"A3QQ103k-oBam-uK2f-Ywbn-FOsahd6y3kCF"),sQuery(id+"F0.wireOp",EDGE,"E22"),sQuery(id+"F0.wireOp",EDGE,"O4fUSGsA-sgfy-2hAb-lYRv-adjy5g4jnHMn"),sQuery(id+"F0.wireOp",EDGE,"he4H8z8F-eg87-8e6K-5810-5zuvFcfIEFNb")])],"isStart":true})]});}
            var Q66;
            {var subQ0=sQuery(id+"F0.wireOp",EDGE,"E3.1");var subQ1=sQuery(id+"F0.wireOp",EDGE,"E3.0");Q66=makeQuery(id+"F11.opFillet","BLEND_EDGE",EDGE,{"blendedFrom":[makeQuery(id+"F1.opExtrude","SWEPT_EDGE",EDGE,{"disambiguationData":[OSD([subQ1,subQ0])]}),makeQuery(id+"F1.opExtrude","CAP_FACE",FACE,{"disambiguationData":[OSD([sQuery(id+"F0.wireOp",EDGE,"E0.0"),sQuery(id+"F0.wireOp",EDGE,"E0.2"),sQuery(id+"F0.wireOp",EDGE,"E0.4"),sQuery(id+"F0.wireOp",EDGE,"E1.0"),sQuery(id+"F0.wireOp",EDGE,"E1.2"),sQuery(id+"F0.wireOp",EDGE,"E1.3"),sQuery(id+"F0.wireOp",EDGE,"E1.4"),sQuery(id+"F0.wireOp",EDGE,"E1.5"),sQuery(id+"F0.wireOp",EDGE,"E2.0"),sQuery(id+"F0.wireOp",EDGE,"E2.1"),sQuery(id+"F0.wireOp",EDGE,"E2.2"),sQuery(id+"F0.wireOp",EDGE,"E2.3"),sQuery(id+"F0.wireOp",EDGE,"E2.4"),subQ1,subQ0,sQuery(id+"F0.wireOp",EDGE,"E3.2"),sQuery(id+"F0.wireOp",EDGE,"E3.4"),sQuery(id+"F0.wireOp",EDGE,"E3.5"),sQuery(id+"F0.wireOp",EDGE,"E11"),sQuery(id+"F0.wireOp",EDGE,"E12"),sQuery(id+"F0.wireOp",EDGE,"E13"),sQuery(id+"F0.wireOp",EDGE,"E14"),sQuery(id+"F0.wireOp",EDGE,"E15"),sQuery(id+"F0.wireOp",EDGE,"E16"),sQuery(id+"F0.wireOp",EDGE,"E17"),sQuery(id+"F0.wireOp",EDGE,"fGXXUOoa-G3to-nFfg-Xp41-Spi5BgRDYh0n"),sQuery(id+"F0.wireOp",EDGE,"maiLpuxs-2Sfq-8eKx-MEtN-jPa1VSy1aRe3"),sQuery(id+"F0.wireOp",EDGE,"E19"),sQuery(id+"F0.wireOp",EDGE,"TkPDQIJV-pblC-kMUo-zlvk-0mYhqbRm7784"),sQuery(id+"F0.wireOp",EDGE,"A3QQ103k-oBam-uK2f-Ywbn-FOsahd6y3kCF"),sQuery(id+"F0.wireOp",EDGE,"E22"),sQuery(id+"F0.wireOp",EDGE,"O4fUSGsA-sgfy-2hAb-lYRv-adjy5g4jnHMn"),sQuery(id+"F0.wireOp",EDGE,"he4H8z8F-eg87-8e6K-5810-5zuvFcfIEFNb")])],"isStart":true})],"blendedInto":[makeQuery(id+"F1.opExtrude","CAP_FACE",FACE,{"disambiguationData":[OSD([sQuery(id+"F0.wireOp",EDGE,"E0.0"),sQuery(id+"F0.wireOp",EDGE,"E0.2"),sQuery(id+"F0.wireOp",EDGE,"E0.4"),sQuery(id+"F0.wireOp",EDGE,"E1.0"),sQuery(id+"F0.wireOp",EDGE,"E1.2"),sQuery(id+"F0.wireOp",EDGE,"E1.3"),sQuery(id+"F0.wireOp",EDGE,"E1.4"),sQuery(id+"F0.wireOp",EDGE,"E1.5"),sQuery(id+"F0.wireOp",EDGE,"E2.0"),sQuery(id+"F0.wireOp",EDGE,"E2.1"),sQuery(id+"F0.wireOp",EDGE,"E2.2"),sQuery(id+"F0.wireOp",EDGE,"E2.3"),sQuery(id+"F0.wireOp",EDGE,"E2.4"),subQ1,subQ0,sQuery(id+"F0.wireOp",EDGE,"E3.2"),sQuery(id+"F0.wireOp",EDGE,"E3.4"),sQuery(id+"F0.wireOp",EDGE,"E3.5"),sQuery(id+"F0.wireOp",EDGE,"E11"),sQuery(id+"F0.wireOp",EDGE,"E12"),sQuery(id+"F0.wireOp",EDGE,"E13"),sQuery(id+"F0.wireOp",EDGE,"E14"),sQuery(id+"F0.wireOp",EDGE,"E15"),sQuery(id+"F0.wireOp",EDGE,"E16"),sQuery(id+"F0.wireOp",EDGE,"E17"),sQuery(id+"F0.wireOp",EDGE,"fGXXUOoa-G3to-nFfg-Xp41-Spi5BgRDYh0n"),sQuery(id+"F0.wireOp",EDGE,"maiLpuxs-2Sfq-8eKx-MEtN-jPa1VSy1aRe3"),sQuery(id+"F0.wireOp",EDGE,"E19"),sQuery(id+"F0.wireOp",EDGE,"TkPDQIJV-pblC-kMUo-zlvk-0mYhqbRm7784"),sQuery(id+"F0.wireOp",EDGE,"A3QQ103k-oBam-uK2f-Ywbn-FOsahd6y3kCF"),sQuery(id+"F0.wireOp",EDGE,"E22"),sQuery(id+"F0.wireOp",EDGE,"O4fUSGsA-sgfy-2hAb-lYRv-adjy5g4jnHMn"),sQuery(id+"F0.wireOp",EDGE,"he4H8z8F-eg87-8e6K-5810-5zuvFcfIEFNb")])],"isStart":true})]});}
            var Q67;
            Q67=makeQuery(id+"F1.opExtrude","CAP_EDGE",EDGE,{"disambiguationData":[OSD([sQuery(id+"F0.wireOp",EDGE,"E3.1")])],"isStart":true});
            var Q68;
            Q68=makeQuery(id+"F1.opExtrude","CAP_EDGE",EDGE,{"disambiguationData":[OSD([sQuery(id+"F0.wireOp",EDGE,"E3.0")])],"isStart":true});
            var Q69;
            {var subQ0=sQuery(id+"F0.wireOp",EDGE,"E3.5");var subQ1=sQuery(id+"F0.wireOp",EDGE,"E3.0");Q69=makeQuery(id+"F11.opFillet","BLEND_EDGE",EDGE,{"blendedFrom":[makeQuery(id+"F1.opExtrude","SWEPT_EDGE",EDGE,{"disambiguationData":[OSD([subQ1,subQ0])]}),makeQuery(id+"F1.opExtrude","CAP_FACE",FACE,{"disambiguationData":[OSD([sQuery(id+"F0.wireOp",EDGE,"E0.0"),sQuery(id+"F0.wireOp",EDGE,"E0.2"),sQuery(id+"F0.wireOp",EDGE,"E0.4"),sQuery(id+"F0.wireOp",EDGE,"E1.0"),sQuery(id+"F0.wireOp",EDGE,"E1.2"),sQuery(id+"F0.wireOp",EDGE,"E1.3"),sQuery(id+"F0.wireOp",EDGE,"E1.4"),sQuery(id+"F0.wireOp",EDGE,"E1.5"),sQuery(id+"F0.wireOp",EDGE,"E2.0"),sQuery(id+"F0.wireOp",EDGE,"E2.1"),sQuery(id+"F0.wireOp",EDGE,"E2.2"),sQuery(id+"F0.wireOp",EDGE,"E2.3"),sQuery(id+"F0.wireOp",EDGE,"E2.4"),subQ1,sQuery(id+"F0.wireOp",EDGE,"E3.1"),sQuery(id+"F0.wireOp",EDGE,"E3.2"),sQuery(id+"F0.wireOp",EDGE,"E3.4"),subQ0,sQuery(id+"F0.wireOp",EDGE,"E11"),sQuery(id+"F0.wireOp",EDGE,"E12"),sQuery(id+"F0.wireOp",EDGE,"E13"),sQuery(id+"F0.wireOp",EDGE,"E14"),sQuery(id+"F0.wireOp",EDGE,"E15"),sQuery(id+"F0.wireOp",EDGE,"E16"),sQuery(id+"F0.wireOp",EDGE,"E17"),sQuery(id+"F0.wireOp",EDGE,"fGXXUOoa-G3to-nFfg-Xp41-Spi5BgRDYh0n"),sQuery(id+"F0.wireOp",EDGE,"maiLpuxs-2Sfq-8eKx-MEtN-jPa1VSy1aRe3"),sQuery(id+"F0.wireOp",EDGE,"E19"),sQuery(id+"F0.wireOp",EDGE,"TkPDQIJV-pblC-kMUo-zlvk-0mYhqbRm7784"),sQuery(id+"F0.wireOp",EDGE,"A3QQ103k-oBam-uK2f-Ywbn-FOsahd6y3kCF"),sQuery(id+"F0.wireOp",EDGE,"E22"),sQuery(id+"F0.wireOp",EDGE,"O4fUSGsA-sgfy-2hAb-lYRv-adjy5g4jnHMn"),sQuery(id+"F0.wireOp",EDGE,"he4H8z8F-eg87-8e6K-5810-5zuvFcfIEFNb")])],"isStart":true})],"blendedInto":[makeQuery(id+"F1.opExtrude","CAP_FACE",FACE,{"disambiguationData":[OSD([sQuery(id+"F0.wireOp",EDGE,"E0.0"),sQuery(id+"F0.wireOp",EDGE,"E0.2"),sQuery(id+"F0.wireOp",EDGE,"E0.4"),sQuery(id+"F0.wireOp",EDGE,"E1.0"),sQuery(id+"F0.wireOp",EDGE,"E1.2"),sQuery(id+"F0.wireOp",EDGE,"E1.3"),sQuery(id+"F0.wireOp",EDGE,"E1.4"),sQuery(id+"F0.wireOp",EDGE,"E1.5"),sQuery(id+"F0.wireOp",EDGE,"E2.0"),sQuery(id+"F0.wireOp",EDGE,"E2.1"),sQuery(id+"F0.wireOp",EDGE,"E2.2"),sQuery(id+"F0.wireOp",EDGE,"E2.3"),sQuery(id+"F0.wireOp",EDGE,"E2.4"),subQ1,sQuery(id+"F0.wireOp",EDGE,"E3.1"),sQuery(id+"F0.wireOp",EDGE,"E3.2"),sQuery(id+"F0.wireOp",EDGE,"E3.4"),subQ0,sQuery(id+"F0.wireOp",EDGE,"E11"),sQuery(id+"F0.wireOp",EDGE,"E12"),sQuery(id+"F0.wireOp",EDGE,"E13"),sQuery(id+"F0.wireOp",EDGE,"E14"),sQuery(id+"F0.wireOp",EDGE,"E15"),sQuery(id+"F0.wireOp",EDGE,"E16"),sQuery(id+"F0.wireOp",EDGE,"E17"),sQuery(id+"F0.wireOp",EDGE,"fGXXUOoa-G3to-nFfg-Xp41-Spi5BgRDYh0n"),sQuery(id+"F0.wireOp",EDGE,"maiLpuxs-2Sfq-8eKx-MEtN-jPa1VSy1aRe3"),sQuery(id+"F0.wireOp",EDGE,"E19"),sQuery(id+"F0.wireOp",EDGE,"TkPDQIJV-pblC-kMUo-zlvk-0mYhqbRm7784"),sQuery(id+"F0.wireOp",EDGE,"A3QQ103k-oBam-uK2f-Ywbn-FOsahd6y3kCF"),sQuery(id+"F0.wireOp",EDGE,"E22"),sQuery(id+"F0.wireOp",EDGE,"O4fUSGsA-sgfy-2hAb-lYRv-adjy5g4jnHMn"),sQuery(id+"F0.wireOp",EDGE,"he4H8z8F-eg87-8e6K-5810-5zuvFcfIEFNb")])],"isStart":true})]});}
            var Q70;
            Q70=makeQuery(id+"F1.opExtrude","CAP_EDGE",EDGE,{"disambiguationData":[OSD([sQuery(id+"F0.wireOp",EDGE,"E3.5")])],"isStart":true});
            var Q71;
            Q71=makeQuery(id+"F1.opExtrude","CAP_EDGE",EDGE,{"disambiguationData":[OSD([sQuery(id+"F0.wireOp",EDGE,"E14")])],"isStart":true});
            var Q72;
            {var subQ0=sQuery(id+"F0.wireOp",EDGE,"E14");var subQ1=sQuery(id+"F0.wireOp",EDGE,"E13");Q72=makeQuery(id+"F12.opFillet","BLEND_EDGE",EDGE,{"blendedFrom":[makeQuery(id+"F1.opExtrude","SWEPT_EDGE",EDGE,{"disambiguationData":[OSD([sQuery(id+"F0.wireOp",EDGE,"E10"),subQ1,subQ0])]}),makeQuery(id+"F1.opExtrude","CAP_FACE",FACE,{"disambiguationData":[OSD([sQuery(id+"F0.wireOp",EDGE,"E0.0"),sQuery(id+"F0.wireOp",EDGE,"E0.2"),sQuery(id+"F0.wireOp",EDGE,"E0.4"),sQuery(id+"F0.wireOp",EDGE,"E1.0"),sQuery(id+"F0.wireOp",EDGE,"E1.2"),sQuery(id+"F0.wireOp",EDGE,"E1.3"),sQuery(id+"F0.wireOp",EDGE,"E1.4"),sQuery(id+"F0.wireOp",EDGE,"E1.5"),sQuery(id+"F0.wireOp",EDGE,"E2.0"),sQuery(id+"F0.wireOp",EDGE,"E2.1"),sQuery(id+"F0.wireOp",EDGE,"E2.2"),sQuery(id+"F0.wireOp",EDGE,"E2.3"),sQuery(id+"F0.wireOp",EDGE,"E2.4"),sQuery(id+"F0.wireOp",EDGE,"E3.0"),sQuery(id+"F0.wireOp",EDGE,"E3.1"),sQuery(id+"F0.wireOp",EDGE,"E3.2"),sQuery(id+"F0.wireOp",EDGE,"E3.4"),sQuery(id+"F0.wireOp",EDGE,"E3.5"),sQuery(id+"F0.wireOp",EDGE,"E11"),sQuery(id+"F0.wireOp",EDGE,"E12"),subQ1,subQ0,sQuery(id+"F0.wireOp",EDGE,"E15"),sQuery(id+"F0.wireOp",EDGE,"E16"),sQuery(id+"F0.wireOp",EDGE,"E17"),sQuery(id+"F0.wireOp",EDGE,"fGXXUOoa-G3to-nFfg-Xp41-Spi5BgRDYh0n"),sQuery(id+"F0.wireOp",EDGE,"maiLpuxs-2Sfq-8eKx-MEtN-jPa1VSy1aRe3"),sQuery(id+"F0.wireOp",EDGE,"E19"),sQuery(id+"F0.wireOp",EDGE,"TkPDQIJV-pblC-kMUo-zlvk-0mYhqbRm7784"),sQuery(id+"F0.wireOp",EDGE,"A3QQ103k-oBam-uK2f-Ywbn-FOsahd6y3kCF"),sQuery(id+"F0.wireOp",EDGE,"E22"),sQuery(id+"F0.wireOp",EDGE,"O4fUSGsA-sgfy-2hAb-lYRv-adjy5g4jnHMn"),sQuery(id+"F0.wireOp",EDGE,"he4H8z8F-eg87-8e6K-5810-5zuvFcfIEFNb")])],"isStart":true})],"blendedInto":[makeQuery(id+"F1.opExtrude","CAP_FACE",FACE,{"disambiguationData":[OSD([sQuery(id+"F0.wireOp",EDGE,"E0.0"),sQuery(id+"F0.wireOp",EDGE,"E0.2"),sQuery(id+"F0.wireOp",EDGE,"E0.4"),sQuery(id+"F0.wireOp",EDGE,"E1.0"),sQuery(id+"F0.wireOp",EDGE,"E1.2"),sQuery(id+"F0.wireOp",EDGE,"E1.3"),sQuery(id+"F0.wireOp",EDGE,"E1.4"),sQuery(id+"F0.wireOp",EDGE,"E1.5"),sQuery(id+"F0.wireOp",EDGE,"E2.0"),sQuery(id+"F0.wireOp",EDGE,"E2.1"),sQuery(id+"F0.wireOp",EDGE,"E2.2"),sQuery(id+"F0.wireOp",EDGE,"E2.3"),sQuery(id+"F0.wireOp",EDGE,"E2.4"),sQuery(id+"F0.wireOp",EDGE,"E3.0"),sQuery(id+"F0.wireOp",EDGE,"E3.1"),sQuery(id+"F0.wireOp",EDGE,"E3.2"),sQuery(id+"F0.wireOp",EDGE,"E3.4"),sQuery(id+"F0.wireOp",EDGE,"E3.5"),sQuery(id+"F0.wireOp",EDGE,"E11"),sQuery(id+"F0.wireOp",EDGE,"E12"),subQ1,subQ0,sQuery(id+"F0.wireOp",EDGE,"E15"),sQuery(id+"F0.wireOp",EDGE,"E16"),sQuery(id+"F0.wireOp",EDGE,"E17"),sQuery(id+"F0.wireOp",EDGE,"fGXXUOoa-G3to-nFfg-Xp41-Spi5BgRDYh0n"),sQuery(id+"F0.wireOp",EDGE,"maiLpuxs-2Sfq-8eKx-MEtN-jPa1VSy1aRe3"),sQuery(id+"F0.wireOp",EDGE,"E19"),sQuery(id+"F0.wireOp",EDGE,"TkPDQIJV-pblC-kMUo-zlvk-0mYhqbRm7784"),sQuery(id+"F0.wireOp",EDGE,"A3QQ103k-oBam-uK2f-Ywbn-FOsahd6y3kCF"),sQuery(id+"F0.wireOp",EDGE,"E22"),sQuery(id+"F0.wireOp",EDGE,"O4fUSGsA-sgfy-2hAb-lYRv-adjy5g4jnHMn"),sQuery(id+"F0.wireOp",EDGE,"he4H8z8F-eg87-8e6K-5810-5zuvFcfIEFNb")])],"isStart":true})]});}
            var Q73;
            Q73=makeQuery(id+"F1.opExtrude","CAP_EDGE",EDGE,{"disambiguationData":[OSD([sQuery(id+"F0.wireOp",EDGE,"E13")])],"isStart":true});
            var Q74;
            Q74=makeQuery(id+"F1.opExtrude","CAP_EDGE",EDGE,{"disambiguationData":[OSD([sQuery(id+"F0.wireOp",EDGE,"E3.4")])],"isStart":true});
            var Q75;
            {var subQ0=sQuery(id+"F0.wireOp",EDGE,"E3.4");var subQ1=sQuery(id+"F0.wireOp",EDGE,"E0.0");Q75=makeQuery(id+"F11.opFillet","BLEND_EDGE",EDGE,{"blendedFrom":[makeQuery(id+"F1.opExtrude","SWEPT_EDGE",EDGE,{"disambiguationData":[OSD([subQ1,subQ0])]}),makeQuery(id+"F1.opExtrude","CAP_FACE",FACE,{"disambiguationData":[OSD([subQ1,sQuery(id+"F0.wireOp",EDGE,"E0.2"),sQuery(id+"F0.wireOp",EDGE,"E0.4"),sQuery(id+"F0.wireOp",EDGE,"E1.0"),sQuery(id+"F0.wireOp",EDGE,"E1.2"),sQuery(id+"F0.wireOp",EDGE,"E1.3"),sQuery(id+"F0.wireOp",EDGE,"E1.4"),sQuery(id+"F0.wireOp",EDGE,"E1.5"),sQuery(id+"F0.wireOp",EDGE,"E2.0"),sQuery(id+"F0.wireOp",EDGE,"E2.1"),sQuery(id+"F0.wireOp",EDGE,"E2.2"),sQuery(id+"F0.wireOp",EDGE,"E2.3"),sQuery(id+"F0.wireOp",EDGE,"E2.4"),sQuery(id+"F0.wireOp",EDGE,"E3.0"),sQuery(id+"F0.wireOp",EDGE,"E3.1"),sQuery(id+"F0.wireOp",EDGE,"E3.2"),subQ0,sQuery(id+"F0.wireOp",EDGE,"E3.5"),sQuery(id+"F0.wireOp",EDGE,"E11"),sQuery(id+"F0.wireOp",EDGE,"E12"),sQuery(id+"F0.wireOp",EDGE,"E13"),sQuery(id+"F0.wireOp",EDGE,"E14"),sQuery(id+"F0.wireOp",EDGE,"E15"),sQuery(id+"F0.wireOp",EDGE,"E16"),sQuery(id+"F0.wireOp",EDGE,"E17"),sQuery(id+"F0.wireOp",EDGE,"fGXXUOoa-G3to-nFfg-Xp41-Spi5BgRDYh0n"),sQuery(id+"F0.wireOp",EDGE,"maiLpuxs-2Sfq-8eKx-MEtN-jPa1VSy1aRe3"),sQuery(id+"F0.wireOp",EDGE,"E19"),sQuery(id+"F0.wireOp",EDGE,"TkPDQIJV-pblC-kMUo-zlvk-0mYhqbRm7784"),sQuery(id+"F0.wireOp",EDGE,"A3QQ103k-oBam-uK2f-Ywbn-FOsahd6y3kCF"),sQuery(id+"F0.wireOp",EDGE,"E22"),sQuery(id+"F0.wireOp",EDGE,"O4fUSGsA-sgfy-2hAb-lYRv-adjy5g4jnHMn"),sQuery(id+"F0.wireOp",EDGE,"he4H8z8F-eg87-8e6K-5810-5zuvFcfIEFNb")])],"isStart":true})],"blendedInto":[makeQuery(id+"F1.opExtrude","CAP_FACE",FACE,{"disambiguationData":[OSD([subQ1,sQuery(id+"F0.wireOp",EDGE,"E0.2"),sQuery(id+"F0.wireOp",EDGE,"E0.4"),sQuery(id+"F0.wireOp",EDGE,"E1.0"),sQuery(id+"F0.wireOp",EDGE,"E1.2"),sQuery(id+"F0.wireOp",EDGE,"E1.3"),sQuery(id+"F0.wireOp",EDGE,"E1.4"),sQuery(id+"F0.wireOp",EDGE,"E1.5"),sQuery(id+"F0.wireOp",EDGE,"E2.0"),sQuery(id+"F0.wireOp",EDGE,"E2.1"),sQuery(id+"F0.wireOp",EDGE,"E2.2"),sQuery(id+"F0.wireOp",EDGE,"E2.3"),sQuery(id+"F0.wireOp",EDGE,"E2.4"),sQuery(id+"F0.wireOp",EDGE,"E3.0"),sQuery(id+"F0.wireOp",EDGE,"E3.1"),sQuery(id+"F0.wireOp",EDGE,"E3.2"),subQ0,sQuery(id+"F0.wireOp",EDGE,"E3.5"),sQuery(id+"F0.wireOp",EDGE,"E11"),sQuery(id+"F0.wireOp",EDGE,"E12"),sQuery(id+"F0.wireOp",EDGE,"E13"),sQuery(id+"F0.wireOp",EDGE,"E14"),sQuery(id+"F0.wireOp",EDGE,"E15"),sQuery(id+"F0.wireOp",EDGE,"E16"),sQuery(id+"F0.wireOp",EDGE,"E17"),sQuery(id+"F0.wireOp",EDGE,"fGXXUOoa-G3to-nFfg-Xp41-Spi5BgRDYh0n"),sQuery(id+"F0.wireOp",EDGE,"maiLpuxs-2Sfq-8eKx-MEtN-jPa1VSy1aRe3"),sQuery(id+"F0.wireOp",EDGE,"E19"),sQuery(id+"F0.wireOp",EDGE,"TkPDQIJV-pblC-kMUo-zlvk-0mYhqbRm7784"),sQuery(id+"F0.wireOp",EDGE,"A3QQ103k-oBam-uK2f-Ywbn-FOsahd6y3kCF"),sQuery(id+"F0.wireOp",EDGE,"E22"),sQuery(id+"F0.wireOp",EDGE,"O4fUSGsA-sgfy-2hAb-lYRv-adjy5g4jnHMn"),sQuery(id+"F0.wireOp",EDGE,"he4H8z8F-eg87-8e6K-5810-5zuvFcfIEFNb")])],"isStart":true})]});}
            var Q76;
            Q76=makeQuery(id+"F1.opExtrude","CAP_EDGE",EDGE,{"disambiguationData":[OSD([sQuery(id+"F0.wireOp",EDGE,"E0.0")])],"isStart":true});
            var Q77;
            {var subQ0=sQuery(id+"F0.wireOp",EDGE,"E1.0");var subQ1=sQuery(id+"F0.wireOp",EDGE,"E0.0");Q77=makeQuery(id+"F11.opFillet","BLEND_EDGE",EDGE,{"blendedFrom":[makeQuery(id+"F1.opExtrude","SWEPT_EDGE",EDGE,{"disambiguationData":[OSD([subQ1,subQ0,sQuery(id+"F0.wireOp",EDGE,"E1.1")])]}),makeQuery(id+"F1.opExtrude","CAP_FACE",FACE,{"disambiguationData":[OSD([subQ1,sQuery(id+"F0.wireOp",EDGE,"E0.2"),sQuery(id+"F0.wireOp",EDGE,"E0.4"),subQ0,sQuery(id+"F0.wireOp",EDGE,"E1.2"),sQuery(id+"F0.wireOp",EDGE,"E1.3"),sQuery(id+"F0.wireOp",EDGE,"E1.4"),sQuery(id+"F0.wireOp",EDGE,"E1.5"),sQuery(id+"F0.wireOp",EDGE,"E2.0"),sQuery(id+"F0.wireOp",EDGE,"E2.1"),sQuery(id+"F0.wireOp",EDGE,"E2.2"),sQuery(id+"F0.wireOp",EDGE,"E2.3"),sQuery(id+"F0.wireOp",EDGE,"E2.4"),sQuery(id+"F0.wireOp",EDGE,"E3.0"),sQuery(id+"F0.wireOp",EDGE,"E3.1"),sQuery(id+"F0.wireOp",EDGE,"E3.2"),sQuery(id+"F0.wireOp",EDGE,"E3.4"),sQuery(id+"F0.wireOp",EDGE,"E3.5"),sQuery(id+"F0.wireOp",EDGE,"E11"),sQuery(id+"F0.wireOp",EDGE,"E12"),sQuery(id+"F0.wireOp",EDGE,"E13"),sQuery(id+"F0.wireOp",EDGE,"E14"),sQuery(id+"F0.wireOp",EDGE,"E15"),sQuery(id+"F0.wireOp",EDGE,"E16"),sQuery(id+"F0.wireOp",EDGE,"E17"),sQuery(id+"F0.wireOp",EDGE,"fGXXUOoa-G3to-nFfg-Xp41-Spi5BgRDYh0n"),sQuery(id+"F0.wireOp",EDGE,"maiLpuxs-2Sfq-8eKx-MEtN-jPa1VSy1aRe3"),sQuery(id+"F0.wireOp",EDGE,"E19"),sQuery(id+"F0.wireOp",EDGE,"TkPDQIJV-pblC-kMUo-zlvk-0mYhqbRm7784"),sQuery(id+"F0.wireOp",EDGE,"A3QQ103k-oBam-uK2f-Ywbn-FOsahd6y3kCF"),sQuery(id+"F0.wireOp",EDGE,"E22"),sQuery(id+"F0.wireOp",EDGE,"O4fUSGsA-sgfy-2hAb-lYRv-adjy5g4jnHMn"),sQuery(id+"F0.wireOp",EDGE,"he4H8z8F-eg87-8e6K-5810-5zuvFcfIEFNb")])],"isStart":true})],"blendedInto":[makeQuery(id+"F1.opExtrude","CAP_FACE",FACE,{"disambiguationData":[OSD([subQ1,sQuery(id+"F0.wireOp",EDGE,"E0.2"),sQuery(id+"F0.wireOp",EDGE,"E0.4"),subQ0,sQuery(id+"F0.wireOp",EDGE,"E1.2"),sQuery(id+"F0.wireOp",EDGE,"E1.3"),sQuery(id+"F0.wireOp",EDGE,"E1.4"),sQuery(id+"F0.wireOp",EDGE,"E1.5"),sQuery(id+"F0.wireOp",EDGE,"E2.0"),sQuery(id+"F0.wireOp",EDGE,"E2.1"),sQuery(id+"F0.wireOp",EDGE,"E2.2"),sQuery(id+"F0.wireOp",EDGE,"E2.3"),sQuery(id+"F0.wireOp",EDGE,"E2.4"),sQuery(id+"F0.wireOp",EDGE,"E3.0"),sQuery(id+"F0.wireOp",EDGE,"E3.1"),sQuery(id+"F0.wireOp",EDGE,"E3.2"),sQuery(id+"F0.wireOp",EDGE,"E3.4"),sQuery(id+"F0.wireOp",EDGE,"E3.5"),sQuery(id+"F0.wireOp",EDGE,"E11"),sQuery(id+"F0.wireOp",EDGE,"E12"),sQuery(id+"F0.wireOp",EDGE,"E13"),sQuery(id+"F0.wireOp",EDGE,"E14"),sQuery(id+"F0.wireOp",EDGE,"E15"),sQuery(id+"F0.wireOp",EDGE,"E16"),sQuery(id+"F0.wireOp",EDGE,"E17"),sQuery(id+"F0.wireOp",EDGE,"fGXXUOoa-G3to-nFfg-Xp41-Spi5BgRDYh0n"),sQuery(id+"F0.wireOp",EDGE,"maiLpuxs-2Sfq-8eKx-MEtN-jPa1VSy1aRe3"),sQuery(id+"F0.wireOp",EDGE,"E19"),sQuery(id+"F0.wireOp",EDGE,"TkPDQIJV-pblC-kMUo-zlvk-0mYhqbRm7784"),sQuery(id+"F0.wireOp",EDGE,"A3QQ103k-oBam-uK2f-Ywbn-FOsahd6y3kCF"),sQuery(id+"F0.wireOp",EDGE,"E22"),sQuery(id+"F0.wireOp",EDGE,"O4fUSGsA-sgfy-2hAb-lYRv-adjy5g4jnHMn"),sQuery(id+"F0.wireOp",EDGE,"he4H8z8F-eg87-8e6K-5810-5zuvFcfIEFNb")])],"isStart":true})]});}
            var Q78;
            Q78=makeQuery(id+"F1.opExtrude","CAP_EDGE",EDGE,{"disambiguationData":[OSD([sQuery(id+"F0.wireOp",EDGE,"E1.0")])],"isStart":true});
            var Q79;
            {var subQ0=sQuery(id+"F0.wireOp",EDGE,"E1.5");var subQ1=sQuery(id+"F0.wireOp",EDGE,"E1.0");Q79=makeQuery(id+"F11.opFillet","BLEND_EDGE",EDGE,{"blendedFrom":[makeQuery(id+"F1.opExtrude","SWEPT_EDGE",EDGE,{"disambiguationData":[OSD([subQ1,subQ0])]}),makeQuery(id+"F1.opExtrude","CAP_FACE",FACE,{"disambiguationData":[OSD([sQuery(id+"F0.wireOp",EDGE,"E0.0"),sQuery(id+"F0.wireOp",EDGE,"E0.2"),sQuery(id+"F0.wireOp",EDGE,"E0.4"),subQ1,sQuery(id+"F0.wireOp",EDGE,"E1.2"),sQuery(id+"F0.wireOp",EDGE,"E1.3"),sQuery(id+"F0.wireOp",EDGE,"E1.4"),subQ0,sQuery(id+"F0.wireOp",EDGE,"E2.0"),sQuery(id+"F0.wireOp",EDGE,"E2.1"),sQuery(id+"F0.wireOp",EDGE,"E2.2"),sQuery(id+"F0.wireOp",EDGE,"E2.3"),sQuery(id+"F0.wireOp",EDGE,"E2.4"),sQuery(id+"F0.wireOp",EDGE,"E3.0"),sQuery(id+"F0.wireOp",EDGE,"E3.1"),sQuery(id+"F0.wireOp",EDGE,"E3.2"),sQuery(id+"F0.wireOp",EDGE,"E3.4"),sQuery(id+"F0.wireOp",EDGE,"E3.5"),sQuery(id+"F0.wireOp",EDGE,"E11"),sQuery(id+"F0.wireOp",EDGE,"E12"),sQuery(id+"F0.wireOp",EDGE,"E13"),sQuery(id+"F0.wireOp",EDGE,"E14"),sQuery(id+"F0.wireOp",EDGE,"E15"),sQuery(id+"F0.wireOp",EDGE,"E16"),sQuery(id+"F0.wireOp",EDGE,"E17"),sQuery(id+"F0.wireOp",EDGE,"fGXXUOoa-G3to-nFfg-Xp41-Spi5BgRDYh0n"),sQuery(id+"F0.wireOp",EDGE,"maiLpuxs-2Sfq-8eKx-MEtN-jPa1VSy1aRe3"),sQuery(id+"F0.wireOp",EDGE,"E19"),sQuery(id+"F0.wireOp",EDGE,"TkPDQIJV-pblC-kMUo-zlvk-0mYhqbRm7784"),sQuery(id+"F0.wireOp",EDGE,"A3QQ103k-oBam-uK2f-Ywbn-FOsahd6y3kCF"),sQuery(id+"F0.wireOp",EDGE,"E22"),sQuery(id+"F0.wireOp",EDGE,"O4fUSGsA-sgfy-2hAb-lYRv-adjy5g4jnHMn"),sQuery(id+"F0.wireOp",EDGE,"he4H8z8F-eg87-8e6K-5810-5zuvFcfIEFNb")])],"isStart":true})],"blendedInto":[makeQuery(id+"F1.opExtrude","CAP_FACE",FACE,{"disambiguationData":[OSD([sQuery(id+"F0.wireOp",EDGE,"E0.0"),sQuery(id+"F0.wireOp",EDGE,"E0.2"),sQuery(id+"F0.wireOp",EDGE,"E0.4"),subQ1,sQuery(id+"F0.wireOp",EDGE,"E1.2"),sQuery(id+"F0.wireOp",EDGE,"E1.3"),sQuery(id+"F0.wireOp",EDGE,"E1.4"),subQ0,sQuery(id+"F0.wireOp",EDGE,"E2.0"),sQuery(id+"F0.wireOp",EDGE,"E2.1"),sQuery(id+"F0.wireOp",EDGE,"E2.2"),sQuery(id+"F0.wireOp",EDGE,"E2.3"),sQuery(id+"F0.wireOp",EDGE,"E2.4"),sQuery(id+"F0.wireOp",EDGE,"E3.0"),sQuery(id+"F0.wireOp",EDGE,"E3.1"),sQuery(id+"F0.wireOp",EDGE,"E3.2"),sQuery(id+"F0.wireOp",EDGE,"E3.4"),sQuery(id+"F0.wireOp",EDGE,"E3.5"),sQuery(id+"F0.wireOp",EDGE,"E11"),sQuery(id+"F0.wireOp",EDGE,"E12"),sQuery(id+"F0.wireOp",EDGE,"E13"),sQuery(id+"F0.wireOp",EDGE,"E14"),sQuery(id+"F0.wireOp",EDGE,"E15"),sQuery(id+"F0.wireOp",EDGE,"E16"),sQuery(id+"F0.wireOp",EDGE,"E17"),sQuery(id+"F0.wireOp",EDGE,"fGXXUOoa-G3to-nFfg-Xp41-Spi5BgRDYh0n"),sQuery(id+"F0.wireOp",EDGE,"maiLpuxs-2Sfq-8eKx-MEtN-jPa1VSy1aRe3"),sQuery(id+"F0.wireOp",EDGE,"E19"),sQuery(id+"F0.wireOp",EDGE,"TkPDQIJV-pblC-kMUo-zlvk-0mYhqbRm7784"),sQuery(id+"F0.wireOp",EDGE,"A3QQ103k-oBam-uK2f-Ywbn-FOsahd6y3kCF"),sQuery(id+"F0.wireOp",EDGE,"E22"),sQuery(id+"F0.wireOp",EDGE,"O4fUSGsA-sgfy-2hAb-lYRv-adjy5g4jnHMn"),sQuery(id+"F0.wireOp",EDGE,"he4H8z8F-eg87-8e6K-5810-5zuvFcfIEFNb")])],"isStart":true})]});}
            var Q80;
            Q80=makeQuery(id+"F1.opExtrude","CAP_EDGE",EDGE,{"disambiguationData":[OSD([sQuery(id+"F0.wireOp",EDGE,"E1.5")])],"isStart":true});
            var Q81;
            {var subQ0=sQuery(id+"F0.wireOp",EDGE,"E1.5");var subQ1=sQuery(id+"F0.wireOp",EDGE,"E1.4");Q81=makeQuery(id+"F11.opFillet","BLEND_EDGE",EDGE,{"blendedFrom":[makeQuery(id+"F1.opExtrude","SWEPT_EDGE",EDGE,{"disambiguationData":[OSD([subQ1,subQ0])]}),makeQuery(id+"F1.opExtrude","CAP_FACE",FACE,{"disambiguationData":[OSD([sQuery(id+"F0.wireOp",EDGE,"E0.0"),sQuery(id+"F0.wireOp",EDGE,"E0.2"),sQuery(id+"F0.wireOp",EDGE,"E0.4"),sQuery(id+"F0.wireOp",EDGE,"E1.0"),sQuery(id+"F0.wireOp",EDGE,"E1.2"),sQuery(id+"F0.wireOp",EDGE,"E1.3"),subQ1,subQ0,sQuery(id+"F0.wireOp",EDGE,"E2.0"),sQuery(id+"F0.wireOp",EDGE,"E2.1"),sQuery(id+"F0.wireOp",EDGE,"E2.2"),sQuery(id+"F0.wireOp",EDGE,"E2.3"),sQuery(id+"F0.wireOp",EDGE,"E2.4"),sQuery(id+"F0.wireOp",EDGE,"E3.0"),sQuery(id+"F0.wireOp",EDGE,"E3.1"),sQuery(id+"F0.wireOp",EDGE,"E3.2"),sQuery(id+"F0.wireOp",EDGE,"E3.4"),sQuery(id+"F0.wireOp",EDGE,"E3.5"),sQuery(id+"F0.wireOp",EDGE,"E11"),sQuery(id+"F0.wireOp",EDGE,"E12"),sQuery(id+"F0.wireOp",EDGE,"E13"),sQuery(id+"F0.wireOp",EDGE,"E14"),sQuery(id+"F0.wireOp",EDGE,"E15"),sQuery(id+"F0.wireOp",EDGE,"E16"),sQuery(id+"F0.wireOp",EDGE,"E17"),sQuery(id+"F0.wireOp",EDGE,"fGXXUOoa-G3to-nFfg-Xp41-Spi5BgRDYh0n"),sQuery(id+"F0.wireOp",EDGE,"maiLpuxs-2Sfq-8eKx-MEtN-jPa1VSy1aRe3"),sQuery(id+"F0.wireOp",EDGE,"E19"),sQuery(id+"F0.wireOp",EDGE,"TkPDQIJV-pblC-kMUo-zlvk-0mYhqbRm7784"),sQuery(id+"F0.wireOp",EDGE,"A3QQ103k-oBam-uK2f-Ywbn-FOsahd6y3kCF"),sQuery(id+"F0.wireOp",EDGE,"E22"),sQuery(id+"F0.wireOp",EDGE,"O4fUSGsA-sgfy-2hAb-lYRv-adjy5g4jnHMn"),sQuery(id+"F0.wireOp",EDGE,"he4H8z8F-eg87-8e6K-5810-5zuvFcfIEFNb")])],"isStart":true})],"blendedInto":[makeQuery(id+"F1.opExtrude","CAP_FACE",FACE,{"disambiguationData":[OSD([sQuery(id+"F0.wireOp",EDGE,"E0.0"),sQuery(id+"F0.wireOp",EDGE,"E0.2"),sQuery(id+"F0.wireOp",EDGE,"E0.4"),sQuery(id+"F0.wireOp",EDGE,"E1.0"),sQuery(id+"F0.wireOp",EDGE,"E1.2"),sQuery(id+"F0.wireOp",EDGE,"E1.3"),subQ1,subQ0,sQuery(id+"F0.wireOp",EDGE,"E2.0"),sQuery(id+"F0.wireOp",EDGE,"E2.1"),sQuery(id+"F0.wireOp",EDGE,"E2.2"),sQuery(id+"F0.wireOp",EDGE,"E2.3"),sQuery(id+"F0.wireOp",EDGE,"E2.4"),sQuery(id+"F0.wireOp",EDGE,"E3.0"),sQuery(id+"F0.wireOp",EDGE,"E3.1"),sQuery(id+"F0.wireOp",EDGE,"E3.2"),sQuery(id+"F0.wireOp",EDGE,"E3.4"),sQuery(id+"F0.wireOp",EDGE,"E3.5"),sQuery(id+"F0.wireOp",EDGE,"E11"),sQuery(id+"F0.wireOp",EDGE,"E12"),sQuery(id+"F0.wireOp",EDGE,"E13"),sQuery(id+"F0.wireOp",EDGE,"E14"),sQuery(id+"F0.wireOp",EDGE,"E15"),sQuery(id+"F0.wireOp",EDGE,"E16"),sQuery(id+"F0.wireOp",EDGE,"E17"),sQuery(id+"F0.wireOp",EDGE,"fGXXUOoa-G3to-nFfg-Xp41-Spi5BgRDYh0n"),sQuery(id+"F0.wireOp",EDGE,"maiLpuxs-2Sfq-8eKx-MEtN-jPa1VSy1aRe3"),sQuery(id+"F0.wireOp",EDGE,"E19"),sQuery(id+"F0.wireOp",EDGE,"TkPDQIJV-pblC-kMUo-zlvk-0mYhqbRm7784"),sQuery(id+"F0.wireOp",EDGE,"A3QQ103k-oBam-uK2f-Ywbn-FOsahd6y3kCF"),sQuery(id+"F0.wireOp",EDGE,"E22"),sQuery(id+"F0.wireOp",EDGE,"O4fUSGsA-sgfy-2hAb-lYRv-adjy5g4jnHMn"),sQuery(id+"F0.wireOp",EDGE,"he4H8z8F-eg87-8e6K-5810-5zuvFcfIEFNb")])],"isStart":true})]});}
            var Q82;
            Q82=makeQuery(id+"F1.opExtrude","CAP_EDGE",EDGE,{"disambiguationData":[OSD([sQuery(id+"F0.wireOp",EDGE,"E1.4")])],"isStart":true});
            fillet(context, id + "F13", {"entities" : qUnion([Q0, Q1, Q2, Q3, Q4, Q5, Q6, Q7, Q8, Q9, Q10, Q11, Q12, Q13, Q14, Q15, Q16, Q17, Q18, Q19, Q20, Q21, Q22, Q23, Q24, Q25, Q26, Q27, Q28, Q29, Q30, Q31, Q32, Q33, Q34, Q35, Q36, Q37, Q38, Q39, Q40, Q41, Q42, Q43, Q44, Q45, Q46, Q47, Q48, Q49, Q50, Q51, Q52, Q53, Q54, Q55, Q56, Q57, Q58, Q59, Q60, Q61, Q62, Q63, Q64, Q65, Q66, Q67, Q68, Q69, Q70, Q71, Q72, Q73, Q74, Q75, Q76, Q77, Q78, Q79, Q80, Q81, Q82]), "radius" : 2.54 * mm, "tangentPropagation" : true, "allowEdgeOverflow" : false});
        }
        {
            var Q0;
            Q0=makeQuery(id+"F5.opExtrude","CAP_EDGE",EDGE,{"disambiguationData":[OSD([sQuery(id+"F4.wireOp",EDGE,"E38")])],"isStart":true});
            var Q1;
            Q1=makeQuery(id+"F6.opExtrude","CAP_EDGE",EDGE,{"disambiguationData":[OSD([sQuery(id+"F4.wireOp",EDGE,"E36")])],"isStart":true});
            var Q2;
            Q2=makeQuery(id+"F5.opExtrude","CAP_EDGE",EDGE,{"disambiguationData":[OSD([sQuery(id+"F4.wireOp",EDGE,"E39")])],"isStart":true});
            var Q3;
            Q3=makeQuery(id+"F5.opExtrude","CAP_EDGE",EDGE,{"disambiguationData":[OSD([sQuery(id+"F4.wireOp",EDGE,"E35")])],"isStart":true});
            var Q4;
            Q4=makeQuery(id+"F6.opExtrude","CAP_EDGE",EDGE,{"disambiguationData":[OSD([sQuery(id+"F4.wireOp",EDGE,"E32")])],"isStart":true});
            var Q5;
            Q5=makeQuery(id+"F5.opExtrude","CAP_EDGE",EDGE,{"disambiguationData":[OSD([sQuery(id+"F4.wireOp",EDGE,"E34")])],"isStart":true});
            var Q6;
            Q6=makeQuery(id+"F5.opExtrude","CAP_EDGE",EDGE,{"disambiguationData":[OSD([sQuery(id+"F4.wireOp",EDGE,"E33")])],"isStart":true});
            var Q7;
            Q7=makeQuery(id+"F5.opExtrude","CAP_EDGE",EDGE,{"disambiguationData":[OSD([sQuery(id+"F4.wireOp",EDGE,"E37")])],"isStart":true});
            fillet(context, id + "F14", {"entities" : qUnion([Q0, Q1, Q2, Q3, Q4, Q5, Q6, Q7]), "radius" : 2.54 * mm, "tangentPropagation" : true, "allowEdgeOverflow" : false});
        }
        {
            var Q0;
            Q0=makeQuery(id+"F9.imprint","IMPRINT",FACE,{"disambiguationData":[TD([[makeQuery(id+"F9.imprint","IMPRINT",EDGE,{"derivedFrom":sQuery(id+"F9.wireOp",EDGE,"E46")}),-1.0]])]});
            var Q1;
            Q1=makeQuery(id+"F9.imprint","IMPRINT",FACE,{"disambiguationData":[TD([[makeQuery(id+"F9.imprint","IMPRINT",EDGE,{"derivedFrom":sQuery(id+"F9.wireOp",EDGE,"E47")}),-1.0]])]});
            extrude(context, id + "F15", {"entities" : qUnion([Q0, Q1]), "operationType" : NewBodyOperationType.ADD, "depth" : 1.27 * mm});
        }
    });
